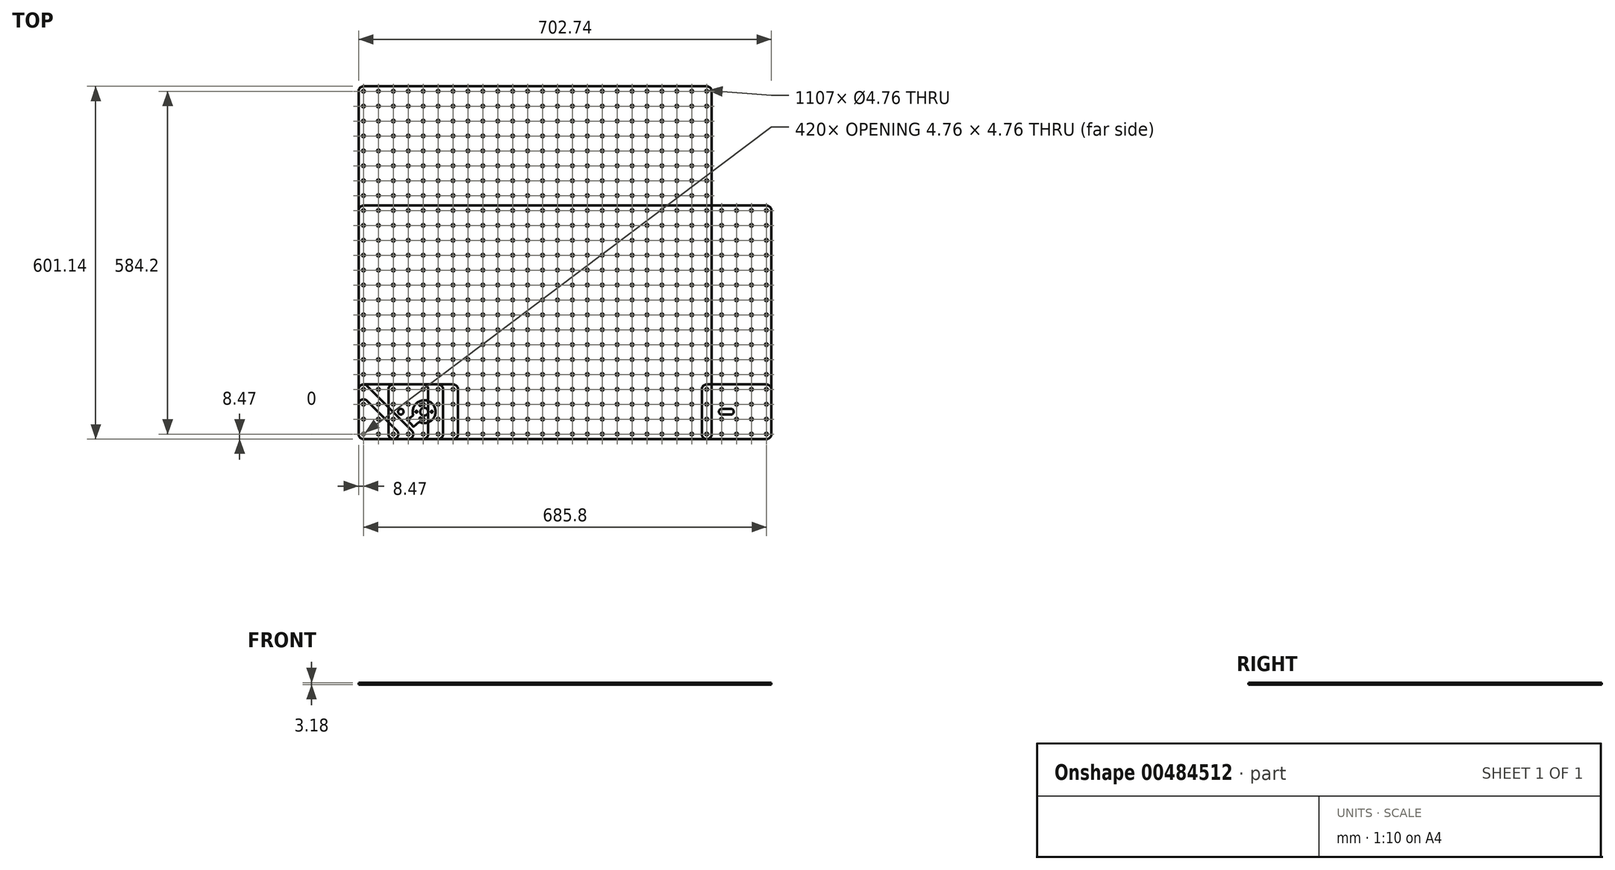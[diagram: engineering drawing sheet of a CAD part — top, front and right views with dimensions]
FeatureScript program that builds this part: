
annotation { "Feature Type Name" : "Feature", "Feature Type Description" : "" }
export const myFeature = defineFeature(function(context is Context, id is Id, definition is map)
    precondition{}
    {
        {
            assignVariable(context, id + "F0", {"name" : "bitDiameter", "anyValue" : 1 / 8});
        }
        {
            var Q0;
            Q0=qCreatedBy(makeId("Top.planeOp"),FACE);
            var sketch = newSketch(context, id + "F1", { "sketchPlane" : qUnion([Q0])});
            skCircle(sketch, "E0", {"center": v(0, 0) * mm, "radius": 2.38 * mm});
            skCircle(sketch, "E1.0.1.0", {"center": v(0, 25.4) * mm, "radius": 2.38 * mm});
            skCircle(sketch, "E1.1.0.0", {"center": v(25.4, 0) * mm, "radius": 2.38 * mm});
            skCircle(sketch, "E1.1.1.0", {"center": v(25.4, 25.4) * mm, "radius": 2.38 * mm});
            skCircle(sketch, "E1.2.0.0", {"center": v(50.8, 0) * mm, "radius": 2.38 * mm});
            skCircle(sketch, "E1.2.1.0", {"center": v(50.8, 25.4) * mm, "radius": 2.38 * mm});
            skLineSegment(sketch, "E1.direction1", {"start": v(0, 0) * mm, "end": v(25.4, 0) * mm, "construction": true});
            skLineSegment(sketch, "E1.direction2", {"start": v(0, 0) * mm, "end": v(0, 25.4) * mm, "construction": true});
            skCircle(sketch, "E2.0.0.2", {"center": v(0, 50.8) * mm, "radius": 2.38 * mm});
            skCircle(sketch, "E2.0.0.3", {"center": v(0, 76.2) * mm, "radius": 2.38 * mm});
            skCircle(sketch, "E2.0.0.4", {"center": v(0, 101.6) * mm, "radius": 2.38 * mm});
            skCircle(sketch, "E2.0.0.5", {"center": v(0, 127) * mm, "radius": 2.38 * mm});
            skCircle(sketch, "E2.0.0.6", {"center": v(0, 152.4) * mm, "radius": 2.38 * mm});
            skCircle(sketch, "E2.0.0.7", {"center": v(0, 177.8) * mm, "radius": 2.38 * mm});
            skCircle(sketch, "E2.0.0.8", {"center": v(0, 203.2) * mm, "radius": 2.38 * mm});
            skCircle(sketch, "E2.0.0.9", {"center": v(0, 228.6) * mm, "radius": 2.38 * mm});
            skCircle(sketch, "E2.0.0.10", {"center": v(0, 254) * mm, "radius": 2.38 * mm});
            skCircle(sketch, "E2.0.0.11", {"center": v(0, 279.4) * mm, "radius": 2.38 * mm});
            skCircle(sketch, "E2.0.0.12", {"center": v(0, 304.8) * mm, "radius": 2.38 * mm});
            skCircle(sketch, "E2.0.0.13", {"center": v(0, 330.2) * mm, "radius": 2.38 * mm});
            skCircle(sketch, "E2.0.0.14", {"center": v(0, 355.6) * mm, "radius": 2.38 * mm});
            skCircle(sketch, "E2.0.0.15", {"center": v(0, 381) * mm, "radius": 2.38 * mm});
            skCircle(sketch, "E2.0.0.16", {"center": v(0, 406.4) * mm, "radius": 2.38 * mm});
            skCircle(sketch, "E2.0.0.17", {"center": v(0, 431.8) * mm, "radius": 2.38 * mm});
            skCircle(sketch, "E2.0.0.18", {"center": v(0, 457.2) * mm, "radius": 2.38 * mm});
            skCircle(sketch, "E2.0.0.19", {"center": v(0, 482.6) * mm, "radius": 2.38 * mm});
            skCircle(sketch, "E2.0.0.20", {"center": v(0, 508) * mm, "radius": 2.38 * mm});
            skCircle(sketch, "E2.0.0.21", {"center": v(0, 533.4) * mm, "radius": 2.38 * mm});
            skCircle(sketch, "E2.0.0.22", {"center": v(0, 558.8) * mm, "radius": 2.38 * mm});
            skCircle(sketch, "E2.0.1.2", {"center": v(25.4, 50.8) * mm, "radius": 2.38 * mm});
            skCircle(sketch, "E2.0.1.3", {"center": v(25.4, 76.2) * mm, "radius": 2.38 * mm});
            skCircle(sketch, "E2.0.1.4", {"center": v(25.4, 101.6) * mm, "radius": 2.38 * mm});
            skCircle(sketch, "E2.0.1.5", {"center": v(25.4, 127) * mm, "radius": 2.38 * mm});
            skCircle(sketch, "E2.0.1.6", {"center": v(25.4, 152.4) * mm, "radius": 2.38 * mm});
            skCircle(sketch, "E2.0.1.7", {"center": v(25.4, 177.8) * mm, "radius": 2.38 * mm});
            skCircle(sketch, "E2.0.1.8", {"center": v(25.4, 203.2) * mm, "radius": 2.38 * mm});
            skCircle(sketch, "E2.0.1.9", {"center": v(25.4, 228.6) * mm, "radius": 2.38 * mm});
            skCircle(sketch, "E2.0.1.10", {"center": v(25.4, 254) * mm, "radius": 2.38 * mm});
            skCircle(sketch, "E2.0.1.11", {"center": v(25.4, 279.4) * mm, "radius": 2.38 * mm});
            skCircle(sketch, "E2.0.1.12", {"center": v(25.4, 304.8) * mm, "radius": 2.38 * mm});
            skCircle(sketch, "E2.0.1.13", {"center": v(25.4, 330.2) * mm, "radius": 2.38 * mm});
            skCircle(sketch, "E2.0.1.14", {"center": v(25.4, 355.6) * mm, "radius": 2.38 * mm});
            skCircle(sketch, "E2.0.1.15", {"center": v(25.4, 381) * mm, "radius": 2.38 * mm});
            skCircle(sketch, "E2.0.1.16", {"center": v(25.4, 406.4) * mm, "radius": 2.38 * mm});
            skCircle(sketch, "E2.0.1.17", {"center": v(25.4, 431.8) * mm, "radius": 2.38 * mm});
            skCircle(sketch, "E2.0.1.18", {"center": v(25.4, 457.2) * mm, "radius": 2.38 * mm});
            skCircle(sketch, "E2.0.1.19", {"center": v(25.4, 482.6) * mm, "radius": 2.38 * mm});
            skCircle(sketch, "E2.0.1.20", {"center": v(25.4, 508) * mm, "radius": 2.38 * mm});
            skCircle(sketch, "E2.0.1.21", {"center": v(25.4, 533.4) * mm, "radius": 2.38 * mm});
            skCircle(sketch, "E2.0.1.22", {"center": v(25.4, 558.8) * mm, "radius": 2.38 * mm});
            skCircle(sketch, "E2.0.2.2", {"center": v(50.8, 50.8) * mm, "radius": 2.38 * mm});
            skCircle(sketch, "E2.0.2.3", {"center": v(50.8, 76.2) * mm, "radius": 2.38 * mm});
            skCircle(sketch, "E2.0.2.4", {"center": v(50.8, 101.6) * mm, "radius": 2.38 * mm});
            skCircle(sketch, "E2.0.2.5", {"center": v(50.8, 127) * mm, "radius": 2.38 * mm});
            skCircle(sketch, "E2.0.2.6", {"center": v(50.8, 152.4) * mm, "radius": 2.38 * mm});
            skCircle(sketch, "E2.0.2.7", {"center": v(50.8, 177.8) * mm, "radius": 2.38 * mm});
            skCircle(sketch, "E2.0.2.8", {"center": v(50.8, 203.2) * mm, "radius": 2.38 * mm});
            skCircle(sketch, "E2.0.2.9", {"center": v(50.8, 228.6) * mm, "radius": 2.38 * mm});
            skCircle(sketch, "E2.0.2.10", {"center": v(50.8, 254) * mm, "radius": 2.38 * mm});
            skCircle(sketch, "E2.0.2.11", {"center": v(50.8, 279.4) * mm, "radius": 2.38 * mm});
            skCircle(sketch, "E2.0.2.12", {"center": v(50.8, 304.8) * mm, "radius": 2.38 * mm});
            skCircle(sketch, "E2.0.2.13", {"center": v(50.8, 330.2) * mm, "radius": 2.38 * mm});
            skCircle(sketch, "E2.0.2.14", {"center": v(50.8, 355.6) * mm, "radius": 2.38 * mm});
            skCircle(sketch, "E2.0.2.15", {"center": v(50.8, 381) * mm, "radius": 2.38 * mm});
            skCircle(sketch, "E2.0.2.16", {"center": v(50.8, 406.4) * mm, "radius": 2.38 * mm});
            skCircle(sketch, "E2.0.2.17", {"center": v(50.8, 431.8) * mm, "radius": 2.38 * mm});
            skCircle(sketch, "E2.0.2.18", {"center": v(50.8, 457.2) * mm, "radius": 2.38 * mm});
            skCircle(sketch, "E2.0.2.19", {"center": v(50.8, 482.6) * mm, "radius": 2.38 * mm});
            skCircle(sketch, "E2.0.2.20", {"center": v(50.8, 508) * mm, "radius": 2.38 * mm});
            skCircle(sketch, "E2.0.2.21", {"center": v(50.8, 533.4) * mm, "radius": 2.38 * mm});
            skCircle(sketch, "E2.0.2.22", {"center": v(50.8, 558.8) * mm, "radius": 2.38 * mm});
            skCircle(sketch, "E3.0.3.0", {"center": v(76.2, 0) * mm, "radius": 2.38 * mm});
            skCircle(sketch, "E3.0.3.1", {"center": v(76.2, 25.4) * mm, "radius": 2.38 * mm});
            skCircle(sketch, "E3.0.3.2", {"center": v(76.2, 50.8) * mm, "radius": 2.38 * mm});
            skCircle(sketch, "E3.0.3.3", {"center": v(76.2, 76.2) * mm, "radius": 2.38 * mm});
            skCircle(sketch, "E3.0.3.4", {"center": v(76.2, 101.6) * mm, "radius": 2.38 * mm});
            skCircle(sketch, "E3.0.3.5", {"center": v(76.2, 127) * mm, "radius": 2.38 * mm});
            skCircle(sketch, "E3.0.3.6", {"center": v(76.2, 152.4) * mm, "radius": 2.38 * mm});
            skCircle(sketch, "E3.0.3.7", {"center": v(76.2, 177.8) * mm, "radius": 2.38 * mm});
            skCircle(sketch, "E3.0.3.8", {"center": v(76.2, 203.2) * mm, "radius": 2.38 * mm});
            skCircle(sketch, "E3.0.3.9", {"center": v(76.2, 228.6) * mm, "radius": 2.38 * mm});
            skCircle(sketch, "E3.0.3.10", {"center": v(76.2, 254) * mm, "radius": 2.38 * mm});
            skCircle(sketch, "E3.0.3.11", {"center": v(76.2, 279.4) * mm, "radius": 2.38 * mm});
            skCircle(sketch, "E3.0.3.12", {"center": v(76.2, 304.8) * mm, "radius": 2.38 * mm});
            skCircle(sketch, "E3.0.3.13", {"center": v(76.2, 330.2) * mm, "radius": 2.38 * mm});
            skCircle(sketch, "E3.0.3.14", {"center": v(76.2, 355.6) * mm, "radius": 2.38 * mm});
            skCircle(sketch, "E3.0.3.15", {"center": v(76.2, 381) * mm, "radius": 2.38 * mm});
            skCircle(sketch, "E3.0.3.16", {"center": v(76.2, 406.4) * mm, "radius": 2.38 * mm});
            skCircle(sketch, "E3.0.3.17", {"center": v(76.2, 431.8) * mm, "radius": 2.38 * mm});
            skCircle(sketch, "E3.0.3.18", {"center": v(76.2, 457.2) * mm, "radius": 2.38 * mm});
            skCircle(sketch, "E3.0.3.19", {"center": v(76.2, 482.6) * mm, "radius": 2.38 * mm});
            skCircle(sketch, "E3.0.3.20", {"center": v(76.2, 508) * mm, "radius": 2.38 * mm});
            skCircle(sketch, "E3.0.3.21", {"center": v(76.2, 533.4) * mm, "radius": 2.38 * mm});
            skCircle(sketch, "E3.0.3.22", {"center": v(76.2, 558.8) * mm, "radius": 2.38 * mm});
            skCircle(sketch, "E3.0.4.0", {"center": v(101.6, 0) * mm, "radius": 2.38 * mm});
            skCircle(sketch, "E3.0.4.1", {"center": v(101.6, 25.4) * mm, "radius": 2.38 * mm});
            skCircle(sketch, "E3.0.4.2", {"center": v(101.6, 50.8) * mm, "radius": 2.38 * mm});
            skCircle(sketch, "E3.0.4.3", {"center": v(101.6, 76.2) * mm, "radius": 2.38 * mm});
            skCircle(sketch, "E3.0.4.4", {"center": v(101.6, 101.6) * mm, "radius": 2.38 * mm});
            skCircle(sketch, "E3.0.4.5", {"center": v(101.6, 127) * mm, "radius": 2.38 * mm});
            skCircle(sketch, "E3.0.4.6", {"center": v(101.6, 152.4) * mm, "radius": 2.38 * mm});
            skCircle(sketch, "E3.0.4.7", {"center": v(101.6, 177.8) * mm, "radius": 2.38 * mm});
            skCircle(sketch, "E3.0.4.8", {"center": v(101.6, 203.2) * mm, "radius": 2.38 * mm});
            skCircle(sketch, "E3.0.4.9", {"center": v(101.6, 228.6) * mm, "radius": 2.38 * mm});
            skCircle(sketch, "E3.0.4.10", {"center": v(101.6, 254) * mm, "radius": 2.38 * mm});
            skCircle(sketch, "E3.0.4.11", {"center": v(101.6, 279.4) * mm, "radius": 2.38 * mm});
            skCircle(sketch, "E3.0.4.12", {"center": v(101.6, 304.8) * mm, "radius": 2.38 * mm});
            skCircle(sketch, "E3.0.4.13", {"center": v(101.6, 330.2) * mm, "radius": 2.38 * mm});
            skCircle(sketch, "E3.0.4.14", {"center": v(101.6, 355.6) * mm, "radius": 2.38 * mm});
            skCircle(sketch, "E3.0.4.15", {"center": v(101.6, 381) * mm, "radius": 2.38 * mm});
            skCircle(sketch, "E3.0.4.16", {"center": v(101.6, 406.4) * mm, "radius": 2.38 * mm});
            skCircle(sketch, "E3.0.4.17", {"center": v(101.6, 431.8) * mm, "radius": 2.38 * mm});
            skCircle(sketch, "E3.0.4.18", {"center": v(101.6, 457.2) * mm, "radius": 2.38 * mm});
            skCircle(sketch, "E3.0.4.19", {"center": v(101.6, 482.6) * mm, "radius": 2.38 * mm});
            skCircle(sketch, "E3.0.4.20", {"center": v(101.6, 508) * mm, "radius": 2.38 * mm});
            skCircle(sketch, "E3.0.4.21", {"center": v(101.6, 533.4) * mm, "radius": 2.38 * mm});
            skCircle(sketch, "E3.0.4.22", {"center": v(101.6, 558.8) * mm, "radius": 2.38 * mm});
            skCircle(sketch, "E3.0.5.0", {"center": v(127, 0) * mm, "radius": 2.38 * mm});
            skCircle(sketch, "E3.0.5.1", {"center": v(127, 25.4) * mm, "radius": 2.38 * mm});
            skCircle(sketch, "E3.0.5.2", {"center": v(127, 50.8) * mm, "radius": 2.38 * mm});
            skCircle(sketch, "E3.0.5.3", {"center": v(127, 76.2) * mm, "radius": 2.38 * mm});
            skCircle(sketch, "E3.0.5.4", {"center": v(127, 101.6) * mm, "radius": 2.38 * mm});
            skCircle(sketch, "E3.0.5.5", {"center": v(127, 127) * mm, "radius": 2.38 * mm});
            skCircle(sketch, "E3.0.5.6", {"center": v(127, 152.4) * mm, "radius": 2.38 * mm});
            skCircle(sketch, "E3.0.5.7", {"center": v(127, 177.8) * mm, "radius": 2.38 * mm});
            skCircle(sketch, "E3.0.5.8", {"center": v(127, 203.2) * mm, "radius": 2.38 * mm});
            skCircle(sketch, "E3.0.5.9", {"center": v(127, 228.6) * mm, "radius": 2.38 * mm});
            skCircle(sketch, "E3.0.5.10", {"center": v(127, 254) * mm, "radius": 2.38 * mm});
            skCircle(sketch, "E3.0.5.11", {"center": v(127, 279.4) * mm, "radius": 2.38 * mm});
            skCircle(sketch, "E3.0.5.12", {"center": v(127, 304.8) * mm, "radius": 2.38 * mm});
            skCircle(sketch, "E3.0.5.13", {"center": v(127, 330.2) * mm, "radius": 2.38 * mm});
            skCircle(sketch, "E3.0.5.14", {"center": v(127, 355.6) * mm, "radius": 2.38 * mm});
            skCircle(sketch, "E3.0.5.15", {"center": v(127, 381) * mm, "radius": 2.38 * mm});
            skCircle(sketch, "E3.0.5.16", {"center": v(127, 406.4) * mm, "radius": 2.38 * mm});
            skCircle(sketch, "E3.0.5.17", {"center": v(127, 431.8) * mm, "radius": 2.38 * mm});
            skCircle(sketch, "E3.0.5.18", {"center": v(127, 457.2) * mm, "radius": 2.38 * mm});
            skCircle(sketch, "E3.0.5.19", {"center": v(127, 482.6) * mm, "radius": 2.38 * mm});
            skCircle(sketch, "E3.0.5.20", {"center": v(127, 508) * mm, "radius": 2.38 * mm});
            skCircle(sketch, "E3.0.5.21", {"center": v(127, 533.4) * mm, "radius": 2.38 * mm});
            skCircle(sketch, "E3.0.5.22", {"center": v(127, 558.8) * mm, "radius": 2.38 * mm});
            skCircle(sketch, "E3.0.6.0", {"center": v(152.4, 0) * mm, "radius": 2.38 * mm});
            skCircle(sketch, "E3.0.6.1", {"center": v(152.4, 25.4) * mm, "radius": 2.38 * mm});
            skCircle(sketch, "E3.0.6.2", {"center": v(152.4, 50.8) * mm, "radius": 2.38 * mm});
            skCircle(sketch, "E3.0.6.3", {"center": v(152.4, 76.2) * mm, "radius": 2.38 * mm});
            skCircle(sketch, "E3.0.6.4", {"center": v(152.4, 101.6) * mm, "radius": 2.38 * mm});
            skCircle(sketch, "E3.0.6.5", {"center": v(152.4, 127) * mm, "radius": 2.38 * mm});
            skCircle(sketch, "E3.0.6.6", {"center": v(152.4, 152.4) * mm, "radius": 2.38 * mm});
            skCircle(sketch, "E3.0.6.7", {"center": v(152.4, 177.8) * mm, "radius": 2.38 * mm});
            skCircle(sketch, "E3.0.6.8", {"center": v(152.4, 203.2) * mm, "radius": 2.38 * mm});
            skCircle(sketch, "E3.0.6.9", {"center": v(152.4, 228.6) * mm, "radius": 2.38 * mm});
            skCircle(sketch, "E3.0.6.10", {"center": v(152.4, 254) * mm, "radius": 2.38 * mm});
            skCircle(sketch, "E3.0.6.11", {"center": v(152.4, 279.4) * mm, "radius": 2.38 * mm});
            skCircle(sketch, "E3.0.6.12", {"center": v(152.4, 304.8) * mm, "radius": 2.38 * mm});
            skCircle(sketch, "E3.0.6.13", {"center": v(152.4, 330.2) * mm, "radius": 2.38 * mm});
            skCircle(sketch, "E3.0.6.14", {"center": v(152.4, 355.6) * mm, "radius": 2.38 * mm});
            skCircle(sketch, "E3.0.6.15", {"center": v(152.4, 381) * mm, "radius": 2.38 * mm});
            skCircle(sketch, "E3.0.6.16", {"center": v(152.4, 406.4) * mm, "radius": 2.38 * mm});
            skCircle(sketch, "E3.0.6.17", {"center": v(152.4, 431.8) * mm, "radius": 2.38 * mm});
            skCircle(sketch, "E3.0.6.18", {"center": v(152.4, 457.2) * mm, "radius": 2.38 * mm});
            skCircle(sketch, "E3.0.6.19", {"center": v(152.4, 482.6) * mm, "radius": 2.38 * mm});
            skCircle(sketch, "E3.0.6.20", {"center": v(152.4, 508) * mm, "radius": 2.38 * mm});
            skCircle(sketch, "E3.0.6.21", {"center": v(152.4, 533.4) * mm, "radius": 2.38 * mm});
            skCircle(sketch, "E3.0.6.22", {"center": v(152.4, 558.8) * mm, "radius": 2.38 * mm});
            skCircle(sketch, "E3.0.7.0", {"center": v(177.8, 0) * mm, "radius": 2.38 * mm});
            skCircle(sketch, "E3.0.7.1", {"center": v(177.8, 25.4) * mm, "radius": 2.38 * mm});
            skCircle(sketch, "E3.0.7.2", {"center": v(177.8, 50.8) * mm, "radius": 2.38 * mm});
            skCircle(sketch, "E3.0.7.3", {"center": v(177.8, 76.2) * mm, "radius": 2.38 * mm});
            skCircle(sketch, "E3.0.7.4", {"center": v(177.8, 101.6) * mm, "radius": 2.38 * mm});
            skCircle(sketch, "E3.0.7.5", {"center": v(177.8, 127) * mm, "radius": 2.38 * mm});
            skCircle(sketch, "E3.0.7.6", {"center": v(177.8, 152.4) * mm, "radius": 2.38 * mm});
            skCircle(sketch, "E3.0.7.7", {"center": v(177.8, 177.8) * mm, "radius": 2.38 * mm});
            skCircle(sketch, "E3.0.7.8", {"center": v(177.8, 203.2) * mm, "radius": 2.38 * mm});
            skCircle(sketch, "E3.0.7.9", {"center": v(177.8, 228.6) * mm, "radius": 2.38 * mm});
            skCircle(sketch, "E3.0.7.10", {"center": v(177.8, 254) * mm, "radius": 2.38 * mm});
            skCircle(sketch, "E3.0.7.11", {"center": v(177.8, 279.4) * mm, "radius": 2.38 * mm});
            skCircle(sketch, "E3.0.7.12", {"center": v(177.8, 304.8) * mm, "radius": 2.38 * mm});
            skCircle(sketch, "E3.0.7.13", {"center": v(177.8, 330.2) * mm, "radius": 2.38 * mm});
            skCircle(sketch, "E3.0.7.14", {"center": v(177.8, 355.6) * mm, "radius": 2.38 * mm});
            skCircle(sketch, "E3.0.7.15", {"center": v(177.8, 381) * mm, "radius": 2.38 * mm});
            skCircle(sketch, "E3.0.7.16", {"center": v(177.8, 406.4) * mm, "radius": 2.38 * mm});
            skCircle(sketch, "E3.0.7.17", {"center": v(177.8, 431.8) * mm, "radius": 2.38 * mm});
            skCircle(sketch, "E3.0.7.18", {"center": v(177.8, 457.2) * mm, "radius": 2.38 * mm});
            skCircle(sketch, "E3.0.7.19", {"center": v(177.8, 482.6) * mm, "radius": 2.38 * mm});
            skCircle(sketch, "E3.0.7.20", {"center": v(177.8, 508) * mm, "radius": 2.38 * mm});
            skCircle(sketch, "E3.0.7.21", {"center": v(177.8, 533.4) * mm, "radius": 2.38 * mm});
            skCircle(sketch, "E3.0.7.22", {"center": v(177.8, 558.8) * mm, "radius": 2.38 * mm});
            skCircle(sketch, "E3.0.8.0", {"center": v(203.2, 0) * mm, "radius": 2.38 * mm});
            skCircle(sketch, "E3.0.8.1", {"center": v(203.2, 25.4) * mm, "radius": 2.38 * mm});
            skCircle(sketch, "E3.0.8.2", {"center": v(203.2, 50.8) * mm, "radius": 2.38 * mm});
            skCircle(sketch, "E3.0.8.3", {"center": v(203.2, 76.2) * mm, "radius": 2.38 * mm});
            skCircle(sketch, "E3.0.8.4", {"center": v(203.2, 101.6) * mm, "radius": 2.38 * mm});
            skCircle(sketch, "E3.0.8.5", {"center": v(203.2, 127) * mm, "radius": 2.38 * mm});
            skCircle(sketch, "E3.0.8.6", {"center": v(203.2, 152.4) * mm, "radius": 2.38 * mm});
            skCircle(sketch, "E3.0.8.7", {"center": v(203.2, 177.8) * mm, "radius": 2.38 * mm});
            skCircle(sketch, "E3.0.8.8", {"center": v(203.2, 203.2) * mm, "radius": 2.38 * mm});
            skCircle(sketch, "E3.0.8.9", {"center": v(203.2, 228.6) * mm, "radius": 2.38 * mm});
            skCircle(sketch, "E3.0.8.10", {"center": v(203.2, 254) * mm, "radius": 2.38 * mm});
            skCircle(sketch, "E3.0.8.11", {"center": v(203.2, 279.4) * mm, "radius": 2.38 * mm});
            skCircle(sketch, "E3.0.8.12", {"center": v(203.2, 304.8) * mm, "radius": 2.38 * mm});
            skCircle(sketch, "E3.0.8.13", {"center": v(203.2, 330.2) * mm, "radius": 2.38 * mm});
            skCircle(sketch, "E3.0.8.14", {"center": v(203.2, 355.6) * mm, "radius": 2.38 * mm});
            skCircle(sketch, "E3.0.8.15", {"center": v(203.2, 381) * mm, "radius": 2.38 * mm});
            skCircle(sketch, "E3.0.8.16", {"center": v(203.2, 406.4) * mm, "radius": 2.38 * mm});
            skCircle(sketch, "E3.0.8.17", {"center": v(203.2, 431.8) * mm, "radius": 2.38 * mm});
            skCircle(sketch, "E3.0.8.18", {"center": v(203.2, 457.2) * mm, "radius": 2.38 * mm});
            skCircle(sketch, "E3.0.8.19", {"center": v(203.2, 482.6) * mm, "radius": 2.38 * mm});
            skCircle(sketch, "E3.0.8.20", {"center": v(203.2, 508) * mm, "radius": 2.38 * mm});
            skCircle(sketch, "E3.0.8.21", {"center": v(203.2, 533.4) * mm, "radius": 2.38 * mm});
            skCircle(sketch, "E3.0.8.22", {"center": v(203.2, 558.8) * mm, "radius": 2.38 * mm});
            skCircle(sketch, "E3.0.9.0", {"center": v(228.6, 0) * mm, "radius": 2.38 * mm});
            skCircle(sketch, "E3.0.9.1", {"center": v(228.6, 25.4) * mm, "radius": 2.38 * mm});
            skCircle(sketch, "E3.0.9.2", {"center": v(228.6, 50.8) * mm, "radius": 2.38 * mm});
            skCircle(sketch, "E3.0.9.3", {"center": v(228.6, 76.2) * mm, "radius": 2.38 * mm});
            skCircle(sketch, "E3.0.9.4", {"center": v(228.6, 101.6) * mm, "radius": 2.38 * mm});
            skCircle(sketch, "E3.0.9.5", {"center": v(228.6, 127) * mm, "radius": 2.38 * mm});
            skCircle(sketch, "E3.0.9.6", {"center": v(228.6, 152.4) * mm, "radius": 2.38 * mm});
            skCircle(sketch, "E3.0.9.7", {"center": v(228.6, 177.8) * mm, "radius": 2.38 * mm});
            skCircle(sketch, "E3.0.9.8", {"center": v(228.6, 203.2) * mm, "radius": 2.38 * mm});
            skCircle(sketch, "E3.0.9.9", {"center": v(228.6, 228.6) * mm, "radius": 2.38 * mm});
            skCircle(sketch, "E3.0.9.10", {"center": v(228.6, 254) * mm, "radius": 2.38 * mm});
            skCircle(sketch, "E3.0.9.11", {"center": v(228.6, 279.4) * mm, "radius": 2.38 * mm});
            skCircle(sketch, "E3.0.9.12", {"center": v(228.6, 304.8) * mm, "radius": 2.38 * mm});
            skCircle(sketch, "E3.0.9.13", {"center": v(228.6, 330.2) * mm, "radius": 2.38 * mm});
            skCircle(sketch, "E3.0.9.14", {"center": v(228.6, 355.6) * mm, "radius": 2.38 * mm});
            skCircle(sketch, "E3.0.9.15", {"center": v(228.6, 381) * mm, "radius": 2.38 * mm});
            skCircle(sketch, "E3.0.9.16", {"center": v(228.6, 406.4) * mm, "radius": 2.38 * mm});
            skCircle(sketch, "E3.0.9.17", {"center": v(228.6, 431.8) * mm, "radius": 2.38 * mm});
            skCircle(sketch, "E3.0.9.18", {"center": v(228.6, 457.2) * mm, "radius": 2.38 * mm});
            skCircle(sketch, "E3.0.9.19", {"center": v(228.6, 482.6) * mm, "radius": 2.38 * mm});
            skCircle(sketch, "E3.0.9.20", {"center": v(228.6, 508) * mm, "radius": 2.38 * mm});
            skCircle(sketch, "E3.0.9.21", {"center": v(228.6, 533.4) * mm, "radius": 2.38 * mm});
            skCircle(sketch, "E3.0.9.22", {"center": v(228.6, 558.8) * mm, "radius": 2.38 * mm});
            skCircle(sketch, "E3.0.10.0", {"center": v(254, 0) * mm, "radius": 2.38 * mm});
            skCircle(sketch, "E3.0.10.1", {"center": v(254, 25.4) * mm, "radius": 2.38 * mm});
            skCircle(sketch, "E3.0.10.2", {"center": v(254, 50.8) * mm, "radius": 2.38 * mm});
            skCircle(sketch, "E3.0.10.3", {"center": v(254, 76.2) * mm, "radius": 2.38 * mm});
            skCircle(sketch, "E3.0.10.4", {"center": v(254, 101.6) * mm, "radius": 2.38 * mm});
            skCircle(sketch, "E3.0.10.5", {"center": v(254, 127) * mm, "radius": 2.38 * mm});
            skCircle(sketch, "E3.0.10.6", {"center": v(254, 152.4) * mm, "radius": 2.38 * mm});
            skCircle(sketch, "E3.0.10.7", {"center": v(254, 177.8) * mm, "radius": 2.38 * mm});
            skCircle(sketch, "E3.0.10.8", {"center": v(254, 203.2) * mm, "radius": 2.38 * mm});
            skCircle(sketch, "E3.0.10.9", {"center": v(254, 228.6) * mm, "radius": 2.38 * mm});
            skCircle(sketch, "E3.0.10.10", {"center": v(254, 254) * mm, "radius": 2.38 * mm});
            skCircle(sketch, "E3.0.10.11", {"center": v(254, 279.4) * mm, "radius": 2.38 * mm});
            skCircle(sketch, "E3.0.10.12", {"center": v(254, 304.8) * mm, "radius": 2.38 * mm});
            skCircle(sketch, "E3.0.10.13", {"center": v(254, 330.2) * mm, "radius": 2.38 * mm});
            skCircle(sketch, "E3.0.10.14", {"center": v(254, 355.6) * mm, "radius": 2.38 * mm});
            skCircle(sketch, "E3.0.10.15", {"center": v(254, 381) * mm, "radius": 2.38 * mm});
            skCircle(sketch, "E3.0.10.16", {"center": v(254, 406.4) * mm, "radius": 2.38 * mm});
            skCircle(sketch, "E3.0.10.17", {"center": v(254, 431.8) * mm, "radius": 2.38 * mm});
            skCircle(sketch, "E3.0.10.18", {"center": v(254, 457.2) * mm, "radius": 2.38 * mm});
            skCircle(sketch, "E3.0.10.19", {"center": v(254, 482.6) * mm, "radius": 2.38 * mm});
            skCircle(sketch, "E3.0.10.20", {"center": v(254, 508) * mm, "radius": 2.38 * mm});
            skCircle(sketch, "E3.0.10.21", {"center": v(254, 533.4) * mm, "radius": 2.38 * mm});
            skCircle(sketch, "E3.0.10.22", {"center": v(254, 558.8) * mm, "radius": 2.38 * mm});
            skCircle(sketch, "E3.0.11.0", {"center": v(279.4, 0) * mm, "radius": 2.38 * mm});
            skCircle(sketch, "E3.0.11.1", {"center": v(279.4, 25.4) * mm, "radius": 2.38 * mm});
            skCircle(sketch, "E3.0.11.2", {"center": v(279.4, 50.8) * mm, "radius": 2.38 * mm});
            skCircle(sketch, "E3.0.11.3", {"center": v(279.4, 76.2) * mm, "radius": 2.38 * mm});
            skCircle(sketch, "E3.0.11.4", {"center": v(279.4, 101.6) * mm, "radius": 2.38 * mm});
            skCircle(sketch, "E3.0.11.5", {"center": v(279.4, 127) * mm, "radius": 2.38 * mm});
            skCircle(sketch, "E3.0.11.6", {"center": v(279.4, 152.4) * mm, "radius": 2.38 * mm});
            skCircle(sketch, "E3.0.11.7", {"center": v(279.4, 177.8) * mm, "radius": 2.38 * mm});
            skCircle(sketch, "E3.0.11.8", {"center": v(279.4, 203.2) * mm, "radius": 2.38 * mm});
            skCircle(sketch, "E3.0.11.9", {"center": v(279.4, 228.6) * mm, "radius": 2.38 * mm});
            skCircle(sketch, "E3.0.11.10", {"center": v(279.4, 254) * mm, "radius": 2.38 * mm});
            skCircle(sketch, "E3.0.11.11", {"center": v(279.4, 279.4) * mm, "radius": 2.38 * mm});
            skCircle(sketch, "E3.0.11.12", {"center": v(279.4, 304.8) * mm, "radius": 2.38 * mm});
            skCircle(sketch, "E3.0.11.13", {"center": v(279.4, 330.2) * mm, "radius": 2.38 * mm});
            skCircle(sketch, "E3.0.11.14", {"center": v(279.4, 355.6) * mm, "radius": 2.38 * mm});
            skCircle(sketch, "E3.0.11.15", {"center": v(279.4, 381) * mm, "radius": 2.38 * mm});
            skCircle(sketch, "E3.0.11.16", {"center": v(279.4, 406.4) * mm, "radius": 2.38 * mm});
            skCircle(sketch, "E3.0.11.17", {"center": v(279.4, 431.8) * mm, "radius": 2.38 * mm});
            skCircle(sketch, "E3.0.11.18", {"center": v(279.4, 457.2) * mm, "radius": 2.38 * mm});
            skCircle(sketch, "E3.0.11.19", {"center": v(279.4, 482.6) * mm, "radius": 2.38 * mm});
            skCircle(sketch, "E3.0.11.20", {"center": v(279.4, 508) * mm, "radius": 2.38 * mm});
            skCircle(sketch, "E3.0.11.21", {"center": v(279.4, 533.4) * mm, "radius": 2.38 * mm});
            skCircle(sketch, "E3.0.11.22", {"center": v(279.4, 558.8) * mm, "radius": 2.38 * mm});
            skCircle(sketch, "E3.0.12.0", {"center": v(304.8, 0) * mm, "radius": 2.38 * mm});
            skCircle(sketch, "E3.0.12.1", {"center": v(304.8, 25.4) * mm, "radius": 2.38 * mm});
            skCircle(sketch, "E3.0.12.2", {"center": v(304.8, 50.8) * mm, "radius": 2.38 * mm});
            skCircle(sketch, "E3.0.12.3", {"center": v(304.8, 76.2) * mm, "radius": 2.38 * mm});
            skCircle(sketch, "E3.0.12.4", {"center": v(304.8, 101.6) * mm, "radius": 2.38 * mm});
            skCircle(sketch, "E3.0.12.5", {"center": v(304.8, 127) * mm, "radius": 2.38 * mm});
            skCircle(sketch, "E3.0.12.6", {"center": v(304.8, 152.4) * mm, "radius": 2.38 * mm});
            skCircle(sketch, "E3.0.12.7", {"center": v(304.8, 177.8) * mm, "radius": 2.38 * mm});
            skCircle(sketch, "E3.0.12.8", {"center": v(304.8, 203.2) * mm, "radius": 2.38 * mm});
            skCircle(sketch, "E3.0.12.9", {"center": v(304.8, 228.6) * mm, "radius": 2.38 * mm});
            skCircle(sketch, "E3.0.12.10", {"center": v(304.8, 254) * mm, "radius": 2.38 * mm});
            skCircle(sketch, "E3.0.12.11", {"center": v(304.8, 279.4) * mm, "radius": 2.38 * mm});
            skCircle(sketch, "E3.0.12.12", {"center": v(304.8, 304.8) * mm, "radius": 2.38 * mm});
            skCircle(sketch, "E3.0.12.13", {"center": v(304.8, 330.2) * mm, "radius": 2.38 * mm});
            skCircle(sketch, "E3.0.12.14", {"center": v(304.8, 355.6) * mm, "radius": 2.38 * mm});
            skCircle(sketch, "E3.0.12.15", {"center": v(304.8, 381) * mm, "radius": 2.38 * mm});
            skCircle(sketch, "E3.0.12.16", {"center": v(304.8, 406.4) * mm, "radius": 2.38 * mm});
            skCircle(sketch, "E3.0.12.17", {"center": v(304.8, 431.8) * mm, "radius": 2.38 * mm});
            skCircle(sketch, "E3.0.12.18", {"center": v(304.8, 457.2) * mm, "radius": 2.38 * mm});
            skCircle(sketch, "E3.0.12.19", {"center": v(304.8, 482.6) * mm, "radius": 2.38 * mm});
            skCircle(sketch, "E3.0.12.20", {"center": v(304.8, 508) * mm, "radius": 2.38 * mm});
            skCircle(sketch, "E3.0.12.21", {"center": v(304.8, 533.4) * mm, "radius": 2.38 * mm});
            skCircle(sketch, "E3.0.12.22", {"center": v(304.8, 558.8) * mm, "radius": 2.38 * mm});
            skCircle(sketch, "E3.0.13.0", {"center": v(330.2, 0) * mm, "radius": 2.38 * mm});
            skCircle(sketch, "E3.0.13.1", {"center": v(330.2, 25.4) * mm, "radius": 2.38 * mm});
            skCircle(sketch, "E3.0.13.2", {"center": v(330.2, 50.8) * mm, "radius": 2.38 * mm});
            skCircle(sketch, "E3.0.13.3", {"center": v(330.2, 76.2) * mm, "radius": 2.38 * mm});
            skCircle(sketch, "E3.0.13.4", {"center": v(330.2, 101.6) * mm, "radius": 2.38 * mm});
            skCircle(sketch, "E3.0.13.5", {"center": v(330.2, 127) * mm, "radius": 2.38 * mm});
            skCircle(sketch, "E3.0.13.6", {"center": v(330.2, 152.4) * mm, "radius": 2.38 * mm});
            skCircle(sketch, "E3.0.13.7", {"center": v(330.2, 177.8) * mm, "radius": 2.38 * mm});
            skCircle(sketch, "E3.0.13.8", {"center": v(330.2, 203.2) * mm, "radius": 2.38 * mm});
            skCircle(sketch, "E3.0.13.9", {"center": v(330.2, 228.6) * mm, "radius": 2.38 * mm});
            skCircle(sketch, "E3.0.13.10", {"center": v(330.2, 254) * mm, "radius": 2.38 * mm});
            skCircle(sketch, "E3.0.13.11", {"center": v(330.2, 279.4) * mm, "radius": 2.38 * mm});
            skCircle(sketch, "E3.0.13.12", {"center": v(330.2, 304.8) * mm, "radius": 2.38 * mm});
            skCircle(sketch, "E3.0.13.13", {"center": v(330.2, 330.2) * mm, "radius": 2.38 * mm});
            skCircle(sketch, "E3.0.13.14", {"center": v(330.2, 355.6) * mm, "radius": 2.38 * mm});
            skCircle(sketch, "E3.0.13.15", {"center": v(330.2, 381) * mm, "radius": 2.38 * mm});
            skCircle(sketch, "E3.0.13.16", {"center": v(330.2, 406.4) * mm, "radius": 2.38 * mm});
            skCircle(sketch, "E3.0.13.17", {"center": v(330.2, 431.8) * mm, "radius": 2.38 * mm});
            skCircle(sketch, "E3.0.13.18", {"center": v(330.2, 457.2) * mm, "radius": 2.38 * mm});
            skCircle(sketch, "E3.0.13.19", {"center": v(330.2, 482.6) * mm, "radius": 2.38 * mm});
            skCircle(sketch, "E3.0.13.20", {"center": v(330.2, 508) * mm, "radius": 2.38 * mm});
            skCircle(sketch, "E3.0.13.21", {"center": v(330.2, 533.4) * mm, "radius": 2.38 * mm});
            skCircle(sketch, "E3.0.13.22", {"center": v(330.2, 558.8) * mm, "radius": 2.38 * mm});
            skCircle(sketch, "E3.0.14.0", {"center": v(355.6, 0) * mm, "radius": 2.38 * mm});
            skCircle(sketch, "E3.0.14.1", {"center": v(355.6, 25.4) * mm, "radius": 2.38 * mm});
            skCircle(sketch, "E3.0.14.2", {"center": v(355.6, 50.8) * mm, "radius": 2.38 * mm});
            skCircle(sketch, "E3.0.14.3", {"center": v(355.6, 76.2) * mm, "radius": 2.38 * mm});
            skCircle(sketch, "E3.0.14.4", {"center": v(355.6, 101.6) * mm, "radius": 2.38 * mm});
            skCircle(sketch, "E3.0.14.5", {"center": v(355.6, 127) * mm, "radius": 2.38 * mm});
            skCircle(sketch, "E3.0.14.6", {"center": v(355.6, 152.4) * mm, "radius": 2.38 * mm});
            skCircle(sketch, "E3.0.14.7", {"center": v(355.6, 177.8) * mm, "radius": 2.38 * mm});
            skCircle(sketch, "E3.0.14.8", {"center": v(355.6, 203.2) * mm, "radius": 2.38 * mm});
            skCircle(sketch, "E3.0.14.9", {"center": v(355.6, 228.6) * mm, "radius": 2.38 * mm});
            skCircle(sketch, "E3.0.14.10", {"center": v(355.6, 254) * mm, "radius": 2.38 * mm});
            skCircle(sketch, "E3.0.14.11", {"center": v(355.6, 279.4) * mm, "radius": 2.38 * mm});
            skCircle(sketch, "E3.0.14.12", {"center": v(355.6, 304.8) * mm, "radius": 2.38 * mm});
            skCircle(sketch, "E3.0.14.13", {"center": v(355.6, 330.2) * mm, "radius": 2.38 * mm});
            skCircle(sketch, "E3.0.14.14", {"center": v(355.6, 355.6) * mm, "radius": 2.38 * mm});
            skCircle(sketch, "E3.0.14.15", {"center": v(355.6, 381) * mm, "radius": 2.38 * mm});
            skCircle(sketch, "E3.0.14.16", {"center": v(355.6, 406.4) * mm, "radius": 2.38 * mm});
            skCircle(sketch, "E3.0.14.17", {"center": v(355.6, 431.8) * mm, "radius": 2.38 * mm});
            skCircle(sketch, "E3.0.14.18", {"center": v(355.6, 457.2) * mm, "radius": 2.38 * mm});
            skCircle(sketch, "E3.0.14.19", {"center": v(355.6, 482.6) * mm, "radius": 2.38 * mm});
            skCircle(sketch, "E3.0.14.20", {"center": v(355.6, 508) * mm, "radius": 2.38 * mm});
            skCircle(sketch, "E3.0.14.21", {"center": v(355.6, 533.4) * mm, "radius": 2.38 * mm});
            skCircle(sketch, "E3.0.14.22", {"center": v(355.6, 558.8) * mm, "radius": 2.38 * mm});
            skCircle(sketch, "E3.0.15.0", {"center": v(381, 0) * mm, "radius": 2.38 * mm});
            skCircle(sketch, "E3.0.15.1", {"center": v(381, 25.4) * mm, "radius": 2.38 * mm});
            skCircle(sketch, "E3.0.15.2", {"center": v(381, 50.8) * mm, "radius": 2.38 * mm});
            skCircle(sketch, "E3.0.15.3", {"center": v(381, 76.2) * mm, "radius": 2.38 * mm});
            skCircle(sketch, "E3.0.15.4", {"center": v(381, 101.6) * mm, "radius": 2.38 * mm});
            skCircle(sketch, "E3.0.15.5", {"center": v(381, 127) * mm, "radius": 2.38 * mm});
            skCircle(sketch, "E3.0.15.6", {"center": v(381, 152.4) * mm, "radius": 2.38 * mm});
            skCircle(sketch, "E3.0.15.7", {"center": v(381, 177.8) * mm, "radius": 2.38 * mm});
            skCircle(sketch, "E3.0.15.8", {"center": v(381, 203.2) * mm, "radius": 2.38 * mm});
            skCircle(sketch, "E3.0.15.9", {"center": v(381, 228.6) * mm, "radius": 2.38 * mm});
            skCircle(sketch, "E3.0.15.10", {"center": v(381, 254) * mm, "radius": 2.38 * mm});
            skCircle(sketch, "E3.0.15.11", {"center": v(381, 279.4) * mm, "radius": 2.38 * mm});
            skCircle(sketch, "E3.0.15.12", {"center": v(381, 304.8) * mm, "radius": 2.38 * mm});
            skCircle(sketch, "E3.0.15.13", {"center": v(381, 330.2) * mm, "radius": 2.38 * mm});
            skCircle(sketch, "E3.0.15.14", {"center": v(381, 355.6) * mm, "radius": 2.38 * mm});
            skCircle(sketch, "E3.0.15.15", {"center": v(381, 381) * mm, "radius": 2.38 * mm});
            skCircle(sketch, "E3.0.15.16", {"center": v(381, 406.4) * mm, "radius": 2.38 * mm});
            skCircle(sketch, "E3.0.15.17", {"center": v(381, 431.8) * mm, "radius": 2.38 * mm});
            skCircle(sketch, "E3.0.15.18", {"center": v(381, 457.2) * mm, "radius": 2.38 * mm});
            skCircle(sketch, "E3.0.15.19", {"center": v(381, 482.6) * mm, "radius": 2.38 * mm});
            skCircle(sketch, "E3.0.15.20", {"center": v(381, 508) * mm, "radius": 2.38 * mm});
            skCircle(sketch, "E3.0.15.21", {"center": v(381, 533.4) * mm, "radius": 2.38 * mm});
            skCircle(sketch, "E3.0.15.22", {"center": v(381, 558.8) * mm, "radius": 2.38 * mm});
            skCircle(sketch, "E3.0.16.0", {"center": v(406.4, 0) * mm, "radius": 2.38 * mm});
            skCircle(sketch, "E3.0.16.1", {"center": v(406.4, 25.4) * mm, "radius": 2.38 * mm});
            skCircle(sketch, "E3.0.16.2", {"center": v(406.4, 50.8) * mm, "radius": 2.38 * mm});
            skCircle(sketch, "E3.0.16.3", {"center": v(406.4, 76.2) * mm, "radius": 2.38 * mm});
            skCircle(sketch, "E3.0.16.4", {"center": v(406.4, 101.6) * mm, "radius": 2.38 * mm});
            skCircle(sketch, "E3.0.16.5", {"center": v(406.4, 127) * mm, "radius": 2.38 * mm});
            skCircle(sketch, "E3.0.16.6", {"center": v(406.4, 152.4) * mm, "radius": 2.38 * mm});
            skCircle(sketch, "E3.0.16.7", {"center": v(406.4, 177.8) * mm, "radius": 2.38 * mm});
            skCircle(sketch, "E3.0.16.8", {"center": v(406.4, 203.2) * mm, "radius": 2.38 * mm});
            skCircle(sketch, "E3.0.16.9", {"center": v(406.4, 228.6) * mm, "radius": 2.38 * mm});
            skCircle(sketch, "E3.0.16.10", {"center": v(406.4, 254) * mm, "radius": 2.38 * mm});
            skCircle(sketch, "E3.0.16.11", {"center": v(406.4, 279.4) * mm, "radius": 2.38 * mm});
            skCircle(sketch, "E3.0.16.12", {"center": v(406.4, 304.8) * mm, "radius": 2.38 * mm});
            skCircle(sketch, "E3.0.16.13", {"center": v(406.4, 330.2) * mm, "radius": 2.38 * mm});
            skCircle(sketch, "E3.0.16.14", {"center": v(406.4, 355.6) * mm, "radius": 2.38 * mm});
            skCircle(sketch, "E3.0.16.15", {"center": v(406.4, 381) * mm, "radius": 2.38 * mm});
            skCircle(sketch, "E3.0.16.16", {"center": v(406.4, 406.4) * mm, "radius": 2.38 * mm});
            skCircle(sketch, "E3.0.16.17", {"center": v(406.4, 431.8) * mm, "radius": 2.38 * mm});
            skCircle(sketch, "E3.0.16.18", {"center": v(406.4, 457.2) * mm, "radius": 2.38 * mm});
            skCircle(sketch, "E3.0.16.19", {"center": v(406.4, 482.6) * mm, "radius": 2.38 * mm});
            skCircle(sketch, "E3.0.16.20", {"center": v(406.4, 508) * mm, "radius": 2.38 * mm});
            skCircle(sketch, "E3.0.16.21", {"center": v(406.4, 533.4) * mm, "radius": 2.38 * mm});
            skCircle(sketch, "E3.0.16.22", {"center": v(406.4, 558.8) * mm, "radius": 2.38 * mm});
            skCircle(sketch, "E3.0.17.0", {"center": v(431.8, 0) * mm, "radius": 2.38 * mm});
            skCircle(sketch, "E3.0.17.1", {"center": v(431.8, 25.4) * mm, "radius": 2.38 * mm});
            skCircle(sketch, "E3.0.17.2", {"center": v(431.8, 50.8) * mm, "radius": 2.38 * mm});
            skCircle(sketch, "E3.0.17.3", {"center": v(431.8, 76.2) * mm, "radius": 2.38 * mm});
            skCircle(sketch, "E3.0.17.4", {"center": v(431.8, 101.6) * mm, "radius": 2.38 * mm});
            skCircle(sketch, "E3.0.17.5", {"center": v(431.8, 127) * mm, "radius": 2.38 * mm});
            skCircle(sketch, "E3.0.17.6", {"center": v(431.8, 152.4) * mm, "radius": 2.38 * mm});
            skCircle(sketch, "E3.0.17.7", {"center": v(431.8, 177.8) * mm, "radius": 2.38 * mm});
            skCircle(sketch, "E3.0.17.8", {"center": v(431.8, 203.2) * mm, "radius": 2.38 * mm});
            skCircle(sketch, "E3.0.17.9", {"center": v(431.8, 228.6) * mm, "radius": 2.38 * mm});
            skCircle(sketch, "E3.0.17.10", {"center": v(431.8, 254) * mm, "radius": 2.38 * mm});
            skCircle(sketch, "E3.0.17.11", {"center": v(431.8, 279.4) * mm, "radius": 2.38 * mm});
            skCircle(sketch, "E3.0.17.12", {"center": v(431.8, 304.8) * mm, "radius": 2.38 * mm});
            skCircle(sketch, "E3.0.17.13", {"center": v(431.8, 330.2) * mm, "radius": 2.38 * mm});
            skCircle(sketch, "E3.0.17.14", {"center": v(431.8, 355.6) * mm, "radius": 2.38 * mm});
            skCircle(sketch, "E3.0.17.15", {"center": v(431.8, 381) * mm, "radius": 2.38 * mm});
            skCircle(sketch, "E3.0.17.16", {"center": v(431.8, 406.4) * mm, "radius": 2.38 * mm});
            skCircle(sketch, "E3.0.17.17", {"center": v(431.8, 431.8) * mm, "radius": 2.38 * mm});
            skCircle(sketch, "E3.0.17.18", {"center": v(431.8, 457.2) * mm, "radius": 2.38 * mm});
            skCircle(sketch, "E3.0.17.19", {"center": v(431.8, 482.6) * mm, "radius": 2.38 * mm});
            skCircle(sketch, "E3.0.17.20", {"center": v(431.8, 508) * mm, "radius": 2.38 * mm});
            skCircle(sketch, "E3.0.17.21", {"center": v(431.8, 533.4) * mm, "radius": 2.38 * mm});
            skCircle(sketch, "E3.0.17.22", {"center": v(431.8, 558.8) * mm, "radius": 2.38 * mm});
            skCircle(sketch, "E3.0.18.0", {"center": v(457.2, 0) * mm, "radius": 2.38 * mm});
            skCircle(sketch, "E3.0.18.1", {"center": v(457.2, 25.4) * mm, "radius": 2.38 * mm});
            skCircle(sketch, "E3.0.18.2", {"center": v(457.2, 50.8) * mm, "radius": 2.38 * mm});
            skCircle(sketch, "E3.0.18.3", {"center": v(457.2, 76.2) * mm, "radius": 2.38 * mm});
            skCircle(sketch, "E3.0.18.4", {"center": v(457.2, 101.6) * mm, "radius": 2.38 * mm});
            skCircle(sketch, "E3.0.18.5", {"center": v(457.2, 127) * mm, "radius": 2.38 * mm});
            skCircle(sketch, "E3.0.18.6", {"center": v(457.2, 152.4) * mm, "radius": 2.38 * mm});
            skCircle(sketch, "E3.0.18.7", {"center": v(457.2, 177.8) * mm, "radius": 2.38 * mm});
            skCircle(sketch, "E3.0.18.8", {"center": v(457.2, 203.2) * mm, "radius": 2.38 * mm});
            skCircle(sketch, "E3.0.18.9", {"center": v(457.2, 228.6) * mm, "radius": 2.38 * mm});
            skCircle(sketch, "E3.0.18.10", {"center": v(457.2, 254) * mm, "radius": 2.38 * mm});
            skCircle(sketch, "E3.0.18.11", {"center": v(457.2, 279.4) * mm, "radius": 2.38 * mm});
            skCircle(sketch, "E3.0.18.12", {"center": v(457.2, 304.8) * mm, "radius": 2.38 * mm});
            skCircle(sketch, "E3.0.18.13", {"center": v(457.2, 330.2) * mm, "radius": 2.38 * mm});
            skCircle(sketch, "E3.0.18.14", {"center": v(457.2, 355.6) * mm, "radius": 2.38 * mm});
            skCircle(sketch, "E3.0.18.15", {"center": v(457.2, 381) * mm, "radius": 2.38 * mm});
            skCircle(sketch, "E3.0.18.16", {"center": v(457.2, 406.4) * mm, "radius": 2.38 * mm});
            skCircle(sketch, "E3.0.18.17", {"center": v(457.2, 431.8) * mm, "radius": 2.38 * mm});
            skCircle(sketch, "E3.0.18.18", {"center": v(457.2, 457.2) * mm, "radius": 2.38 * mm});
            skCircle(sketch, "E3.0.18.19", {"center": v(457.2, 482.6) * mm, "radius": 2.38 * mm});
            skCircle(sketch, "E3.0.18.20", {"center": v(457.2, 508) * mm, "radius": 2.38 * mm});
            skCircle(sketch, "E3.0.18.21", {"center": v(457.2, 533.4) * mm, "radius": 2.38 * mm});
            skCircle(sketch, "E3.0.18.22", {"center": v(457.2, 558.8) * mm, "radius": 2.38 * mm});
            skCircle(sketch, "E3.0.19.0", {"center": v(482.6, 0) * mm, "radius": 2.38 * mm});
            skCircle(sketch, "E3.0.19.1", {"center": v(482.6, 25.4) * mm, "radius": 2.38 * mm});
            skCircle(sketch, "E3.0.19.2", {"center": v(482.6, 50.8) * mm, "radius": 2.38 * mm});
            skCircle(sketch, "E3.0.19.3", {"center": v(482.6, 76.2) * mm, "radius": 2.38 * mm});
            skCircle(sketch, "E3.0.19.4", {"center": v(482.6, 101.6) * mm, "radius": 2.38 * mm});
            skCircle(sketch, "E3.0.19.5", {"center": v(482.6, 127) * mm, "radius": 2.38 * mm});
            skCircle(sketch, "E3.0.19.6", {"center": v(482.6, 152.4) * mm, "radius": 2.38 * mm});
            skCircle(sketch, "E3.0.19.7", {"center": v(482.6, 177.8) * mm, "radius": 2.38 * mm});
            skCircle(sketch, "E3.0.19.8", {"center": v(482.6, 203.2) * mm, "radius": 2.38 * mm});
            skCircle(sketch, "E3.0.19.9", {"center": v(482.6, 228.6) * mm, "radius": 2.38 * mm});
            skCircle(sketch, "E3.0.19.10", {"center": v(482.6, 254) * mm, "radius": 2.38 * mm});
            skCircle(sketch, "E3.0.19.11", {"center": v(482.6, 279.4) * mm, "radius": 2.38 * mm});
            skCircle(sketch, "E3.0.19.12", {"center": v(482.6, 304.8) * mm, "radius": 2.38 * mm});
            skCircle(sketch, "E3.0.19.13", {"center": v(482.6, 330.2) * mm, "radius": 2.38 * mm});
            skCircle(sketch, "E3.0.19.14", {"center": v(482.6, 355.6) * mm, "radius": 2.38 * mm});
            skCircle(sketch, "E3.0.19.15", {"center": v(482.6, 381) * mm, "radius": 2.38 * mm});
            skCircle(sketch, "E3.0.19.16", {"center": v(482.6, 406.4) * mm, "radius": 2.38 * mm});
            skCircle(sketch, "E3.0.19.17", {"center": v(482.6, 431.8) * mm, "radius": 2.38 * mm});
            skCircle(sketch, "E3.0.19.18", {"center": v(482.6, 457.2) * mm, "radius": 2.38 * mm});
            skCircle(sketch, "E3.0.19.19", {"center": v(482.6, 482.6) * mm, "radius": 2.38 * mm});
            skCircle(sketch, "E3.0.19.20", {"center": v(482.6, 508) * mm, "radius": 2.38 * mm});
            skCircle(sketch, "E3.0.19.21", {"center": v(482.6, 533.4) * mm, "radius": 2.38 * mm});
            skCircle(sketch, "E3.0.19.22", {"center": v(482.6, 558.8) * mm, "radius": 2.38 * mm});
            skCircle(sketch, "E3.0.20.0", {"center": v(508, 0) * mm, "radius": 2.38 * mm});
            skCircle(sketch, "E3.0.20.1", {"center": v(508, 25.4) * mm, "radius": 2.38 * mm});
            skCircle(sketch, "E3.0.20.2", {"center": v(508, 50.8) * mm, "radius": 2.38 * mm});
            skCircle(sketch, "E3.0.20.3", {"center": v(508, 76.2) * mm, "radius": 2.38 * mm});
            skCircle(sketch, "E3.0.20.4", {"center": v(508, 101.6) * mm, "radius": 2.38 * mm});
            skCircle(sketch, "E3.0.20.5", {"center": v(508, 127) * mm, "radius": 2.38 * mm});
            skCircle(sketch, "E3.0.20.6", {"center": v(508, 152.4) * mm, "radius": 2.38 * mm});
            skCircle(sketch, "E3.0.20.7", {"center": v(508, 177.8) * mm, "radius": 2.38 * mm});
            skCircle(sketch, "E3.0.20.8", {"center": v(508, 203.2) * mm, "radius": 2.38 * mm});
            skCircle(sketch, "E3.0.20.9", {"center": v(508, 228.6) * mm, "radius": 2.38 * mm});
            skCircle(sketch, "E3.0.20.10", {"center": v(508, 254) * mm, "radius": 2.38 * mm});
            skCircle(sketch, "E3.0.20.11", {"center": v(508, 279.4) * mm, "radius": 2.38 * mm});
            skCircle(sketch, "E3.0.20.12", {"center": v(508, 304.8) * mm, "radius": 2.38 * mm});
            skCircle(sketch, "E3.0.20.13", {"center": v(508, 330.2) * mm, "radius": 2.38 * mm});
            skCircle(sketch, "E3.0.20.14", {"center": v(508, 355.6) * mm, "radius": 2.38 * mm});
            skCircle(sketch, "E3.0.20.15", {"center": v(508, 381) * mm, "radius": 2.38 * mm});
            skCircle(sketch, "E3.0.20.16", {"center": v(508, 406.4) * mm, "radius": 2.38 * mm});
            skCircle(sketch, "E3.0.20.17", {"center": v(508, 431.8) * mm, "radius": 2.38 * mm});
            skCircle(sketch, "E3.0.20.18", {"center": v(508, 457.2) * mm, "radius": 2.38 * mm});
            skCircle(sketch, "E3.0.20.19", {"center": v(508, 482.6) * mm, "radius": 2.38 * mm});
            skCircle(sketch, "E3.0.20.20", {"center": v(508, 508) * mm, "radius": 2.38 * mm});
            skCircle(sketch, "E3.0.20.21", {"center": v(508, 533.4) * mm, "radius": 2.38 * mm});
            skCircle(sketch, "E3.0.20.22", {"center": v(508, 558.8) * mm, "radius": 2.38 * mm});
            skCircle(sketch, "E3.0.21.0", {"center": v(533.4, 0) * mm, "radius": 2.38 * mm});
            skCircle(sketch, "E3.0.21.1", {"center": v(533.4, 25.4) * mm, "radius": 2.38 * mm});
            skCircle(sketch, "E3.0.21.2", {"center": v(533.4, 50.8) * mm, "radius": 2.38 * mm});
            skCircle(sketch, "E3.0.21.3", {"center": v(533.4, 76.2) * mm, "radius": 2.38 * mm});
            skCircle(sketch, "E3.0.21.4", {"center": v(533.4, 101.6) * mm, "radius": 2.38 * mm});
            skCircle(sketch, "E3.0.21.5", {"center": v(533.4, 127) * mm, "radius": 2.38 * mm});
            skCircle(sketch, "E3.0.21.6", {"center": v(533.4, 152.4) * mm, "radius": 2.38 * mm});
            skCircle(sketch, "E3.0.21.7", {"center": v(533.4, 177.8) * mm, "radius": 2.38 * mm});
            skCircle(sketch, "E3.0.21.8", {"center": v(533.4, 203.2) * mm, "radius": 2.38 * mm});
            skCircle(sketch, "E3.0.21.9", {"center": v(533.4, 228.6) * mm, "radius": 2.38 * mm});
            skCircle(sketch, "E3.0.21.10", {"center": v(533.4, 254) * mm, "radius": 2.38 * mm});
            skCircle(sketch, "E3.0.21.11", {"center": v(533.4, 279.4) * mm, "radius": 2.38 * mm});
            skCircle(sketch, "E3.0.21.12", {"center": v(533.4, 304.8) * mm, "radius": 2.38 * mm});
            skCircle(sketch, "E3.0.21.13", {"center": v(533.4, 330.2) * mm, "radius": 2.38 * mm});
            skCircle(sketch, "E3.0.21.14", {"center": v(533.4, 355.6) * mm, "radius": 2.38 * mm});
            skCircle(sketch, "E3.0.21.15", {"center": v(533.4, 381) * mm, "radius": 2.38 * mm});
            skCircle(sketch, "E3.0.21.16", {"center": v(533.4, 406.4) * mm, "radius": 2.38 * mm});
            skCircle(sketch, "E3.0.21.17", {"center": v(533.4, 431.8) * mm, "radius": 2.38 * mm});
            skCircle(sketch, "E3.0.21.18", {"center": v(533.4, 457.2) * mm, "radius": 2.38 * mm});
            skCircle(sketch, "E3.0.21.19", {"center": v(533.4, 482.6) * mm, "radius": 2.38 * mm});
            skCircle(sketch, "E3.0.21.20", {"center": v(533.4, 508) * mm, "radius": 2.38 * mm});
            skCircle(sketch, "E3.0.21.21", {"center": v(533.4, 533.4) * mm, "radius": 2.38 * mm});
            skCircle(sketch, "E3.0.21.22", {"center": v(533.4, 558.8) * mm, "radius": 2.38 * mm});
            skCircle(sketch, "E3.0.22.0", {"center": v(558.8, 0) * mm, "radius": 2.38 * mm});
            skCircle(sketch, "E3.0.22.1", {"center": v(558.8, 25.4) * mm, "radius": 2.38 * mm});
            skCircle(sketch, "E3.0.22.2", {"center": v(558.8, 50.8) * mm, "radius": 2.38 * mm});
            skCircle(sketch, "E3.0.22.3", {"center": v(558.8, 76.2) * mm, "radius": 2.38 * mm});
            skCircle(sketch, "E3.0.22.4", {"center": v(558.8, 101.6) * mm, "radius": 2.38 * mm});
            skCircle(sketch, "E3.0.22.5", {"center": v(558.8, 127) * mm, "radius": 2.38 * mm});
            skCircle(sketch, "E3.0.22.6", {"center": v(558.8, 152.4) * mm, "radius": 2.38 * mm});
            skCircle(sketch, "E3.0.22.7", {"center": v(558.8, 177.8) * mm, "radius": 2.38 * mm});
            skCircle(sketch, "E3.0.22.8", {"center": v(558.8, 203.2) * mm, "radius": 2.38 * mm});
            skCircle(sketch, "E3.0.22.9", {"center": v(558.8, 228.6) * mm, "radius": 2.38 * mm});
            skCircle(sketch, "E3.0.22.10", {"center": v(558.8, 254) * mm, "radius": 2.38 * mm});
            skCircle(sketch, "E3.0.22.11", {"center": v(558.8, 279.4) * mm, "radius": 2.38 * mm});
            skCircle(sketch, "E3.0.22.12", {"center": v(558.8, 304.8) * mm, "radius": 2.38 * mm});
            skCircle(sketch, "E3.0.22.13", {"center": v(558.8, 330.2) * mm, "radius": 2.38 * mm});
            skCircle(sketch, "E3.0.22.14", {"center": v(558.8, 355.6) * mm, "radius": 2.38 * mm});
            skCircle(sketch, "E3.0.22.15", {"center": v(558.8, 381) * mm, "radius": 2.38 * mm});
            skCircle(sketch, "E3.0.22.16", {"center": v(558.8, 406.4) * mm, "radius": 2.38 * mm});
            skCircle(sketch, "E3.0.22.17", {"center": v(558.8, 431.8) * mm, "radius": 2.38 * mm});
            skCircle(sketch, "E3.0.22.18", {"center": v(558.8, 457.2) * mm, "radius": 2.38 * mm});
            skCircle(sketch, "E3.0.22.19", {"center": v(558.8, 482.6) * mm, "radius": 2.38 * mm});
            skCircle(sketch, "E3.0.22.20", {"center": v(558.8, 508) * mm, "radius": 2.38 * mm});
            skCircle(sketch, "E3.0.22.21", {"center": v(558.8, 533.4) * mm, "radius": 2.38 * mm});
            skCircle(sketch, "E3.0.22.22", {"center": v(558.8, 558.8) * mm, "radius": 2.38 * mm});
            skLineSegment(sketch, "E4.bottom", {"start": v(0, 592.67) * mm, "end": v(584.2, 592.67) * mm});
            skLineSegment(sketch, "E4.top", {"start": v(0, -8.47) * mm, "end": v(584.2, -8.47) * mm});
            skLineSegment(sketch, "E4.left", {"start": v(-8.47, 584.2) * mm, "end": v(-8.47, 0) * mm});
            skLineSegment(sketch, "E4.right", {"start": v(592.67, 584.2) * mm, "end": v(592.67, 0) * mm});
            skPoint(sketch, "E5.visualSharp", {"position": v(-8.47, -8.47) * mm});
            skArc(sketch, "E5.filletArc", {"start": v(-8.47, 0) * mm, "mid": v(-5.99, -5.99) * mm, "end": v(0, -8.47) * mm});
            skArc(sketch, "E6.filletArc", {"start": v(0, 592.67) * mm, "mid": v(-5.99, 590.19) * mm, "end": v(-8.47, 584.2) * mm});
            skArc(sketch, "E7.filletArc", {"start": v(592.67, 584.2) * mm, "mid": v(590.19, 590.19) * mm, "end": v(584.2, 592.67) * mm});
            skArc(sketch, "E8.filletArc", {"start": v(584.2, -8.47) * mm, "mid": v(590.19, -5.99) * mm, "end": v(592.67, 0) * mm});
            skCircle(sketch, "E9.0.23.0", {"center": v(584.2, 0) * mm, "radius": 2.38 * mm});
            skCircle(sketch, "E9.0.23.1", {"center": v(584.2, 25.4) * mm, "radius": 2.38 * mm});
            skCircle(sketch, "E9.0.23.2", {"center": v(584.2, 50.8) * mm, "radius": 2.38 * mm});
            skCircle(sketch, "E9.0.23.3", {"center": v(584.2, 76.2) * mm, "radius": 2.38 * mm});
            skCircle(sketch, "E9.0.23.4", {"center": v(584.2, 101.6) * mm, "radius": 2.38 * mm});
            skCircle(sketch, "E9.0.23.5", {"center": v(584.2, 127) * mm, "radius": 2.38 * mm});
            skCircle(sketch, "E9.0.23.6", {"center": v(584.2, 152.4) * mm, "radius": 2.38 * mm});
            skCircle(sketch, "E9.0.23.7", {"center": v(584.2, 177.8) * mm, "radius": 2.38 * mm});
            skCircle(sketch, "E9.0.23.8", {"center": v(584.2, 203.2) * mm, "radius": 2.38 * mm});
            skCircle(sketch, "E9.0.23.9", {"center": v(584.2, 228.6) * mm, "radius": 2.38 * mm});
            skCircle(sketch, "E9.0.23.10", {"center": v(584.2, 254) * mm, "radius": 2.38 * mm});
            skCircle(sketch, "E9.0.23.11", {"center": v(584.2, 279.4) * mm, "radius": 2.38 * mm});
            skCircle(sketch, "E9.0.23.12", {"center": v(584.2, 304.8) * mm, "radius": 2.38 * mm});
            skCircle(sketch, "E9.0.23.13", {"center": v(584.2, 330.2) * mm, "radius": 2.38 * mm});
            skCircle(sketch, "E9.0.23.14", {"center": v(584.2, 355.6) * mm, "radius": 2.38 * mm});
            skCircle(sketch, "E9.0.23.15", {"center": v(584.2, 381) * mm, "radius": 2.38 * mm});
            skCircle(sketch, "E9.0.23.16", {"center": v(584.2, 406.4) * mm, "radius": 2.38 * mm});
            skCircle(sketch, "E9.0.23.17", {"center": v(584.2, 431.8) * mm, "radius": 2.38 * mm});
            skCircle(sketch, "E9.0.23.18", {"center": v(584.2, 457.2) * mm, "radius": 2.38 * mm});
            skCircle(sketch, "E9.0.23.19", {"center": v(584.2, 482.6) * mm, "radius": 2.38 * mm});
            skCircle(sketch, "E9.0.23.20", {"center": v(584.2, 508) * mm, "radius": 2.38 * mm});
            skCircle(sketch, "E9.0.23.21", {"center": v(584.2, 533.4) * mm, "radius": 2.38 * mm});
            skCircle(sketch, "E9.0.23.22", {"center": v(584.2, 558.8) * mm, "radius": 2.38 * mm});
            skCircle(sketch, "E10.0.0.23", {"center": v(0, 584.2) * mm, "radius": 2.38 * mm});
            skCircle(sketch, "E10.0.1.23", {"center": v(25.4, 584.2) * mm, "radius": 2.38 * mm});
            skCircle(sketch, "E10.0.2.23", {"center": v(50.8, 584.2) * mm, "radius": 2.38 * mm});
            skCircle(sketch, "E10.0.3.23", {"center": v(76.2, 584.2) * mm, "radius": 2.38 * mm});
            skCircle(sketch, "E10.0.4.23", {"center": v(101.6, 584.2) * mm, "radius": 2.38 * mm});
            skCircle(sketch, "E10.0.5.23", {"center": v(127, 584.2) * mm, "radius": 2.38 * mm});
            skCircle(sketch, "E10.0.6.23", {"center": v(152.4, 584.2) * mm, "radius": 2.38 * mm});
            skCircle(sketch, "E10.0.7.23", {"center": v(177.8, 584.2) * mm, "radius": 2.38 * mm});
            skCircle(sketch, "E10.0.8.23", {"center": v(203.2, 584.2) * mm, "radius": 2.38 * mm});
            skCircle(sketch, "E10.0.9.23", {"center": v(228.6, 584.2) * mm, "radius": 2.38 * mm});
            skCircle(sketch, "E10.0.10.23", {"center": v(254, 584.2) * mm, "radius": 2.38 * mm});
            skCircle(sketch, "E10.0.11.23", {"center": v(279.4, 584.2) * mm, "radius": 2.38 * mm});
            skCircle(sketch, "E10.0.12.23", {"center": v(304.8, 584.2) * mm, "radius": 2.38 * mm});
            skCircle(sketch, "E10.0.13.23", {"center": v(330.2, 584.2) * mm, "radius": 2.38 * mm});
            skCircle(sketch, "E10.0.14.23", {"center": v(355.6, 584.2) * mm, "radius": 2.38 * mm});
            skCircle(sketch, "E10.0.15.23", {"center": v(381, 584.2) * mm, "radius": 2.38 * mm});
            skCircle(sketch, "E10.0.16.23", {"center": v(406.4, 584.2) * mm, "radius": 2.38 * mm});
            skCircle(sketch, "E10.0.17.23", {"center": v(431.8, 584.2) * mm, "radius": 2.38 * mm});
            skCircle(sketch, "E10.0.18.23", {"center": v(457.2, 584.2) * mm, "radius": 2.38 * mm});
            skCircle(sketch, "E10.0.19.23", {"center": v(482.6, 584.2) * mm, "radius": 2.38 * mm});
            skCircle(sketch, "E10.0.20.23", {"center": v(508, 584.2) * mm, "radius": 2.38 * mm});
            skCircle(sketch, "E10.0.21.23", {"center": v(533.4, 584.2) * mm, "radius": 2.38 * mm});
            skCircle(sketch, "E10.0.22.23", {"center": v(558.8, 584.2) * mm, "radius": 2.38 * mm});
            skCircle(sketch, "E10.0.23.23", {"center": v(584.2, 584.2) * mm, "radius": 2.38 * mm});
            skSolve(sketch);
        }
        {
            var Q0;
            Q0=qCreatedBy(makeId("Right.planeOp"),FACE);
            var sketch = newSketch(context, id + "F2", { "sketchPlane" : qUnion([Q0])});
            skLineSegment(sketch, "E11.bottom", {"start": v(-12.7, 0) * mm, "end": v(12.7, 0) * mm});
            skLineSegment(sketch, "E11.top", {"start": v(-12.7, -3.17) * mm, "end": v(12.7, -3.17) * mm});
            skLineSegment(sketch, "E11.left", {"start": v(-12.7, 0) * mm, "end": v(-12.7, -3.17) * mm});
            skLineSegment(sketch, "E11.right", {"start": v(12.7, 0) * mm, "end": v(12.7, -3.17) * mm});
            skSolve(sketch);
        }
        {
            var Q0;
            Q0=qCreatedBy(makeId("Top.planeOp"),FACE);
            var sketch = newSketch(context, id + "F3", { "sketchPlane" : qUnion([Q0])});
            skCircle(sketch, "E12.0", {"center": v(0, 0) * mm, "radius": 2.38 * mm});
            skArc(sketch, "E12.1", {"start": v(-8.47, 0) * mm, "mid": v(-5.99, -5.99) * mm, "end": v(0, -8.47) * mm});
            skCircle(sketch, "E13", {"center": v(0, 0) * mm, "radius": 8.47 * mm, "construction": true});
            skCircle(sketch, "E14.0.1.0", {"center": v(0, 25.4) * mm, "radius": 8.47 * mm, "construction": true});
            skCircle(sketch, "E14.0.1.1", {"center": v(0, 25.4) * mm, "radius": 2.38 * mm});
            skCircle(sketch, "E14.0.2.0", {"center": v(0, 50.8) * mm, "radius": 8.47 * mm, "construction": true});
            skCircle(sketch, "E14.0.2.1", {"center": v(0, 50.8) * mm, "radius": 2.38 * mm});
            skCircle(sketch, "E14.0.3.0", {"center": v(0, 76.2) * mm, "radius": 8.47 * mm, "construction": true});
            skCircle(sketch, "E14.0.3.1", {"center": v(0, 76.2) * mm, "radius": 2.38 * mm});
            skCircle(sketch, "E14.0.4.0", {"center": v(0, 101.6) * mm, "radius": 8.47 * mm, "construction": true});
            skCircle(sketch, "E14.0.4.1", {"center": v(0, 101.6) * mm, "radius": 2.38 * mm});
            skCircle(sketch, "E14.0.5.0", {"center": v(0, 127) * mm, "radius": 8.47 * mm, "construction": true});
            skCircle(sketch, "E14.0.5.1", {"center": v(0, 127) * mm, "radius": 2.38 * mm});
            skCircle(sketch, "E14.0.6.0", {"center": v(0, 152.4) * mm, "radius": 8.47 * mm, "construction": true});
            skCircle(sketch, "E14.0.6.1", {"center": v(0, 152.4) * mm, "radius": 2.38 * mm});
            skCircle(sketch, "E14.0.7.0", {"center": v(0, 177.8) * mm, "radius": 8.47 * mm, "construction": true});
            skCircle(sketch, "E14.0.7.1", {"center": v(0, 177.8) * mm, "radius": 2.38 * mm});
            skCircle(sketch, "E14.0.8.0", {"center": v(0, 203.2) * mm, "radius": 8.47 * mm, "construction": true});
            skCircle(sketch, "E14.0.8.1", {"center": v(0, 203.2) * mm, "radius": 2.38 * mm});
            skCircle(sketch, "E14.0.9.0", {"center": v(0, 228.6) * mm, "radius": 8.47 * mm, "construction": true});
            skCircle(sketch, "E14.0.9.1", {"center": v(0, 228.6) * mm, "radius": 2.38 * mm});
            skCircle(sketch, "E14.0.10.0", {"center": v(0, 254) * mm, "radius": 8.47 * mm, "construction": true});
            skCircle(sketch, "E14.0.10.1", {"center": v(0, 254) * mm, "radius": 2.38 * mm});
            skCircle(sketch, "E14.0.11.0", {"center": v(0, 279.4) * mm, "radius": 8.47 * mm, "construction": true});
            skCircle(sketch, "E14.0.11.1", {"center": v(0, 279.4) * mm, "radius": 2.38 * mm});
            skCircle(sketch, "E14.0.12.0", {"center": v(0, 304.8) * mm, "radius": 8.47 * mm, "construction": true});
            skCircle(sketch, "E14.0.12.1", {"center": v(0, 304.8) * mm, "radius": 2.38 * mm});
            skCircle(sketch, "E14.0.13.0", {"center": v(0, 330.2) * mm, "radius": 8.47 * mm, "construction": true});
            skCircle(sketch, "E14.0.13.1", {"center": v(0, 330.2) * mm, "radius": 2.38 * mm});
            skCircle(sketch, "E14.0.14.0", {"center": v(0, 355.6) * mm, "radius": 8.47 * mm, "construction": true});
            skCircle(sketch, "E14.0.14.1", {"center": v(0, 355.6) * mm, "radius": 2.38 * mm});
            skCircle(sketch, "E14.0.15.0", {"center": v(0, 381) * mm, "radius": 8.47 * mm, "construction": true});
            skCircle(sketch, "E14.0.15.1", {"center": v(0, 381) * mm, "radius": 2.38 * mm});
            skCircle(sketch, "E14.1.0.0", {"center": v(25.4, 0) * mm, "radius": 8.47 * mm, "construction": true});
            skCircle(sketch, "E14.1.0.1", {"center": v(25.4, 0) * mm, "radius": 2.38 * mm});
            skCircle(sketch, "E14.1.1.0", {"center": v(25.4, 25.4) * mm, "radius": 8.47 * mm, "construction": true});
            skCircle(sketch, "E14.1.1.1", {"center": v(25.4, 25.4) * mm, "radius": 2.38 * mm});
            skCircle(sketch, "E14.1.2.0", {"center": v(25.4, 50.8) * mm, "radius": 8.47 * mm, "construction": true});
            skCircle(sketch, "E14.1.2.1", {"center": v(25.4, 50.8) * mm, "radius": 2.38 * mm});
            skCircle(sketch, "E14.1.3.0", {"center": v(25.4, 76.2) * mm, "radius": 8.47 * mm, "construction": true});
            skCircle(sketch, "E14.1.3.1", {"center": v(25.4, 76.2) * mm, "radius": 2.38 * mm});
            skCircle(sketch, "E14.1.4.0", {"center": v(25.4, 101.6) * mm, "radius": 8.47 * mm, "construction": true});
            skCircle(sketch, "E14.1.4.1", {"center": v(25.4, 101.6) * mm, "radius": 2.38 * mm});
            skCircle(sketch, "E14.1.5.0", {"center": v(25.4, 127) * mm, "radius": 8.47 * mm, "construction": true});
            skCircle(sketch, "E14.1.5.1", {"center": v(25.4, 127) * mm, "radius": 2.38 * mm});
            skCircle(sketch, "E14.1.6.0", {"center": v(25.4, 152.4) * mm, "radius": 8.47 * mm, "construction": true});
            skCircle(sketch, "E14.1.6.1", {"center": v(25.4, 152.4) * mm, "radius": 2.38 * mm});
            skCircle(sketch, "E14.1.7.0", {"center": v(25.4, 177.8) * mm, "radius": 8.47 * mm, "construction": true});
            skCircle(sketch, "E14.1.7.1", {"center": v(25.4, 177.8) * mm, "radius": 2.38 * mm});
            skCircle(sketch, "E14.1.8.0", {"center": v(25.4, 203.2) * mm, "radius": 8.47 * mm, "construction": true});
            skCircle(sketch, "E14.1.8.1", {"center": v(25.4, 203.2) * mm, "radius": 2.38 * mm});
            skCircle(sketch, "E14.1.9.0", {"center": v(25.4, 228.6) * mm, "radius": 8.47 * mm, "construction": true});
            skCircle(sketch, "E14.1.9.1", {"center": v(25.4, 228.6) * mm, "radius": 2.38 * mm});
            skCircle(sketch, "E14.1.10.0", {"center": v(25.4, 254) * mm, "radius": 8.47 * mm, "construction": true});
            skCircle(sketch, "E14.1.10.1", {"center": v(25.4, 254) * mm, "radius": 2.38 * mm});
            skCircle(sketch, "E14.1.11.0", {"center": v(25.4, 279.4) * mm, "radius": 8.47 * mm, "construction": true});
            skCircle(sketch, "E14.1.11.1", {"center": v(25.4, 279.4) * mm, "radius": 2.38 * mm});
            skCircle(sketch, "E14.1.12.0", {"center": v(25.4, 304.8) * mm, "radius": 8.47 * mm, "construction": true});
            skCircle(sketch, "E14.1.12.1", {"center": v(25.4, 304.8) * mm, "radius": 2.38 * mm});
            skCircle(sketch, "E14.1.13.0", {"center": v(25.4, 330.2) * mm, "radius": 8.47 * mm, "construction": true});
            skCircle(sketch, "E14.1.13.1", {"center": v(25.4, 330.2) * mm, "radius": 2.38 * mm});
            skCircle(sketch, "E14.1.14.0", {"center": v(25.4, 355.6) * mm, "radius": 8.47 * mm, "construction": true});
            skCircle(sketch, "E14.1.14.1", {"center": v(25.4, 355.6) * mm, "radius": 2.38 * mm});
            skCircle(sketch, "E14.1.15.0", {"center": v(25.4, 381) * mm, "radius": 8.47 * mm, "construction": true});
            skCircle(sketch, "E14.1.15.1", {"center": v(25.4, 381) * mm, "radius": 2.38 * mm});
            skCircle(sketch, "E14.2.0.0", {"center": v(50.8, 0) * mm, "radius": 8.47 * mm, "construction": true});
            skCircle(sketch, "E14.2.0.1", {"center": v(50.8, 0) * mm, "radius": 2.38 * mm});
            skCircle(sketch, "E14.2.1.0", {"center": v(50.8, 25.4) * mm, "radius": 8.47 * mm, "construction": true});
            skCircle(sketch, "E14.2.1.1", {"center": v(50.8, 25.4) * mm, "radius": 2.38 * mm});
            skCircle(sketch, "E14.2.2.0", {"center": v(50.8, 50.8) * mm, "radius": 8.47 * mm, "construction": true});
            skCircle(sketch, "E14.2.2.1", {"center": v(50.8, 50.8) * mm, "radius": 2.38 * mm});
            skCircle(sketch, "E14.2.3.0", {"center": v(50.8, 76.2) * mm, "radius": 8.47 * mm, "construction": true});
            skCircle(sketch, "E14.2.3.1", {"center": v(50.8, 76.2) * mm, "radius": 2.38 * mm});
            skCircle(sketch, "E14.2.4.0", {"center": v(50.8, 101.6) * mm, "radius": 8.47 * mm, "construction": true});
            skCircle(sketch, "E14.2.4.1", {"center": v(50.8, 101.6) * mm, "radius": 2.38 * mm});
            skCircle(sketch, "E14.2.5.0", {"center": v(50.8, 127) * mm, "radius": 8.47 * mm, "construction": true});
            skCircle(sketch, "E14.2.5.1", {"center": v(50.8, 127) * mm, "radius": 2.38 * mm});
            skCircle(sketch, "E14.2.6.0", {"center": v(50.8, 152.4) * mm, "radius": 8.47 * mm, "construction": true});
            skCircle(sketch, "E14.2.6.1", {"center": v(50.8, 152.4) * mm, "radius": 2.38 * mm});
            skCircle(sketch, "E14.2.7.0", {"center": v(50.8, 177.8) * mm, "radius": 8.47 * mm, "construction": true});
            skCircle(sketch, "E14.2.7.1", {"center": v(50.8, 177.8) * mm, "radius": 2.38 * mm});
            skCircle(sketch, "E14.2.8.0", {"center": v(50.8, 203.2) * mm, "radius": 8.47 * mm, "construction": true});
            skCircle(sketch, "E14.2.8.1", {"center": v(50.8, 203.2) * mm, "radius": 2.38 * mm});
            skCircle(sketch, "E14.2.9.0", {"center": v(50.8, 228.6) * mm, "radius": 8.47 * mm, "construction": true});
            skCircle(sketch, "E14.2.9.1", {"center": v(50.8, 228.6) * mm, "radius": 2.38 * mm});
            skCircle(sketch, "E14.2.10.0", {"center": v(50.8, 254) * mm, "radius": 8.47 * mm, "construction": true});
            skCircle(sketch, "E14.2.10.1", {"center": v(50.8, 254) * mm, "radius": 2.38 * mm});
            skCircle(sketch, "E14.2.11.0", {"center": v(50.8, 279.4) * mm, "radius": 8.47 * mm, "construction": true});
            skCircle(sketch, "E14.2.11.1", {"center": v(50.8, 279.4) * mm, "radius": 2.38 * mm});
            skCircle(sketch, "E14.2.12.0", {"center": v(50.8, 304.8) * mm, "radius": 8.47 * mm, "construction": true});
            skCircle(sketch, "E14.2.12.1", {"center": v(50.8, 304.8) * mm, "radius": 2.38 * mm});
            skCircle(sketch, "E14.2.13.0", {"center": v(50.8, 330.2) * mm, "radius": 8.47 * mm, "construction": true});
            skCircle(sketch, "E14.2.13.1", {"center": v(50.8, 330.2) * mm, "radius": 2.38 * mm});
            skCircle(sketch, "E14.2.14.0", {"center": v(50.8, 355.6) * mm, "radius": 8.47 * mm, "construction": true});
            skCircle(sketch, "E14.2.14.1", {"center": v(50.8, 355.6) * mm, "radius": 2.38 * mm});
            skCircle(sketch, "E14.2.15.0", {"center": v(50.8, 381) * mm, "radius": 8.47 * mm, "construction": true});
            skCircle(sketch, "E14.2.15.1", {"center": v(50.8, 381) * mm, "radius": 2.38 * mm});
            skCircle(sketch, "E14.3.0.0", {"center": v(76.2, 0) * mm, "radius": 8.47 * mm, "construction": true});
            skCircle(sketch, "E14.3.0.1", {"center": v(76.2, 0) * mm, "radius": 2.38 * mm});
            skCircle(sketch, "E14.3.1.0", {"center": v(76.2, 25.4) * mm, "radius": 8.47 * mm, "construction": true});
            skCircle(sketch, "E14.3.1.1", {"center": v(76.2, 25.4) * mm, "radius": 2.38 * mm});
            skCircle(sketch, "E14.3.2.0", {"center": v(76.2, 50.8) * mm, "radius": 8.47 * mm, "construction": true});
            skCircle(sketch, "E14.3.2.1", {"center": v(76.2, 50.8) * mm, "radius": 2.38 * mm});
            skCircle(sketch, "E14.3.3.0", {"center": v(76.2, 76.2) * mm, "radius": 8.47 * mm, "construction": true});
            skCircle(sketch, "E14.3.3.1", {"center": v(76.2, 76.2) * mm, "radius": 2.38 * mm});
            skCircle(sketch, "E14.3.4.0", {"center": v(76.2, 101.6) * mm, "radius": 8.47 * mm, "construction": true});
            skCircle(sketch, "E14.3.4.1", {"center": v(76.2, 101.6) * mm, "radius": 2.38 * mm});
            skCircle(sketch, "E14.3.5.0", {"center": v(76.2, 127) * mm, "radius": 8.47 * mm, "construction": true});
            skCircle(sketch, "E14.3.5.1", {"center": v(76.2, 127) * mm, "radius": 2.38 * mm});
            skCircle(sketch, "E14.3.6.0", {"center": v(76.2, 152.4) * mm, "radius": 8.47 * mm, "construction": true});
            skCircle(sketch, "E14.3.6.1", {"center": v(76.2, 152.4) * mm, "radius": 2.38 * mm});
            skCircle(sketch, "E14.3.7.0", {"center": v(76.2, 177.8) * mm, "radius": 8.47 * mm, "construction": true});
            skCircle(sketch, "E14.3.7.1", {"center": v(76.2, 177.8) * mm, "radius": 2.38 * mm});
            skCircle(sketch, "E14.3.8.0", {"center": v(76.2, 203.2) * mm, "radius": 8.47 * mm, "construction": true});
            skCircle(sketch, "E14.3.8.1", {"center": v(76.2, 203.2) * mm, "radius": 2.38 * mm});
            skCircle(sketch, "E14.3.9.0", {"center": v(76.2, 228.6) * mm, "radius": 8.47 * mm, "construction": true});
            skCircle(sketch, "E14.3.9.1", {"center": v(76.2, 228.6) * mm, "radius": 2.38 * mm});
            skCircle(sketch, "E14.3.10.0", {"center": v(76.2, 254) * mm, "radius": 8.47 * mm, "construction": true});
            skCircle(sketch, "E14.3.10.1", {"center": v(76.2, 254) * mm, "radius": 2.38 * mm});
            skCircle(sketch, "E14.3.11.0", {"center": v(76.2, 279.4) * mm, "radius": 8.47 * mm, "construction": true});
            skCircle(sketch, "E14.3.11.1", {"center": v(76.2, 279.4) * mm, "radius": 2.38 * mm});
            skCircle(sketch, "E14.3.12.0", {"center": v(76.2, 304.8) * mm, "radius": 8.47 * mm, "construction": true});
            skCircle(sketch, "E14.3.12.1", {"center": v(76.2, 304.8) * mm, "radius": 2.38 * mm});
            skCircle(sketch, "E14.3.13.0", {"center": v(76.2, 330.2) * mm, "radius": 8.47 * mm, "construction": true});
            skCircle(sketch, "E14.3.13.1", {"center": v(76.2, 330.2) * mm, "radius": 2.38 * mm});
            skCircle(sketch, "E14.3.14.0", {"center": v(76.2, 355.6) * mm, "radius": 8.47 * mm, "construction": true});
            skCircle(sketch, "E14.3.14.1", {"center": v(76.2, 355.6) * mm, "radius": 2.38 * mm});
            skCircle(sketch, "E14.3.15.0", {"center": v(76.2, 381) * mm, "radius": 8.47 * mm, "construction": true});
            skCircle(sketch, "E14.3.15.1", {"center": v(76.2, 381) * mm, "radius": 2.38 * mm});
            skCircle(sketch, "E14.4.0.0", {"center": v(101.6, 0) * mm, "radius": 8.47 * mm, "construction": true});
            skCircle(sketch, "E14.4.0.1", {"center": v(101.6, 0) * mm, "radius": 2.38 * mm});
            skCircle(sketch, "E14.4.1.0", {"center": v(101.6, 25.4) * mm, "radius": 8.47 * mm, "construction": true});
            skCircle(sketch, "E14.4.1.1", {"center": v(101.6, 25.4) * mm, "radius": 2.38 * mm});
            skCircle(sketch, "E14.4.2.0", {"center": v(101.6, 50.8) * mm, "radius": 8.47 * mm, "construction": true});
            skCircle(sketch, "E14.4.2.1", {"center": v(101.6, 50.8) * mm, "radius": 2.38 * mm});
            skCircle(sketch, "E14.4.3.0", {"center": v(101.6, 76.2) * mm, "radius": 8.47 * mm, "construction": true});
            skCircle(sketch, "E14.4.3.1", {"center": v(101.6, 76.2) * mm, "radius": 2.38 * mm});
            skCircle(sketch, "E14.4.4.0", {"center": v(101.6, 101.6) * mm, "radius": 8.47 * mm, "construction": true});
            skCircle(sketch, "E14.4.4.1", {"center": v(101.6, 101.6) * mm, "radius": 2.38 * mm});
            skCircle(sketch, "E14.4.5.0", {"center": v(101.6, 127) * mm, "radius": 8.47 * mm, "construction": true});
            skCircle(sketch, "E14.4.5.1", {"center": v(101.6, 127) * mm, "radius": 2.38 * mm});
            skCircle(sketch, "E14.4.6.0", {"center": v(101.6, 152.4) * mm, "radius": 8.47 * mm, "construction": true});
            skCircle(sketch, "E14.4.6.1", {"center": v(101.6, 152.4) * mm, "radius": 2.38 * mm});
            skCircle(sketch, "E14.4.7.0", {"center": v(101.6, 177.8) * mm, "radius": 8.47 * mm, "construction": true});
            skCircle(sketch, "E14.4.7.1", {"center": v(101.6, 177.8) * mm, "radius": 2.38 * mm});
            skCircle(sketch, "E14.4.8.0", {"center": v(101.6, 203.2) * mm, "radius": 8.47 * mm, "construction": true});
            skCircle(sketch, "E14.4.8.1", {"center": v(101.6, 203.2) * mm, "radius": 2.38 * mm});
            skCircle(sketch, "E14.4.9.0", {"center": v(101.6, 228.6) * mm, "radius": 8.47 * mm, "construction": true});
            skCircle(sketch, "E14.4.9.1", {"center": v(101.6, 228.6) * mm, "radius": 2.38 * mm});
            skCircle(sketch, "E14.4.10.0", {"center": v(101.6, 254) * mm, "radius": 8.47 * mm, "construction": true});
            skCircle(sketch, "E14.4.10.1", {"center": v(101.6, 254) * mm, "radius": 2.38 * mm});
            skCircle(sketch, "E14.4.11.0", {"center": v(101.6, 279.4) * mm, "radius": 8.47 * mm, "construction": true});
            skCircle(sketch, "E14.4.11.1", {"center": v(101.6, 279.4) * mm, "radius": 2.38 * mm});
            skCircle(sketch, "E14.4.12.0", {"center": v(101.6, 304.8) * mm, "radius": 8.47 * mm, "construction": true});
            skCircle(sketch, "E14.4.12.1", {"center": v(101.6, 304.8) * mm, "radius": 2.38 * mm});
            skCircle(sketch, "E14.4.13.0", {"center": v(101.6, 330.2) * mm, "radius": 8.47 * mm, "construction": true});
            skCircle(sketch, "E14.4.13.1", {"center": v(101.6, 330.2) * mm, "radius": 2.38 * mm});
            skCircle(sketch, "E14.4.14.0", {"center": v(101.6, 355.6) * mm, "radius": 8.47 * mm, "construction": true});
            skCircle(sketch, "E14.4.14.1", {"center": v(101.6, 355.6) * mm, "radius": 2.38 * mm});
            skCircle(sketch, "E14.4.15.0", {"center": v(101.6, 381) * mm, "radius": 8.47 * mm, "construction": true});
            skCircle(sketch, "E14.4.15.1", {"center": v(101.6, 381) * mm, "radius": 2.38 * mm});
            skCircle(sketch, "E14.5.0.0", {"center": v(127, 0) * mm, "radius": 8.47 * mm, "construction": true});
            skCircle(sketch, "E14.5.0.1", {"center": v(127, 0) * mm, "radius": 2.38 * mm});
            skCircle(sketch, "E14.5.1.0", {"center": v(127, 25.4) * mm, "radius": 8.47 * mm, "construction": true});
            skCircle(sketch, "E14.5.1.1", {"center": v(127, 25.4) * mm, "radius": 2.38 * mm});
            skCircle(sketch, "E14.5.2.0", {"center": v(127, 50.8) * mm, "radius": 8.47 * mm, "construction": true});
            skCircle(sketch, "E14.5.2.1", {"center": v(127, 50.8) * mm, "radius": 2.38 * mm});
            skCircle(sketch, "E14.5.3.0", {"center": v(127, 76.2) * mm, "radius": 8.47 * mm, "construction": true});
            skCircle(sketch, "E14.5.3.1", {"center": v(127, 76.2) * mm, "radius": 2.38 * mm});
            skCircle(sketch, "E14.5.4.0", {"center": v(127, 101.6) * mm, "radius": 8.47 * mm, "construction": true});
            skCircle(sketch, "E14.5.4.1", {"center": v(127, 101.6) * mm, "radius": 2.38 * mm});
            skCircle(sketch, "E14.5.5.0", {"center": v(127, 127) * mm, "radius": 8.47 * mm, "construction": true});
            skCircle(sketch, "E14.5.5.1", {"center": v(127, 127) * mm, "radius": 2.38 * mm});
            skCircle(sketch, "E14.5.6.0", {"center": v(127, 152.4) * mm, "radius": 8.47 * mm, "construction": true});
            skCircle(sketch, "E14.5.6.1", {"center": v(127, 152.4) * mm, "radius": 2.38 * mm});
            skCircle(sketch, "E14.5.7.0", {"center": v(127, 177.8) * mm, "radius": 8.47 * mm, "construction": true});
            skCircle(sketch, "E14.5.7.1", {"center": v(127, 177.8) * mm, "radius": 2.38 * mm});
            skCircle(sketch, "E14.5.8.0", {"center": v(127, 203.2) * mm, "radius": 8.47 * mm, "construction": true});
            skCircle(sketch, "E14.5.8.1", {"center": v(127, 203.2) * mm, "radius": 2.38 * mm});
            skCircle(sketch, "E14.5.9.0", {"center": v(127, 228.6) * mm, "radius": 8.47 * mm, "construction": true});
            skCircle(sketch, "E14.5.9.1", {"center": v(127, 228.6) * mm, "radius": 2.38 * mm});
            skCircle(sketch, "E14.5.10.0", {"center": v(127, 254) * mm, "radius": 8.47 * mm, "construction": true});
            skCircle(sketch, "E14.5.10.1", {"center": v(127, 254) * mm, "radius": 2.38 * mm});
            skCircle(sketch, "E14.5.11.0", {"center": v(127, 279.4) * mm, "radius": 8.47 * mm, "construction": true});
            skCircle(sketch, "E14.5.11.1", {"center": v(127, 279.4) * mm, "radius": 2.38 * mm});
            skCircle(sketch, "E14.5.12.0", {"center": v(127, 304.8) * mm, "radius": 8.47 * mm, "construction": true});
            skCircle(sketch, "E14.5.12.1", {"center": v(127, 304.8) * mm, "radius": 2.38 * mm});
            skCircle(sketch, "E14.5.13.0", {"center": v(127, 330.2) * mm, "radius": 8.47 * mm, "construction": true});
            skCircle(sketch, "E14.5.13.1", {"center": v(127, 330.2) * mm, "radius": 2.38 * mm});
            skCircle(sketch, "E14.5.14.0", {"center": v(127, 355.6) * mm, "radius": 8.47 * mm, "construction": true});
            skCircle(sketch, "E14.5.14.1", {"center": v(127, 355.6) * mm, "radius": 2.38 * mm});
            skCircle(sketch, "E14.5.15.0", {"center": v(127, 381) * mm, "radius": 8.47 * mm, "construction": true});
            skCircle(sketch, "E14.5.15.1", {"center": v(127, 381) * mm, "radius": 2.38 * mm});
            skCircle(sketch, "E14.6.0.0", {"center": v(152.4, 0) * mm, "radius": 8.47 * mm, "construction": true});
            skCircle(sketch, "E14.6.0.1", {"center": v(152.4, 0) * mm, "radius": 2.38 * mm});
            skCircle(sketch, "E14.6.1.0", {"center": v(152.4, 25.4) * mm, "radius": 8.47 * mm, "construction": true});
            skCircle(sketch, "E14.6.1.1", {"center": v(152.4, 25.4) * mm, "radius": 2.38 * mm});
            skCircle(sketch, "E14.6.2.0", {"center": v(152.4, 50.8) * mm, "radius": 8.47 * mm, "construction": true});
            skCircle(sketch, "E14.6.2.1", {"center": v(152.4, 50.8) * mm, "radius": 2.38 * mm});
            skCircle(sketch, "E14.6.3.0", {"center": v(152.4, 76.2) * mm, "radius": 8.47 * mm, "construction": true});
            skCircle(sketch, "E14.6.3.1", {"center": v(152.4, 76.2) * mm, "radius": 2.38 * mm});
            skCircle(sketch, "E14.6.4.0", {"center": v(152.4, 101.6) * mm, "radius": 8.47 * mm, "construction": true});
            skCircle(sketch, "E14.6.4.1", {"center": v(152.4, 101.6) * mm, "radius": 2.38 * mm});
            skCircle(sketch, "E14.6.5.0", {"center": v(152.4, 127) * mm, "radius": 8.47 * mm, "construction": true});
            skCircle(sketch, "E14.6.5.1", {"center": v(152.4, 127) * mm, "radius": 2.38 * mm});
            skCircle(sketch, "E14.6.6.0", {"center": v(152.4, 152.4) * mm, "radius": 8.47 * mm, "construction": true});
            skCircle(sketch, "E14.6.6.1", {"center": v(152.4, 152.4) * mm, "radius": 2.38 * mm});
            skCircle(sketch, "E14.6.7.0", {"center": v(152.4, 177.8) * mm, "radius": 8.47 * mm, "construction": true});
            skCircle(sketch, "E14.6.7.1", {"center": v(152.4, 177.8) * mm, "radius": 2.38 * mm});
            skCircle(sketch, "E14.6.8.0", {"center": v(152.4, 203.2) * mm, "radius": 8.47 * mm, "construction": true});
            skCircle(sketch, "E14.6.8.1", {"center": v(152.4, 203.2) * mm, "radius": 2.38 * mm});
            skCircle(sketch, "E14.6.9.0", {"center": v(152.4, 228.6) * mm, "radius": 8.47 * mm, "construction": true});
            skCircle(sketch, "E14.6.9.1", {"center": v(152.4, 228.6) * mm, "radius": 2.38 * mm});
            skCircle(sketch, "E14.6.10.0", {"center": v(152.4, 254) * mm, "radius": 8.47 * mm, "construction": true});
            skCircle(sketch, "E14.6.10.1", {"center": v(152.4, 254) * mm, "radius": 2.38 * mm});
            skCircle(sketch, "E14.6.11.0", {"center": v(152.4, 279.4) * mm, "radius": 8.47 * mm, "construction": true});
            skCircle(sketch, "E14.6.11.1", {"center": v(152.4, 279.4) * mm, "radius": 2.38 * mm});
            skCircle(sketch, "E14.6.12.0", {"center": v(152.4, 304.8) * mm, "radius": 8.47 * mm, "construction": true});
            skCircle(sketch, "E14.6.12.1", {"center": v(152.4, 304.8) * mm, "radius": 2.38 * mm});
            skCircle(sketch, "E14.6.13.0", {"center": v(152.4, 330.2) * mm, "radius": 8.47 * mm, "construction": true});
            skCircle(sketch, "E14.6.13.1", {"center": v(152.4, 330.2) * mm, "radius": 2.38 * mm});
            skCircle(sketch, "E14.6.14.0", {"center": v(152.4, 355.6) * mm, "radius": 8.47 * mm, "construction": true});
            skCircle(sketch, "E14.6.14.1", {"center": v(152.4, 355.6) * mm, "radius": 2.38 * mm});
            skCircle(sketch, "E14.6.15.0", {"center": v(152.4, 381) * mm, "radius": 8.47 * mm, "construction": true});
            skCircle(sketch, "E14.6.15.1", {"center": v(152.4, 381) * mm, "radius": 2.38 * mm});
            skCircle(sketch, "E14.7.0.0", {"center": v(177.8, 0) * mm, "radius": 8.47 * mm, "construction": true});
            skCircle(sketch, "E14.7.0.1", {"center": v(177.8, 0) * mm, "radius": 2.38 * mm});
            skCircle(sketch, "E14.7.1.0", {"center": v(177.8, 25.4) * mm, "radius": 8.47 * mm, "construction": true});
            skCircle(sketch, "E14.7.1.1", {"center": v(177.8, 25.4) * mm, "radius": 2.38 * mm});
            skCircle(sketch, "E14.7.2.0", {"center": v(177.8, 50.8) * mm, "radius": 8.47 * mm, "construction": true});
            skCircle(sketch, "E14.7.2.1", {"center": v(177.8, 50.8) * mm, "radius": 2.38 * mm});
            skCircle(sketch, "E14.7.3.0", {"center": v(177.8, 76.2) * mm, "radius": 8.47 * mm, "construction": true});
            skCircle(sketch, "E14.7.3.1", {"center": v(177.8, 76.2) * mm, "radius": 2.38 * mm});
            skCircle(sketch, "E14.7.4.0", {"center": v(177.8, 101.6) * mm, "radius": 8.47 * mm, "construction": true});
            skCircle(sketch, "E14.7.4.1", {"center": v(177.8, 101.6) * mm, "radius": 2.38 * mm});
            skCircle(sketch, "E14.7.5.0", {"center": v(177.8, 127) * mm, "radius": 8.47 * mm, "construction": true});
            skCircle(sketch, "E14.7.5.1", {"center": v(177.8, 127) * mm, "radius": 2.38 * mm});
            skCircle(sketch, "E14.7.6.0", {"center": v(177.8, 152.4) * mm, "radius": 8.47 * mm, "construction": true});
            skCircle(sketch, "E14.7.6.1", {"center": v(177.8, 152.4) * mm, "radius": 2.38 * mm});
            skCircle(sketch, "E14.7.7.0", {"center": v(177.8, 177.8) * mm, "radius": 8.47 * mm, "construction": true});
            skCircle(sketch, "E14.7.7.1", {"center": v(177.8, 177.8) * mm, "radius": 2.38 * mm});
            skCircle(sketch, "E14.7.8.0", {"center": v(177.8, 203.2) * mm, "radius": 8.47 * mm, "construction": true});
            skCircle(sketch, "E14.7.8.1", {"center": v(177.8, 203.2) * mm, "radius": 2.38 * mm});
            skCircle(sketch, "E14.7.9.0", {"center": v(177.8, 228.6) * mm, "radius": 8.47 * mm, "construction": true});
            skCircle(sketch, "E14.7.9.1", {"center": v(177.8, 228.6) * mm, "radius": 2.38 * mm});
            skCircle(sketch, "E14.7.10.0", {"center": v(177.8, 254) * mm, "radius": 8.47 * mm, "construction": true});
            skCircle(sketch, "E14.7.10.1", {"center": v(177.8, 254) * mm, "radius": 2.38 * mm});
            skCircle(sketch, "E14.7.11.0", {"center": v(177.8, 279.4) * mm, "radius": 8.47 * mm, "construction": true});
            skCircle(sketch, "E14.7.11.1", {"center": v(177.8, 279.4) * mm, "radius": 2.38 * mm});
            skCircle(sketch, "E14.7.12.0", {"center": v(177.8, 304.8) * mm, "radius": 8.47 * mm, "construction": true});
            skCircle(sketch, "E14.7.12.1", {"center": v(177.8, 304.8) * mm, "radius": 2.38 * mm});
            skCircle(sketch, "E14.7.13.0", {"center": v(177.8, 330.2) * mm, "radius": 8.47 * mm, "construction": true});
            skCircle(sketch, "E14.7.13.1", {"center": v(177.8, 330.2) * mm, "radius": 2.38 * mm});
            skCircle(sketch, "E14.7.14.0", {"center": v(177.8, 355.6) * mm, "radius": 8.47 * mm, "construction": true});
            skCircle(sketch, "E14.7.14.1", {"center": v(177.8, 355.6) * mm, "radius": 2.38 * mm});
            skCircle(sketch, "E14.7.15.0", {"center": v(177.8, 381) * mm, "radius": 8.47 * mm, "construction": true});
            skCircle(sketch, "E14.7.15.1", {"center": v(177.8, 381) * mm, "radius": 2.38 * mm});
            skCircle(sketch, "E14.8.0.0", {"center": v(203.2, 0) * mm, "radius": 8.47 * mm, "construction": true});
            skCircle(sketch, "E14.8.0.1", {"center": v(203.2, 0) * mm, "radius": 2.38 * mm});
            skCircle(sketch, "E14.8.1.0", {"center": v(203.2, 25.4) * mm, "radius": 8.47 * mm, "construction": true});
            skCircle(sketch, "E14.8.1.1", {"center": v(203.2, 25.4) * mm, "radius": 2.38 * mm});
            skCircle(sketch, "E14.8.2.0", {"center": v(203.2, 50.8) * mm, "radius": 8.47 * mm, "construction": true});
            skCircle(sketch, "E14.8.2.1", {"center": v(203.2, 50.8) * mm, "radius": 2.38 * mm});
            skCircle(sketch, "E14.8.3.0", {"center": v(203.2, 76.2) * mm, "radius": 8.47 * mm, "construction": true});
            skCircle(sketch, "E14.8.3.1", {"center": v(203.2, 76.2) * mm, "radius": 2.38 * mm});
            skCircle(sketch, "E14.8.4.0", {"center": v(203.2, 101.6) * mm, "radius": 8.47 * mm, "construction": true});
            skCircle(sketch, "E14.8.4.1", {"center": v(203.2, 101.6) * mm, "radius": 2.38 * mm});
            skCircle(sketch, "E14.8.5.0", {"center": v(203.2, 127) * mm, "radius": 8.47 * mm, "construction": true});
            skCircle(sketch, "E14.8.5.1", {"center": v(203.2, 127) * mm, "radius": 2.38 * mm});
            skCircle(sketch, "E14.8.6.0", {"center": v(203.2, 152.4) * mm, "radius": 8.47 * mm, "construction": true});
            skCircle(sketch, "E14.8.6.1", {"center": v(203.2, 152.4) * mm, "radius": 2.38 * mm});
            skCircle(sketch, "E14.8.7.0", {"center": v(203.2, 177.8) * mm, "radius": 8.47 * mm, "construction": true});
            skCircle(sketch, "E14.8.7.1", {"center": v(203.2, 177.8) * mm, "radius": 2.38 * mm});
            skCircle(sketch, "E14.8.8.0", {"center": v(203.2, 203.2) * mm, "radius": 8.47 * mm, "construction": true});
            skCircle(sketch, "E14.8.8.1", {"center": v(203.2, 203.2) * mm, "radius": 2.38 * mm});
            skCircle(sketch, "E14.8.9.0", {"center": v(203.2, 228.6) * mm, "radius": 8.47 * mm, "construction": true});
            skCircle(sketch, "E14.8.9.1", {"center": v(203.2, 228.6) * mm, "radius": 2.38 * mm});
            skCircle(sketch, "E14.8.10.0", {"center": v(203.2, 254) * mm, "radius": 8.47 * mm, "construction": true});
            skCircle(sketch, "E14.8.10.1", {"center": v(203.2, 254) * mm, "radius": 2.38 * mm});
            skCircle(sketch, "E14.8.11.0", {"center": v(203.2, 279.4) * mm, "radius": 8.47 * mm, "construction": true});
            skCircle(sketch, "E14.8.11.1", {"center": v(203.2, 279.4) * mm, "radius": 2.38 * mm});
            skCircle(sketch, "E14.8.12.0", {"center": v(203.2, 304.8) * mm, "radius": 8.47 * mm, "construction": true});
            skCircle(sketch, "E14.8.12.1", {"center": v(203.2, 304.8) * mm, "radius": 2.38 * mm});
            skCircle(sketch, "E14.8.13.0", {"center": v(203.2, 330.2) * mm, "radius": 8.47 * mm, "construction": true});
            skCircle(sketch, "E14.8.13.1", {"center": v(203.2, 330.2) * mm, "radius": 2.38 * mm});
            skCircle(sketch, "E14.8.14.0", {"center": v(203.2, 355.6) * mm, "radius": 8.47 * mm, "construction": true});
            skCircle(sketch, "E14.8.14.1", {"center": v(203.2, 355.6) * mm, "radius": 2.38 * mm});
            skCircle(sketch, "E14.8.15.0", {"center": v(203.2, 381) * mm, "radius": 8.47 * mm, "construction": true});
            skCircle(sketch, "E14.8.15.1", {"center": v(203.2, 381) * mm, "radius": 2.38 * mm});
            skCircle(sketch, "E14.9.0.0", {"center": v(228.6, 0) * mm, "radius": 8.47 * mm, "construction": true});
            skCircle(sketch, "E14.9.0.1", {"center": v(228.6, 0) * mm, "radius": 2.38 * mm});
            skCircle(sketch, "E14.9.1.0", {"center": v(228.6, 25.4) * mm, "radius": 8.47 * mm, "construction": true});
            skCircle(sketch, "E14.9.1.1", {"center": v(228.6, 25.4) * mm, "radius": 2.38 * mm});
            skCircle(sketch, "E14.9.2.0", {"center": v(228.6, 50.8) * mm, "radius": 8.47 * mm, "construction": true});
            skCircle(sketch, "E14.9.2.1", {"center": v(228.6, 50.8) * mm, "radius": 2.38 * mm});
            skCircle(sketch, "E14.9.3.0", {"center": v(228.6, 76.2) * mm, "radius": 8.47 * mm, "construction": true});
            skCircle(sketch, "E14.9.3.1", {"center": v(228.6, 76.2) * mm, "radius": 2.38 * mm});
            skCircle(sketch, "E14.9.4.0", {"center": v(228.6, 101.6) * mm, "radius": 8.47 * mm, "construction": true});
            skCircle(sketch, "E14.9.4.1", {"center": v(228.6, 101.6) * mm, "radius": 2.38 * mm});
            skCircle(sketch, "E14.9.5.0", {"center": v(228.6, 127) * mm, "radius": 8.47 * mm, "construction": true});
            skCircle(sketch, "E14.9.5.1", {"center": v(228.6, 127) * mm, "radius": 2.38 * mm});
            skCircle(sketch, "E14.9.6.0", {"center": v(228.6, 152.4) * mm, "radius": 8.47 * mm, "construction": true});
            skCircle(sketch, "E14.9.6.1", {"center": v(228.6, 152.4) * mm, "radius": 2.38 * mm});
            skCircle(sketch, "E14.9.7.0", {"center": v(228.6, 177.8) * mm, "radius": 8.47 * mm, "construction": true});
            skCircle(sketch, "E14.9.7.1", {"center": v(228.6, 177.8) * mm, "radius": 2.38 * mm});
            skCircle(sketch, "E14.9.8.0", {"center": v(228.6, 203.2) * mm, "radius": 8.47 * mm, "construction": true});
            skCircle(sketch, "E14.9.8.1", {"center": v(228.6, 203.2) * mm, "radius": 2.38 * mm});
            skCircle(sketch, "E14.9.9.0", {"center": v(228.6, 228.6) * mm, "radius": 8.47 * mm, "construction": true});
            skCircle(sketch, "E14.9.9.1", {"center": v(228.6, 228.6) * mm, "radius": 2.38 * mm});
            skCircle(sketch, "E14.9.10.0", {"center": v(228.6, 254) * mm, "radius": 8.47 * mm, "construction": true});
            skCircle(sketch, "E14.9.10.1", {"center": v(228.6, 254) * mm, "radius": 2.38 * mm});
            skCircle(sketch, "E14.9.11.0", {"center": v(228.6, 279.4) * mm, "radius": 8.47 * mm, "construction": true});
            skCircle(sketch, "E14.9.11.1", {"center": v(228.6, 279.4) * mm, "radius": 2.38 * mm});
            skCircle(sketch, "E14.9.12.0", {"center": v(228.6, 304.8) * mm, "radius": 8.47 * mm, "construction": true});
            skCircle(sketch, "E14.9.12.1", {"center": v(228.6, 304.8) * mm, "radius": 2.38 * mm});
            skCircle(sketch, "E14.9.13.0", {"center": v(228.6, 330.2) * mm, "radius": 8.47 * mm, "construction": true});
            skCircle(sketch, "E14.9.13.1", {"center": v(228.6, 330.2) * mm, "radius": 2.38 * mm});
            skCircle(sketch, "E14.9.14.0", {"center": v(228.6, 355.6) * mm, "radius": 8.47 * mm, "construction": true});
            skCircle(sketch, "E14.9.14.1", {"center": v(228.6, 355.6) * mm, "radius": 2.38 * mm});
            skCircle(sketch, "E14.9.15.0", {"center": v(228.6, 381) * mm, "radius": 8.47 * mm, "construction": true});
            skCircle(sketch, "E14.9.15.1", {"center": v(228.6, 381) * mm, "radius": 2.38 * mm});
            skCircle(sketch, "E14.10.0.0", {"center": v(254, 0) * mm, "radius": 8.47 * mm, "construction": true});
            skCircle(sketch, "E14.10.0.1", {"center": v(254, 0) * mm, "radius": 2.38 * mm});
            skCircle(sketch, "E14.10.1.0", {"center": v(254, 25.4) * mm, "radius": 8.47 * mm, "construction": true});
            skCircle(sketch, "E14.10.1.1", {"center": v(254, 25.4) * mm, "radius": 2.38 * mm});
            skCircle(sketch, "E14.10.2.0", {"center": v(254, 50.8) * mm, "radius": 8.47 * mm, "construction": true});
            skCircle(sketch, "E14.10.2.1", {"center": v(254, 50.8) * mm, "radius": 2.38 * mm});
            skCircle(sketch, "E14.10.3.0", {"center": v(254, 76.2) * mm, "radius": 8.47 * mm, "construction": true});
            skCircle(sketch, "E14.10.3.1", {"center": v(254, 76.2) * mm, "radius": 2.38 * mm});
            skCircle(sketch, "E14.10.4.0", {"center": v(254, 101.6) * mm, "radius": 8.47 * mm, "construction": true});
            skCircle(sketch, "E14.10.4.1", {"center": v(254, 101.6) * mm, "radius": 2.38 * mm});
            skCircle(sketch, "E14.10.5.0", {"center": v(254, 127) * mm, "radius": 8.47 * mm, "construction": true});
            skCircle(sketch, "E14.10.5.1", {"center": v(254, 127) * mm, "radius": 2.38 * mm});
            skCircle(sketch, "E14.10.6.0", {"center": v(254, 152.4) * mm, "radius": 8.47 * mm, "construction": true});
            skCircle(sketch, "E14.10.6.1", {"center": v(254, 152.4) * mm, "radius": 2.38 * mm});
            skCircle(sketch, "E14.10.7.0", {"center": v(254, 177.8) * mm, "radius": 8.47 * mm, "construction": true});
            skCircle(sketch, "E14.10.7.1", {"center": v(254, 177.8) * mm, "radius": 2.38 * mm});
            skCircle(sketch, "E14.10.8.0", {"center": v(254, 203.2) * mm, "radius": 8.47 * mm, "construction": true});
            skCircle(sketch, "E14.10.8.1", {"center": v(254, 203.2) * mm, "radius": 2.38 * mm});
            skCircle(sketch, "E14.10.9.0", {"center": v(254, 228.6) * mm, "radius": 8.47 * mm, "construction": true});
            skCircle(sketch, "E14.10.9.1", {"center": v(254, 228.6) * mm, "radius": 2.38 * mm});
            skCircle(sketch, "E14.10.10.0", {"center": v(254, 254) * mm, "radius": 8.47 * mm, "construction": true});
            skCircle(sketch, "E14.10.10.1", {"center": v(254, 254) * mm, "radius": 2.38 * mm});
            skCircle(sketch, "E14.10.11.0", {"center": v(254, 279.4) * mm, "radius": 8.47 * mm, "construction": true});
            skCircle(sketch, "E14.10.11.1", {"center": v(254, 279.4) * mm, "radius": 2.38 * mm});
            skCircle(sketch, "E14.10.12.0", {"center": v(254, 304.8) * mm, "radius": 8.47 * mm, "construction": true});
            skCircle(sketch, "E14.10.12.1", {"center": v(254, 304.8) * mm, "radius": 2.38 * mm});
            skCircle(sketch, "E14.10.13.0", {"center": v(254, 330.2) * mm, "radius": 8.47 * mm, "construction": true});
            skCircle(sketch, "E14.10.13.1", {"center": v(254, 330.2) * mm, "radius": 2.38 * mm});
            skCircle(sketch, "E14.10.14.0", {"center": v(254, 355.6) * mm, "radius": 8.47 * mm, "construction": true});
            skCircle(sketch, "E14.10.14.1", {"center": v(254, 355.6) * mm, "radius": 2.38 * mm});
            skCircle(sketch, "E14.10.15.0", {"center": v(254, 381) * mm, "radius": 8.47 * mm, "construction": true});
            skCircle(sketch, "E14.10.15.1", {"center": v(254, 381) * mm, "radius": 2.38 * mm});
            skCircle(sketch, "E14.11.0.0", {"center": v(279.4, 0) * mm, "radius": 8.47 * mm, "construction": true});
            skCircle(sketch, "E14.11.0.1", {"center": v(279.4, 0) * mm, "radius": 2.38 * mm});
            skCircle(sketch, "E14.11.1.0", {"center": v(279.4, 25.4) * mm, "radius": 8.47 * mm, "construction": true});
            skCircle(sketch, "E14.11.1.1", {"center": v(279.4, 25.4) * mm, "radius": 2.38 * mm});
            skCircle(sketch, "E14.11.2.0", {"center": v(279.4, 50.8) * mm, "radius": 8.47 * mm, "construction": true});
            skCircle(sketch, "E14.11.2.1", {"center": v(279.4, 50.8) * mm, "radius": 2.38 * mm});
            skCircle(sketch, "E14.11.3.0", {"center": v(279.4, 76.2) * mm, "radius": 8.47 * mm, "construction": true});
            skCircle(sketch, "E14.11.3.1", {"center": v(279.4, 76.2) * mm, "radius": 2.38 * mm});
            skCircle(sketch, "E14.11.4.0", {"center": v(279.4, 101.6) * mm, "radius": 8.47 * mm, "construction": true});
            skCircle(sketch, "E14.11.4.1", {"center": v(279.4, 101.6) * mm, "radius": 2.38 * mm});
            skCircle(sketch, "E14.11.5.0", {"center": v(279.4, 127) * mm, "radius": 8.47 * mm, "construction": true});
            skCircle(sketch, "E14.11.5.1", {"center": v(279.4, 127) * mm, "radius": 2.38 * mm});
            skCircle(sketch, "E14.11.6.0", {"center": v(279.4, 152.4) * mm, "radius": 8.47 * mm, "construction": true});
            skCircle(sketch, "E14.11.6.1", {"center": v(279.4, 152.4) * mm, "radius": 2.38 * mm});
            skCircle(sketch, "E14.11.7.0", {"center": v(279.4, 177.8) * mm, "radius": 8.47 * mm, "construction": true});
            skCircle(sketch, "E14.11.7.1", {"center": v(279.4, 177.8) * mm, "radius": 2.38 * mm});
            skCircle(sketch, "E14.11.8.0", {"center": v(279.4, 203.2) * mm, "radius": 8.47 * mm, "construction": true});
            skCircle(sketch, "E14.11.8.1", {"center": v(279.4, 203.2) * mm, "radius": 2.38 * mm});
            skCircle(sketch, "E14.11.9.0", {"center": v(279.4, 228.6) * mm, "radius": 8.47 * mm, "construction": true});
            skCircle(sketch, "E14.11.9.1", {"center": v(279.4, 228.6) * mm, "radius": 2.38 * mm});
            skCircle(sketch, "E14.11.10.0", {"center": v(279.4, 254) * mm, "radius": 8.47 * mm, "construction": true});
            skCircle(sketch, "E14.11.10.1", {"center": v(279.4, 254) * mm, "radius": 2.38 * mm});
            skCircle(sketch, "E14.11.11.0", {"center": v(279.4, 279.4) * mm, "radius": 8.47 * mm, "construction": true});
            skCircle(sketch, "E14.11.11.1", {"center": v(279.4, 279.4) * mm, "radius": 2.38 * mm});
            skCircle(sketch, "E14.11.12.0", {"center": v(279.4, 304.8) * mm, "radius": 8.47 * mm, "construction": true});
            skCircle(sketch, "E14.11.12.1", {"center": v(279.4, 304.8) * mm, "radius": 2.38 * mm});
            skCircle(sketch, "E14.11.13.0", {"center": v(279.4, 330.2) * mm, "radius": 8.47 * mm, "construction": true});
            skCircle(sketch, "E14.11.13.1", {"center": v(279.4, 330.2) * mm, "radius": 2.38 * mm});
            skCircle(sketch, "E14.11.14.0", {"center": v(279.4, 355.6) * mm, "radius": 8.47 * mm, "construction": true});
            skCircle(sketch, "E14.11.14.1", {"center": v(279.4, 355.6) * mm, "radius": 2.38 * mm});
            skCircle(sketch, "E14.11.15.0", {"center": v(279.4, 381) * mm, "radius": 8.47 * mm, "construction": true});
            skCircle(sketch, "E14.11.15.1", {"center": v(279.4, 381) * mm, "radius": 2.38 * mm});
            skCircle(sketch, "E14.12.0.0", {"center": v(304.8, 0) * mm, "radius": 8.47 * mm, "construction": true});
            skCircle(sketch, "E14.12.0.1", {"center": v(304.8, 0) * mm, "radius": 2.38 * mm});
            skCircle(sketch, "E14.12.1.0", {"center": v(304.8, 25.4) * mm, "radius": 8.47 * mm, "construction": true});
            skCircle(sketch, "E14.12.1.1", {"center": v(304.8, 25.4) * mm, "radius": 2.38 * mm});
            skCircle(sketch, "E14.12.2.0", {"center": v(304.8, 50.8) * mm, "radius": 8.47 * mm, "construction": true});
            skCircle(sketch, "E14.12.2.1", {"center": v(304.8, 50.8) * mm, "radius": 2.38 * mm});
            skCircle(sketch, "E14.12.3.0", {"center": v(304.8, 76.2) * mm, "radius": 8.47 * mm, "construction": true});
            skCircle(sketch, "E14.12.3.1", {"center": v(304.8, 76.2) * mm, "radius": 2.38 * mm});
            skCircle(sketch, "E14.12.4.0", {"center": v(304.8, 101.6) * mm, "radius": 8.47 * mm, "construction": true});
            skCircle(sketch, "E14.12.4.1", {"center": v(304.8, 101.6) * mm, "radius": 2.38 * mm});
            skCircle(sketch, "E14.12.5.0", {"center": v(304.8, 127) * mm, "radius": 8.47 * mm, "construction": true});
            skCircle(sketch, "E14.12.5.1", {"center": v(304.8, 127) * mm, "radius": 2.38 * mm});
            skCircle(sketch, "E14.12.6.0", {"center": v(304.8, 152.4) * mm, "radius": 8.47 * mm, "construction": true});
            skCircle(sketch, "E14.12.6.1", {"center": v(304.8, 152.4) * mm, "radius": 2.38 * mm});
            skCircle(sketch, "E14.12.7.0", {"center": v(304.8, 177.8) * mm, "radius": 8.47 * mm, "construction": true});
            skCircle(sketch, "E14.12.7.1", {"center": v(304.8, 177.8) * mm, "radius": 2.38 * mm});
            skCircle(sketch, "E14.12.8.0", {"center": v(304.8, 203.2) * mm, "radius": 8.47 * mm, "construction": true});
            skCircle(sketch, "E14.12.8.1", {"center": v(304.8, 203.2) * mm, "radius": 2.38 * mm});
            skCircle(sketch, "E14.12.9.0", {"center": v(304.8, 228.6) * mm, "radius": 8.47 * mm, "construction": true});
            skCircle(sketch, "E14.12.9.1", {"center": v(304.8, 228.6) * mm, "radius": 2.38 * mm});
            skCircle(sketch, "E14.12.10.0", {"center": v(304.8, 254) * mm, "radius": 8.47 * mm, "construction": true});
            skCircle(sketch, "E14.12.10.1", {"center": v(304.8, 254) * mm, "radius": 2.38 * mm});
            skCircle(sketch, "E14.12.11.0", {"center": v(304.8, 279.4) * mm, "radius": 8.47 * mm, "construction": true});
            skCircle(sketch, "E14.12.11.1", {"center": v(304.8, 279.4) * mm, "radius": 2.38 * mm});
            skCircle(sketch, "E14.12.12.0", {"center": v(304.8, 304.8) * mm, "radius": 8.47 * mm, "construction": true});
            skCircle(sketch, "E14.12.12.1", {"center": v(304.8, 304.8) * mm, "radius": 2.38 * mm});
            skCircle(sketch, "E14.12.13.0", {"center": v(304.8, 330.2) * mm, "radius": 8.47 * mm, "construction": true});
            skCircle(sketch, "E14.12.13.1", {"center": v(304.8, 330.2) * mm, "radius": 2.38 * mm});
            skCircle(sketch, "E14.12.14.0", {"center": v(304.8, 355.6) * mm, "radius": 8.47 * mm, "construction": true});
            skCircle(sketch, "E14.12.14.1", {"center": v(304.8, 355.6) * mm, "radius": 2.38 * mm});
            skCircle(sketch, "E14.12.15.0", {"center": v(304.8, 381) * mm, "radius": 8.47 * mm, "construction": true});
            skCircle(sketch, "E14.12.15.1", {"center": v(304.8, 381) * mm, "radius": 2.38 * mm});
            skCircle(sketch, "E14.13.0.0", {"center": v(330.2, 0) * mm, "radius": 8.47 * mm, "construction": true});
            skCircle(sketch, "E14.13.0.1", {"center": v(330.2, 0) * mm, "radius": 2.38 * mm});
            skCircle(sketch, "E14.13.1.0", {"center": v(330.2, 25.4) * mm, "radius": 8.47 * mm, "construction": true});
            skCircle(sketch, "E14.13.1.1", {"center": v(330.2, 25.4) * mm, "radius": 2.38 * mm});
            skCircle(sketch, "E14.13.2.0", {"center": v(330.2, 50.8) * mm, "radius": 8.47 * mm, "construction": true});
            skCircle(sketch, "E14.13.2.1", {"center": v(330.2, 50.8) * mm, "radius": 2.38 * mm});
            skCircle(sketch, "E14.13.3.0", {"center": v(330.2, 76.2) * mm, "radius": 8.47 * mm, "construction": true});
            skCircle(sketch, "E14.13.3.1", {"center": v(330.2, 76.2) * mm, "radius": 2.38 * mm});
            skCircle(sketch, "E14.13.4.0", {"center": v(330.2, 101.6) * mm, "radius": 8.47 * mm, "construction": true});
            skCircle(sketch, "E14.13.4.1", {"center": v(330.2, 101.6) * mm, "radius": 2.38 * mm});
            skCircle(sketch, "E14.13.5.0", {"center": v(330.2, 127) * mm, "radius": 8.47 * mm, "construction": true});
            skCircle(sketch, "E14.13.5.1", {"center": v(330.2, 127) * mm, "radius": 2.38 * mm});
            skCircle(sketch, "E14.13.6.0", {"center": v(330.2, 152.4) * mm, "radius": 8.47 * mm, "construction": true});
            skCircle(sketch, "E14.13.6.1", {"center": v(330.2, 152.4) * mm, "radius": 2.38 * mm});
            skCircle(sketch, "E14.13.7.0", {"center": v(330.2, 177.8) * mm, "radius": 8.47 * mm, "construction": true});
            skCircle(sketch, "E14.13.7.1", {"center": v(330.2, 177.8) * mm, "radius": 2.38 * mm});
            skCircle(sketch, "E14.13.8.0", {"center": v(330.2, 203.2) * mm, "radius": 8.47 * mm, "construction": true});
            skCircle(sketch, "E14.13.8.1", {"center": v(330.2, 203.2) * mm, "radius": 2.38 * mm});
            skCircle(sketch, "E14.13.9.0", {"center": v(330.2, 228.6) * mm, "radius": 8.47 * mm, "construction": true});
            skCircle(sketch, "E14.13.9.1", {"center": v(330.2, 228.6) * mm, "radius": 2.38 * mm});
            skCircle(sketch, "E14.13.10.0", {"center": v(330.2, 254) * mm, "radius": 8.47 * mm, "construction": true});
            skCircle(sketch, "E14.13.10.1", {"center": v(330.2, 254) * mm, "radius": 2.38 * mm});
            skCircle(sketch, "E14.13.11.0", {"center": v(330.2, 279.4) * mm, "radius": 8.47 * mm, "construction": true});
            skCircle(sketch, "E14.13.11.1", {"center": v(330.2, 279.4) * mm, "radius": 2.38 * mm});
            skCircle(sketch, "E14.13.12.0", {"center": v(330.2, 304.8) * mm, "radius": 8.47 * mm, "construction": true});
            skCircle(sketch, "E14.13.12.1", {"center": v(330.2, 304.8) * mm, "radius": 2.38 * mm});
            skCircle(sketch, "E14.13.13.0", {"center": v(330.2, 330.2) * mm, "radius": 8.47 * mm, "construction": true});
            skCircle(sketch, "E14.13.13.1", {"center": v(330.2, 330.2) * mm, "radius": 2.38 * mm});
            skCircle(sketch, "E14.13.14.0", {"center": v(330.2, 355.6) * mm, "radius": 8.47 * mm, "construction": true});
            skCircle(sketch, "E14.13.14.1", {"center": v(330.2, 355.6) * mm, "radius": 2.38 * mm});
            skCircle(sketch, "E14.13.15.0", {"center": v(330.2, 381) * mm, "radius": 8.47 * mm, "construction": true});
            skCircle(sketch, "E14.13.15.1", {"center": v(330.2, 381) * mm, "radius": 2.38 * mm});
            skCircle(sketch, "E14.14.0.0", {"center": v(355.6, 0) * mm, "radius": 8.47 * mm, "construction": true});
            skCircle(sketch, "E14.14.0.1", {"center": v(355.6, 0) * mm, "radius": 2.38 * mm});
            skCircle(sketch, "E14.14.1.0", {"center": v(355.6, 25.4) * mm, "radius": 8.47 * mm, "construction": true});
            skCircle(sketch, "E14.14.1.1", {"center": v(355.6, 25.4) * mm, "radius": 2.38 * mm});
            skCircle(sketch, "E14.14.2.0", {"center": v(355.6, 50.8) * mm, "radius": 8.47 * mm, "construction": true});
            skCircle(sketch, "E14.14.2.1", {"center": v(355.6, 50.8) * mm, "radius": 2.38 * mm});
            skCircle(sketch, "E14.14.3.0", {"center": v(355.6, 76.2) * mm, "radius": 8.47 * mm, "construction": true});
            skCircle(sketch, "E14.14.3.1", {"center": v(355.6, 76.2) * mm, "radius": 2.38 * mm});
            skCircle(sketch, "E14.14.4.0", {"center": v(355.6, 101.6) * mm, "radius": 8.47 * mm, "construction": true});
            skCircle(sketch, "E14.14.4.1", {"center": v(355.6, 101.6) * mm, "radius": 2.38 * mm});
            skCircle(sketch, "E14.14.5.0", {"center": v(355.6, 127) * mm, "radius": 8.47 * mm, "construction": true});
            skCircle(sketch, "E14.14.5.1", {"center": v(355.6, 127) * mm, "radius": 2.38 * mm});
            skCircle(sketch, "E14.14.6.0", {"center": v(355.6, 152.4) * mm, "radius": 8.47 * mm, "construction": true});
            skCircle(sketch, "E14.14.6.1", {"center": v(355.6, 152.4) * mm, "radius": 2.38 * mm});
            skCircle(sketch, "E14.14.7.0", {"center": v(355.6, 177.8) * mm, "radius": 8.47 * mm, "construction": true});
            skCircle(sketch, "E14.14.7.1", {"center": v(355.6, 177.8) * mm, "radius": 2.38 * mm});
            skCircle(sketch, "E14.14.8.0", {"center": v(355.6, 203.2) * mm, "radius": 8.47 * mm, "construction": true});
            skCircle(sketch, "E14.14.8.1", {"center": v(355.6, 203.2) * mm, "radius": 2.38 * mm});
            skCircle(sketch, "E14.14.9.0", {"center": v(355.6, 228.6) * mm, "radius": 8.47 * mm, "construction": true});
            skCircle(sketch, "E14.14.9.1", {"center": v(355.6, 228.6) * mm, "radius": 2.38 * mm});
            skCircle(sketch, "E14.14.10.0", {"center": v(355.6, 254) * mm, "radius": 8.47 * mm, "construction": true});
            skCircle(sketch, "E14.14.10.1", {"center": v(355.6, 254) * mm, "radius": 2.38 * mm});
            skCircle(sketch, "E14.14.11.0", {"center": v(355.6, 279.4) * mm, "radius": 8.47 * mm, "construction": true});
            skCircle(sketch, "E14.14.11.1", {"center": v(355.6, 279.4) * mm, "radius": 2.38 * mm});
            skCircle(sketch, "E14.14.12.0", {"center": v(355.6, 304.8) * mm, "radius": 8.47 * mm, "construction": true});
            skCircle(sketch, "E14.14.12.1", {"center": v(355.6, 304.8) * mm, "radius": 2.38 * mm});
            skCircle(sketch, "E14.14.13.0", {"center": v(355.6, 330.2) * mm, "radius": 8.47 * mm, "construction": true});
            skCircle(sketch, "E14.14.13.1", {"center": v(355.6, 330.2) * mm, "radius": 2.38 * mm});
            skCircle(sketch, "E14.14.14.0", {"center": v(355.6, 355.6) * mm, "radius": 8.47 * mm, "construction": true});
            skCircle(sketch, "E14.14.14.1", {"center": v(355.6, 355.6) * mm, "radius": 2.38 * mm});
            skCircle(sketch, "E14.14.15.0", {"center": v(355.6, 381) * mm, "radius": 8.47 * mm, "construction": true});
            skCircle(sketch, "E14.14.15.1", {"center": v(355.6, 381) * mm, "radius": 2.38 * mm});
            skCircle(sketch, "E14.15.0.0", {"center": v(381, 0) * mm, "radius": 8.47 * mm, "construction": true});
            skCircle(sketch, "E14.15.0.1", {"center": v(381, 0) * mm, "radius": 2.38 * mm});
            skCircle(sketch, "E14.15.1.0", {"center": v(381, 25.4) * mm, "radius": 8.47 * mm, "construction": true});
            skCircle(sketch, "E14.15.1.1", {"center": v(381, 25.4) * mm, "radius": 2.38 * mm});
            skCircle(sketch, "E14.15.2.0", {"center": v(381, 50.8) * mm, "radius": 8.47 * mm, "construction": true});
            skCircle(sketch, "E14.15.2.1", {"center": v(381, 50.8) * mm, "radius": 2.38 * mm});
            skCircle(sketch, "E14.15.3.0", {"center": v(381, 76.2) * mm, "radius": 8.47 * mm, "construction": true});
            skCircle(sketch, "E14.15.3.1", {"center": v(381, 76.2) * mm, "radius": 2.38 * mm});
            skCircle(sketch, "E14.15.4.0", {"center": v(381, 101.6) * mm, "radius": 8.47 * mm, "construction": true});
            skCircle(sketch, "E14.15.4.1", {"center": v(381, 101.6) * mm, "radius": 2.38 * mm});
            skCircle(sketch, "E14.15.5.0", {"center": v(381, 127) * mm, "radius": 8.47 * mm, "construction": true});
            skCircle(sketch, "E14.15.5.1", {"center": v(381, 127) * mm, "radius": 2.38 * mm});
            skCircle(sketch, "E14.15.6.0", {"center": v(381, 152.4) * mm, "radius": 8.47 * mm, "construction": true});
            skCircle(sketch, "E14.15.6.1", {"center": v(381, 152.4) * mm, "radius": 2.38 * mm});
            skCircle(sketch, "E14.15.7.0", {"center": v(381, 177.8) * mm, "radius": 8.47 * mm, "construction": true});
            skCircle(sketch, "E14.15.7.1", {"center": v(381, 177.8) * mm, "radius": 2.38 * mm});
            skCircle(sketch, "E14.15.8.0", {"center": v(381, 203.2) * mm, "radius": 8.47 * mm, "construction": true});
            skCircle(sketch, "E14.15.8.1", {"center": v(381, 203.2) * mm, "radius": 2.38 * mm});
            skCircle(sketch, "E14.15.9.0", {"center": v(381, 228.6) * mm, "radius": 8.47 * mm, "construction": true});
            skCircle(sketch, "E14.15.9.1", {"center": v(381, 228.6) * mm, "radius": 2.38 * mm});
            skCircle(sketch, "E14.15.10.0", {"center": v(381, 254) * mm, "radius": 8.47 * mm, "construction": true});
            skCircle(sketch, "E14.15.10.1", {"center": v(381, 254) * mm, "radius": 2.38 * mm});
            skCircle(sketch, "E14.15.11.0", {"center": v(381, 279.4) * mm, "radius": 8.47 * mm, "construction": true});
            skCircle(sketch, "E14.15.11.1", {"center": v(381, 279.4) * mm, "radius": 2.38 * mm});
            skCircle(sketch, "E14.15.12.0", {"center": v(381, 304.8) * mm, "radius": 8.47 * mm, "construction": true});
            skCircle(sketch, "E14.15.12.1", {"center": v(381, 304.8) * mm, "radius": 2.38 * mm});
            skCircle(sketch, "E14.15.13.0", {"center": v(381, 330.2) * mm, "radius": 8.47 * mm, "construction": true});
            skCircle(sketch, "E14.15.13.1", {"center": v(381, 330.2) * mm, "radius": 2.38 * mm});
            skCircle(sketch, "E14.15.14.0", {"center": v(381, 355.6) * mm, "radius": 8.47 * mm, "construction": true});
            skCircle(sketch, "E14.15.14.1", {"center": v(381, 355.6) * mm, "radius": 2.38 * mm});
            skCircle(sketch, "E14.15.15.0", {"center": v(381, 381) * mm, "radius": 8.47 * mm, "construction": true});
            skCircle(sketch, "E14.15.15.1", {"center": v(381, 381) * mm, "radius": 2.38 * mm});
            skCircle(sketch, "E14.16.0.0", {"center": v(406.4, 0) * mm, "radius": 8.47 * mm, "construction": true});
            skCircle(sketch, "E14.16.0.1", {"center": v(406.4, 0) * mm, "radius": 2.38 * mm});
            skCircle(sketch, "E14.16.1.0", {"center": v(406.4, 25.4) * mm, "radius": 8.47 * mm, "construction": true});
            skCircle(sketch, "E14.16.1.1", {"center": v(406.4, 25.4) * mm, "radius": 2.38 * mm});
            skCircle(sketch, "E14.16.2.0", {"center": v(406.4, 50.8) * mm, "radius": 8.47 * mm, "construction": true});
            skCircle(sketch, "E14.16.2.1", {"center": v(406.4, 50.8) * mm, "radius": 2.38 * mm});
            skCircle(sketch, "E14.16.3.0", {"center": v(406.4, 76.2) * mm, "radius": 8.47 * mm, "construction": true});
            skCircle(sketch, "E14.16.3.1", {"center": v(406.4, 76.2) * mm, "radius": 2.38 * mm});
            skCircle(sketch, "E14.16.4.0", {"center": v(406.4, 101.6) * mm, "radius": 8.47 * mm, "construction": true});
            skCircle(sketch, "E14.16.4.1", {"center": v(406.4, 101.6) * mm, "radius": 2.38 * mm});
            skCircle(sketch, "E14.16.5.0", {"center": v(406.4, 127) * mm, "radius": 8.47 * mm, "construction": true});
            skCircle(sketch, "E14.16.5.1", {"center": v(406.4, 127) * mm, "radius": 2.38 * mm});
            skCircle(sketch, "E14.16.6.0", {"center": v(406.4, 152.4) * mm, "radius": 8.47 * mm, "construction": true});
            skCircle(sketch, "E14.16.6.1", {"center": v(406.4, 152.4) * mm, "radius": 2.38 * mm});
            skCircle(sketch, "E14.16.7.0", {"center": v(406.4, 177.8) * mm, "radius": 8.47 * mm, "construction": true});
            skCircle(sketch, "E14.16.7.1", {"center": v(406.4, 177.8) * mm, "radius": 2.38 * mm});
            skCircle(sketch, "E14.16.8.0", {"center": v(406.4, 203.2) * mm, "radius": 8.47 * mm, "construction": true});
            skCircle(sketch, "E14.16.8.1", {"center": v(406.4, 203.2) * mm, "radius": 2.38 * mm});
            skCircle(sketch, "E14.16.9.0", {"center": v(406.4, 228.6) * mm, "radius": 8.47 * mm, "construction": true});
            skCircle(sketch, "E14.16.9.1", {"center": v(406.4, 228.6) * mm, "radius": 2.38 * mm});
            skCircle(sketch, "E14.16.10.0", {"center": v(406.4, 254) * mm, "radius": 8.47 * mm, "construction": true});
            skCircle(sketch, "E14.16.10.1", {"center": v(406.4, 254) * mm, "radius": 2.38 * mm});
            skCircle(sketch, "E14.16.11.0", {"center": v(406.4, 279.4) * mm, "radius": 8.47 * mm, "construction": true});
            skCircle(sketch, "E14.16.11.1", {"center": v(406.4, 279.4) * mm, "radius": 2.38 * mm});
            skCircle(sketch, "E14.16.12.0", {"center": v(406.4, 304.8) * mm, "radius": 8.47 * mm, "construction": true});
            skCircle(sketch, "E14.16.12.1", {"center": v(406.4, 304.8) * mm, "radius": 2.38 * mm});
            skCircle(sketch, "E14.16.13.0", {"center": v(406.4, 330.2) * mm, "radius": 8.47 * mm, "construction": true});
            skCircle(sketch, "E14.16.13.1", {"center": v(406.4, 330.2) * mm, "radius": 2.38 * mm});
            skCircle(sketch, "E14.16.14.0", {"center": v(406.4, 355.6) * mm, "radius": 8.47 * mm, "construction": true});
            skCircle(sketch, "E14.16.14.1", {"center": v(406.4, 355.6) * mm, "radius": 2.38 * mm});
            skCircle(sketch, "E14.16.15.0", {"center": v(406.4, 381) * mm, "radius": 8.47 * mm, "construction": true});
            skCircle(sketch, "E14.16.15.1", {"center": v(406.4, 381) * mm, "radius": 2.38 * mm});
            skCircle(sketch, "E14.17.0.0", {"center": v(431.8, 0) * mm, "radius": 8.47 * mm, "construction": true});
            skCircle(sketch, "E14.17.0.1", {"center": v(431.8, 0) * mm, "radius": 2.38 * mm});
            skCircle(sketch, "E14.17.1.0", {"center": v(431.8, 25.4) * mm, "radius": 8.47 * mm, "construction": true});
            skCircle(sketch, "E14.17.1.1", {"center": v(431.8, 25.4) * mm, "radius": 2.38 * mm});
            skCircle(sketch, "E14.17.2.0", {"center": v(431.8, 50.8) * mm, "radius": 8.47 * mm, "construction": true});
            skCircle(sketch, "E14.17.2.1", {"center": v(431.8, 50.8) * mm, "radius": 2.38 * mm});
            skCircle(sketch, "E14.17.3.0", {"center": v(431.8, 76.2) * mm, "radius": 8.47 * mm, "construction": true});
            skCircle(sketch, "E14.17.3.1", {"center": v(431.8, 76.2) * mm, "radius": 2.38 * mm});
            skCircle(sketch, "E14.17.4.0", {"center": v(431.8, 101.6) * mm, "radius": 8.47 * mm, "construction": true});
            skCircle(sketch, "E14.17.4.1", {"center": v(431.8, 101.6) * mm, "radius": 2.38 * mm});
            skCircle(sketch, "E14.17.5.0", {"center": v(431.8, 127) * mm, "radius": 8.47 * mm, "construction": true});
            skCircle(sketch, "E14.17.5.1", {"center": v(431.8, 127) * mm, "radius": 2.38 * mm});
            skCircle(sketch, "E14.17.6.0", {"center": v(431.8, 152.4) * mm, "radius": 8.47 * mm, "construction": true});
            skCircle(sketch, "E14.17.6.1", {"center": v(431.8, 152.4) * mm, "radius": 2.38 * mm});
            skCircle(sketch, "E14.17.7.0", {"center": v(431.8, 177.8) * mm, "radius": 8.47 * mm, "construction": true});
            skCircle(sketch, "E14.17.7.1", {"center": v(431.8, 177.8) * mm, "radius": 2.38 * mm});
            skCircle(sketch, "E14.17.8.0", {"center": v(431.8, 203.2) * mm, "radius": 8.47 * mm, "construction": true});
            skCircle(sketch, "E14.17.8.1", {"center": v(431.8, 203.2) * mm, "radius": 2.38 * mm});
            skCircle(sketch, "E14.17.9.0", {"center": v(431.8, 228.6) * mm, "radius": 8.47 * mm, "construction": true});
            skCircle(sketch, "E14.17.9.1", {"center": v(431.8, 228.6) * mm, "radius": 2.38 * mm});
            skCircle(sketch, "E14.17.10.0", {"center": v(431.8, 254) * mm, "radius": 8.47 * mm, "construction": true});
            skCircle(sketch, "E14.17.10.1", {"center": v(431.8, 254) * mm, "radius": 2.38 * mm});
            skCircle(sketch, "E14.17.11.0", {"center": v(431.8, 279.4) * mm, "radius": 8.47 * mm, "construction": true});
            skCircle(sketch, "E14.17.11.1", {"center": v(431.8, 279.4) * mm, "radius": 2.38 * mm});
            skCircle(sketch, "E14.17.12.0", {"center": v(431.8, 304.8) * mm, "radius": 8.47 * mm, "construction": true});
            skCircle(sketch, "E14.17.12.1", {"center": v(431.8, 304.8) * mm, "radius": 2.38 * mm});
            skCircle(sketch, "E14.17.13.0", {"center": v(431.8, 330.2) * mm, "radius": 8.47 * mm, "construction": true});
            skCircle(sketch, "E14.17.13.1", {"center": v(431.8, 330.2) * mm, "radius": 2.38 * mm});
            skCircle(sketch, "E14.17.14.0", {"center": v(431.8, 355.6) * mm, "radius": 8.47 * mm, "construction": true});
            skCircle(sketch, "E14.17.14.1", {"center": v(431.8, 355.6) * mm, "radius": 2.38 * mm});
            skCircle(sketch, "E14.17.15.0", {"center": v(431.8, 381) * mm, "radius": 8.47 * mm, "construction": true});
            skCircle(sketch, "E14.17.15.1", {"center": v(431.8, 381) * mm, "radius": 2.38 * mm});
            skCircle(sketch, "E14.18.0.0", {"center": v(457.2, 0) * mm, "radius": 8.47 * mm, "construction": true});
            skCircle(sketch, "E14.18.0.1", {"center": v(457.2, 0) * mm, "radius": 2.38 * mm});
            skCircle(sketch, "E14.18.1.0", {"center": v(457.2, 25.4) * mm, "radius": 8.47 * mm, "construction": true});
            skCircle(sketch, "E14.18.1.1", {"center": v(457.2, 25.4) * mm, "radius": 2.38 * mm});
            skCircle(sketch, "E14.18.2.0", {"center": v(457.2, 50.8) * mm, "radius": 8.47 * mm, "construction": true});
            skCircle(sketch, "E14.18.2.1", {"center": v(457.2, 50.8) * mm, "radius": 2.38 * mm});
            skCircle(sketch, "E14.18.3.0", {"center": v(457.2, 76.2) * mm, "radius": 8.47 * mm, "construction": true});
            skCircle(sketch, "E14.18.3.1", {"center": v(457.2, 76.2) * mm, "radius": 2.38 * mm});
            skCircle(sketch, "E14.18.4.0", {"center": v(457.2, 101.6) * mm, "radius": 8.47 * mm, "construction": true});
            skCircle(sketch, "E14.18.4.1", {"center": v(457.2, 101.6) * mm, "radius": 2.38 * mm});
            skCircle(sketch, "E14.18.5.0", {"center": v(457.2, 127) * mm, "radius": 8.47 * mm, "construction": true});
            skCircle(sketch, "E14.18.5.1", {"center": v(457.2, 127) * mm, "radius": 2.38 * mm});
            skCircle(sketch, "E14.18.6.0", {"center": v(457.2, 152.4) * mm, "radius": 8.47 * mm, "construction": true});
            skCircle(sketch, "E14.18.6.1", {"center": v(457.2, 152.4) * mm, "radius": 2.38 * mm});
            skCircle(sketch, "E14.18.7.0", {"center": v(457.2, 177.8) * mm, "radius": 8.47 * mm, "construction": true});
            skCircle(sketch, "E14.18.7.1", {"center": v(457.2, 177.8) * mm, "radius": 2.38 * mm});
            skCircle(sketch, "E14.18.8.0", {"center": v(457.2, 203.2) * mm, "radius": 8.47 * mm, "construction": true});
            skCircle(sketch, "E14.18.8.1", {"center": v(457.2, 203.2) * mm, "radius": 2.38 * mm});
            skCircle(sketch, "E14.18.9.0", {"center": v(457.2, 228.6) * mm, "radius": 8.47 * mm, "construction": true});
            skCircle(sketch, "E14.18.9.1", {"center": v(457.2, 228.6) * mm, "radius": 2.38 * mm});
            skCircle(sketch, "E14.18.10.0", {"center": v(457.2, 254) * mm, "radius": 8.47 * mm, "construction": true});
            skCircle(sketch, "E14.18.10.1", {"center": v(457.2, 254) * mm, "radius": 2.38 * mm});
            skCircle(sketch, "E14.18.11.0", {"center": v(457.2, 279.4) * mm, "radius": 8.47 * mm, "construction": true});
            skCircle(sketch, "E14.18.11.1", {"center": v(457.2, 279.4) * mm, "radius": 2.38 * mm});
            skCircle(sketch, "E14.18.12.0", {"center": v(457.2, 304.8) * mm, "radius": 8.47 * mm, "construction": true});
            skCircle(sketch, "E14.18.12.1", {"center": v(457.2, 304.8) * mm, "radius": 2.38 * mm});
            skCircle(sketch, "E14.18.13.0", {"center": v(457.2, 330.2) * mm, "radius": 8.47 * mm, "construction": true});
            skCircle(sketch, "E14.18.13.1", {"center": v(457.2, 330.2) * mm, "radius": 2.38 * mm});
            skCircle(sketch, "E14.18.14.0", {"center": v(457.2, 355.6) * mm, "radius": 8.47 * mm, "construction": true});
            skCircle(sketch, "E14.18.14.1", {"center": v(457.2, 355.6) * mm, "radius": 2.38 * mm});
            skCircle(sketch, "E14.18.15.0", {"center": v(457.2, 381) * mm, "radius": 8.47 * mm, "construction": true});
            skCircle(sketch, "E14.18.15.1", {"center": v(457.2, 381) * mm, "radius": 2.38 * mm});
            skCircle(sketch, "E14.19.0.0", {"center": v(482.6, 0) * mm, "radius": 8.47 * mm, "construction": true});
            skCircle(sketch, "E14.19.0.1", {"center": v(482.6, 0) * mm, "radius": 2.38 * mm});
            skCircle(sketch, "E14.19.1.0", {"center": v(482.6, 25.4) * mm, "radius": 8.47 * mm, "construction": true});
            skCircle(sketch, "E14.19.1.1", {"center": v(482.6, 25.4) * mm, "radius": 2.38 * mm});
            skCircle(sketch, "E14.19.2.0", {"center": v(482.6, 50.8) * mm, "radius": 8.47 * mm, "construction": true});
            skCircle(sketch, "E14.19.2.1", {"center": v(482.6, 50.8) * mm, "radius": 2.38 * mm});
            skCircle(sketch, "E14.19.3.0", {"center": v(482.6, 76.2) * mm, "radius": 8.47 * mm, "construction": true});
            skCircle(sketch, "E14.19.3.1", {"center": v(482.6, 76.2) * mm, "radius": 2.38 * mm});
            skCircle(sketch, "E14.19.4.0", {"center": v(482.6, 101.6) * mm, "radius": 8.47 * mm, "construction": true});
            skCircle(sketch, "E14.19.4.1", {"center": v(482.6, 101.6) * mm, "radius": 2.38 * mm});
            skCircle(sketch, "E14.19.5.0", {"center": v(482.6, 127) * mm, "radius": 8.47 * mm, "construction": true});
            skCircle(sketch, "E14.19.5.1", {"center": v(482.6, 127) * mm, "radius": 2.38 * mm});
            skCircle(sketch, "E14.19.6.0", {"center": v(482.6, 152.4) * mm, "radius": 8.47 * mm, "construction": true});
            skCircle(sketch, "E14.19.6.1", {"center": v(482.6, 152.4) * mm, "radius": 2.38 * mm});
            skCircle(sketch, "E14.19.7.0", {"center": v(482.6, 177.8) * mm, "radius": 8.47 * mm, "construction": true});
            skCircle(sketch, "E14.19.7.1", {"center": v(482.6, 177.8) * mm, "radius": 2.38 * mm});
            skCircle(sketch, "E14.19.8.0", {"center": v(482.6, 203.2) * mm, "radius": 8.47 * mm, "construction": true});
            skCircle(sketch, "E14.19.8.1", {"center": v(482.6, 203.2) * mm, "radius": 2.38 * mm});
            skCircle(sketch, "E14.19.9.0", {"center": v(482.6, 228.6) * mm, "radius": 8.47 * mm, "construction": true});
            skCircle(sketch, "E14.19.9.1", {"center": v(482.6, 228.6) * mm, "radius": 2.38 * mm});
            skCircle(sketch, "E14.19.10.0", {"center": v(482.6, 254) * mm, "radius": 8.47 * mm, "construction": true});
            skCircle(sketch, "E14.19.10.1", {"center": v(482.6, 254) * mm, "radius": 2.38 * mm});
            skCircle(sketch, "E14.19.11.0", {"center": v(482.6, 279.4) * mm, "radius": 8.47 * mm, "construction": true});
            skCircle(sketch, "E14.19.11.1", {"center": v(482.6, 279.4) * mm, "radius": 2.38 * mm});
            skCircle(sketch, "E14.19.12.0", {"center": v(482.6, 304.8) * mm, "radius": 8.47 * mm, "construction": true});
            skCircle(sketch, "E14.19.12.1", {"center": v(482.6, 304.8) * mm, "radius": 2.38 * mm});
            skCircle(sketch, "E14.19.13.0", {"center": v(482.6, 330.2) * mm, "radius": 8.47 * mm, "construction": true});
            skCircle(sketch, "E14.19.13.1", {"center": v(482.6, 330.2) * mm, "radius": 2.38 * mm});
            skCircle(sketch, "E14.19.14.0", {"center": v(482.6, 355.6) * mm, "radius": 8.47 * mm, "construction": true});
            skCircle(sketch, "E14.19.14.1", {"center": v(482.6, 355.6) * mm, "radius": 2.38 * mm});
            skCircle(sketch, "E14.19.15.0", {"center": v(482.6, 381) * mm, "radius": 8.47 * mm, "construction": true});
            skCircle(sketch, "E14.19.15.1", {"center": v(482.6, 381) * mm, "radius": 2.38 * mm});
            skCircle(sketch, "E14.20.0.0", {"center": v(508, 0) * mm, "radius": 8.47 * mm, "construction": true});
            skCircle(sketch, "E14.20.0.1", {"center": v(508, 0) * mm, "radius": 2.38 * mm});
            skCircle(sketch, "E14.20.1.0", {"center": v(508, 25.4) * mm, "radius": 8.47 * mm, "construction": true});
            skCircle(sketch, "E14.20.1.1", {"center": v(508, 25.4) * mm, "radius": 2.38 * mm});
            skCircle(sketch, "E14.20.2.0", {"center": v(508, 50.8) * mm, "radius": 8.47 * mm, "construction": true});
            skCircle(sketch, "E14.20.2.1", {"center": v(508, 50.8) * mm, "radius": 2.38 * mm});
            skCircle(sketch, "E14.20.3.0", {"center": v(508, 76.2) * mm, "radius": 8.47 * mm, "construction": true});
            skCircle(sketch, "E14.20.3.1", {"center": v(508, 76.2) * mm, "radius": 2.38 * mm});
            skCircle(sketch, "E14.20.4.0", {"center": v(508, 101.6) * mm, "radius": 8.47 * mm, "construction": true});
            skCircle(sketch, "E14.20.4.1", {"center": v(508, 101.6) * mm, "radius": 2.38 * mm});
            skCircle(sketch, "E14.20.5.0", {"center": v(508, 127) * mm, "radius": 8.47 * mm, "construction": true});
            skCircle(sketch, "E14.20.5.1", {"center": v(508, 127) * mm, "radius": 2.38 * mm});
            skCircle(sketch, "E14.20.6.0", {"center": v(508, 152.4) * mm, "radius": 8.47 * mm, "construction": true});
            skCircle(sketch, "E14.20.6.1", {"center": v(508, 152.4) * mm, "radius": 2.38 * mm});
            skCircle(sketch, "E14.20.7.0", {"center": v(508, 177.8) * mm, "radius": 8.47 * mm, "construction": true});
            skCircle(sketch, "E14.20.7.1", {"center": v(508, 177.8) * mm, "radius": 2.38 * mm});
            skCircle(sketch, "E14.20.8.0", {"center": v(508, 203.2) * mm, "radius": 8.47 * mm, "construction": true});
            skCircle(sketch, "E14.20.8.1", {"center": v(508, 203.2) * mm, "radius": 2.38 * mm});
            skCircle(sketch, "E14.20.9.0", {"center": v(508, 228.6) * mm, "radius": 8.47 * mm, "construction": true});
            skCircle(sketch, "E14.20.9.1", {"center": v(508, 228.6) * mm, "radius": 2.38 * mm});
            skCircle(sketch, "E14.20.10.0", {"center": v(508, 254) * mm, "radius": 8.47 * mm, "construction": true});
            skCircle(sketch, "E14.20.10.1", {"center": v(508, 254) * mm, "radius": 2.38 * mm});
            skCircle(sketch, "E14.20.11.0", {"center": v(508, 279.4) * mm, "radius": 8.47 * mm, "construction": true});
            skCircle(sketch, "E14.20.11.1", {"center": v(508, 279.4) * mm, "radius": 2.38 * mm});
            skCircle(sketch, "E14.20.12.0", {"center": v(508, 304.8) * mm, "radius": 8.47 * mm, "construction": true});
            skCircle(sketch, "E14.20.12.1", {"center": v(508, 304.8) * mm, "radius": 2.38 * mm});
            skCircle(sketch, "E14.20.13.0", {"center": v(508, 330.2) * mm, "radius": 8.47 * mm, "construction": true});
            skCircle(sketch, "E14.20.13.1", {"center": v(508, 330.2) * mm, "radius": 2.38 * mm});
            skCircle(sketch, "E14.20.14.0", {"center": v(508, 355.6) * mm, "radius": 8.47 * mm, "construction": true});
            skCircle(sketch, "E14.20.14.1", {"center": v(508, 355.6) * mm, "radius": 2.38 * mm});
            skCircle(sketch, "E14.20.15.0", {"center": v(508, 381) * mm, "radius": 8.47 * mm, "construction": true});
            skCircle(sketch, "E14.20.15.1", {"center": v(508, 381) * mm, "radius": 2.38 * mm});
            skCircle(sketch, "E14.21.0.0", {"center": v(533.4, 0) * mm, "radius": 8.47 * mm, "construction": true});
            skCircle(sketch, "E14.21.0.1", {"center": v(533.4, 0) * mm, "radius": 2.38 * mm});
            skCircle(sketch, "E14.21.1.0", {"center": v(533.4, 25.4) * mm, "radius": 8.47 * mm, "construction": true});
            skCircle(sketch, "E14.21.1.1", {"center": v(533.4, 25.4) * mm, "radius": 2.38 * mm});
            skCircle(sketch, "E14.21.2.0", {"center": v(533.4, 50.8) * mm, "radius": 8.47 * mm, "construction": true});
            skCircle(sketch, "E14.21.2.1", {"center": v(533.4, 50.8) * mm, "radius": 2.38 * mm});
            skCircle(sketch, "E14.21.3.0", {"center": v(533.4, 76.2) * mm, "radius": 8.47 * mm, "construction": true});
            skCircle(sketch, "E14.21.3.1", {"center": v(533.4, 76.2) * mm, "radius": 2.38 * mm});
            skCircle(sketch, "E14.21.4.0", {"center": v(533.4, 101.6) * mm, "radius": 8.47 * mm, "construction": true});
            skCircle(sketch, "E14.21.4.1", {"center": v(533.4, 101.6) * mm, "radius": 2.38 * mm});
            skCircle(sketch, "E14.21.5.0", {"center": v(533.4, 127) * mm, "radius": 8.47 * mm, "construction": true});
            skCircle(sketch, "E14.21.5.1", {"center": v(533.4, 127) * mm, "radius": 2.38 * mm});
            skCircle(sketch, "E14.21.6.0", {"center": v(533.4, 152.4) * mm, "radius": 8.47 * mm, "construction": true});
            skCircle(sketch, "E14.21.6.1", {"center": v(533.4, 152.4) * mm, "radius": 2.38 * mm});
            skCircle(sketch, "E14.21.7.0", {"center": v(533.4, 177.8) * mm, "radius": 8.47 * mm, "construction": true});
            skCircle(sketch, "E14.21.7.1", {"center": v(533.4, 177.8) * mm, "radius": 2.38 * mm});
            skCircle(sketch, "E14.21.8.0", {"center": v(533.4, 203.2) * mm, "radius": 8.47 * mm, "construction": true});
            skCircle(sketch, "E14.21.8.1", {"center": v(533.4, 203.2) * mm, "radius": 2.38 * mm});
            skCircle(sketch, "E14.21.9.0", {"center": v(533.4, 228.6) * mm, "radius": 8.47 * mm, "construction": true});
            skCircle(sketch, "E14.21.9.1", {"center": v(533.4, 228.6) * mm, "radius": 2.38 * mm});
            skCircle(sketch, "E14.21.10.0", {"center": v(533.4, 254) * mm, "radius": 8.47 * mm, "construction": true});
            skCircle(sketch, "E14.21.10.1", {"center": v(533.4, 254) * mm, "radius": 2.38 * mm});
            skCircle(sketch, "E14.21.11.0", {"center": v(533.4, 279.4) * mm, "radius": 8.47 * mm, "construction": true});
            skCircle(sketch, "E14.21.11.1", {"center": v(533.4, 279.4) * mm, "radius": 2.38 * mm});
            skCircle(sketch, "E14.21.12.0", {"center": v(533.4, 304.8) * mm, "radius": 8.47 * mm, "construction": true});
            skCircle(sketch, "E14.21.12.1", {"center": v(533.4, 304.8) * mm, "radius": 2.38 * mm});
            skCircle(sketch, "E14.21.13.0", {"center": v(533.4, 330.2) * mm, "radius": 8.47 * mm, "construction": true});
            skCircle(sketch, "E14.21.13.1", {"center": v(533.4, 330.2) * mm, "radius": 2.38 * mm});
            skCircle(sketch, "E14.21.14.0", {"center": v(533.4, 355.6) * mm, "radius": 8.47 * mm, "construction": true});
            skCircle(sketch, "E14.21.14.1", {"center": v(533.4, 355.6) * mm, "radius": 2.38 * mm});
            skCircle(sketch, "E14.21.15.0", {"center": v(533.4, 381) * mm, "radius": 8.47 * mm, "construction": true});
            skCircle(sketch, "E14.21.15.1", {"center": v(533.4, 381) * mm, "radius": 2.38 * mm});
            skCircle(sketch, "E14.22.0.0", {"center": v(558.8, 0) * mm, "radius": 8.47 * mm, "construction": true});
            skCircle(sketch, "E14.22.0.1", {"center": v(558.8, 0) * mm, "radius": 2.38 * mm});
            skCircle(sketch, "E14.22.1.0", {"center": v(558.8, 25.4) * mm, "radius": 8.47 * mm, "construction": true});
            skCircle(sketch, "E14.22.1.1", {"center": v(558.8, 25.4) * mm, "radius": 2.38 * mm});
            skCircle(sketch, "E14.22.2.0", {"center": v(558.8, 50.8) * mm, "radius": 8.47 * mm, "construction": true});
            skCircle(sketch, "E14.22.2.1", {"center": v(558.8, 50.8) * mm, "radius": 2.38 * mm});
            skCircle(sketch, "E14.22.3.0", {"center": v(558.8, 76.2) * mm, "radius": 8.47 * mm, "construction": true});
            skCircle(sketch, "E14.22.3.1", {"center": v(558.8, 76.2) * mm, "radius": 2.38 * mm});
            skCircle(sketch, "E14.22.4.0", {"center": v(558.8, 101.6) * mm, "radius": 8.47 * mm, "construction": true});
            skCircle(sketch, "E14.22.4.1", {"center": v(558.8, 101.6) * mm, "radius": 2.38 * mm});
            skCircle(sketch, "E14.22.5.0", {"center": v(558.8, 127) * mm, "radius": 8.47 * mm, "construction": true});
            skCircle(sketch, "E14.22.5.1", {"center": v(558.8, 127) * mm, "radius": 2.38 * mm});
            skCircle(sketch, "E14.22.6.0", {"center": v(558.8, 152.4) * mm, "radius": 8.47 * mm, "construction": true});
            skCircle(sketch, "E14.22.6.1", {"center": v(558.8, 152.4) * mm, "radius": 2.38 * mm});
            skCircle(sketch, "E14.22.7.0", {"center": v(558.8, 177.8) * mm, "radius": 8.47 * mm, "construction": true});
            skCircle(sketch, "E14.22.7.1", {"center": v(558.8, 177.8) * mm, "radius": 2.38 * mm});
            skCircle(sketch, "E14.22.8.0", {"center": v(558.8, 203.2) * mm, "radius": 8.47 * mm, "construction": true});
            skCircle(sketch, "E14.22.8.1", {"center": v(558.8, 203.2) * mm, "radius": 2.38 * mm});
            skCircle(sketch, "E14.22.9.0", {"center": v(558.8, 228.6) * mm, "radius": 8.47 * mm, "construction": true});
            skCircle(sketch, "E14.22.9.1", {"center": v(558.8, 228.6) * mm, "radius": 2.38 * mm});
            skCircle(sketch, "E14.22.10.0", {"center": v(558.8, 254) * mm, "radius": 8.47 * mm, "construction": true});
            skCircle(sketch, "E14.22.10.1", {"center": v(558.8, 254) * mm, "radius": 2.38 * mm});
            skCircle(sketch, "E14.22.11.0", {"center": v(558.8, 279.4) * mm, "radius": 8.47 * mm, "construction": true});
            skCircle(sketch, "E14.22.11.1", {"center": v(558.8, 279.4) * mm, "radius": 2.38 * mm});
            skCircle(sketch, "E14.22.12.0", {"center": v(558.8, 304.8) * mm, "radius": 8.47 * mm, "construction": true});
            skCircle(sketch, "E14.22.12.1", {"center": v(558.8, 304.8) * mm, "radius": 2.38 * mm});
            skCircle(sketch, "E14.22.13.0", {"center": v(558.8, 330.2) * mm, "radius": 8.47 * mm, "construction": true});
            skCircle(sketch, "E14.22.13.1", {"center": v(558.8, 330.2) * mm, "radius": 2.38 * mm});
            skCircle(sketch, "E14.22.14.0", {"center": v(558.8, 355.6) * mm, "radius": 8.47 * mm, "construction": true});
            skCircle(sketch, "E14.22.14.1", {"center": v(558.8, 355.6) * mm, "radius": 2.38 * mm});
            skCircle(sketch, "E14.22.15.0", {"center": v(558.8, 381) * mm, "radius": 8.47 * mm, "construction": true});
            skCircle(sketch, "E14.22.15.1", {"center": v(558.8, 381) * mm, "radius": 2.38 * mm});
            skCircle(sketch, "E14.23.0.0", {"center": v(584.2, 0) * mm, "radius": 8.47 * mm, "construction": true});
            skCircle(sketch, "E14.23.0.1", {"center": v(584.2, 0) * mm, "radius": 2.38 * mm});
            skCircle(sketch, "E14.23.1.0", {"center": v(584.2, 25.4) * mm, "radius": 8.47 * mm, "construction": true});
            skCircle(sketch, "E14.23.1.1", {"center": v(584.2, 25.4) * mm, "radius": 2.38 * mm});
            skCircle(sketch, "E14.23.2.0", {"center": v(584.2, 50.8) * mm, "radius": 8.47 * mm, "construction": true});
            skCircle(sketch, "E14.23.2.1", {"center": v(584.2, 50.8) * mm, "radius": 2.38 * mm});
            skCircle(sketch, "E14.23.3.0", {"center": v(584.2, 76.2) * mm, "radius": 8.47 * mm, "construction": true});
            skCircle(sketch, "E14.23.3.1", {"center": v(584.2, 76.2) * mm, "radius": 2.38 * mm});
            skCircle(sketch, "E14.23.4.0", {"center": v(584.2, 101.6) * mm, "radius": 8.47 * mm, "construction": true});
            skCircle(sketch, "E14.23.4.1", {"center": v(584.2, 101.6) * mm, "radius": 2.38 * mm});
            skCircle(sketch, "E14.23.5.0", {"center": v(584.2, 127) * mm, "radius": 8.47 * mm, "construction": true});
            skCircle(sketch, "E14.23.5.1", {"center": v(584.2, 127) * mm, "radius": 2.38 * mm});
            skCircle(sketch, "E14.23.6.0", {"center": v(584.2, 152.4) * mm, "radius": 8.47 * mm, "construction": true});
            skCircle(sketch, "E14.23.6.1", {"center": v(584.2, 152.4) * mm, "radius": 2.38 * mm});
            skCircle(sketch, "E14.23.7.0", {"center": v(584.2, 177.8) * mm, "radius": 8.47 * mm, "construction": true});
            skCircle(sketch, "E14.23.7.1", {"center": v(584.2, 177.8) * mm, "radius": 2.38 * mm});
            skCircle(sketch, "E14.23.8.0", {"center": v(584.2, 203.2) * mm, "radius": 8.47 * mm, "construction": true});
            skCircle(sketch, "E14.23.8.1", {"center": v(584.2, 203.2) * mm, "radius": 2.38 * mm});
            skCircle(sketch, "E14.23.9.0", {"center": v(584.2, 228.6) * mm, "radius": 8.47 * mm, "construction": true});
            skCircle(sketch, "E14.23.9.1", {"center": v(584.2, 228.6) * mm, "radius": 2.38 * mm});
            skCircle(sketch, "E14.23.10.0", {"center": v(584.2, 254) * mm, "radius": 8.47 * mm, "construction": true});
            skCircle(sketch, "E14.23.10.1", {"center": v(584.2, 254) * mm, "radius": 2.38 * mm});
            skCircle(sketch, "E14.23.11.0", {"center": v(584.2, 279.4) * mm, "radius": 8.47 * mm, "construction": true});
            skCircle(sketch, "E14.23.11.1", {"center": v(584.2, 279.4) * mm, "radius": 2.38 * mm});
            skCircle(sketch, "E14.23.12.0", {"center": v(584.2, 304.8) * mm, "radius": 8.47 * mm, "construction": true});
            skCircle(sketch, "E14.23.12.1", {"center": v(584.2, 304.8) * mm, "radius": 2.38 * mm});
            skCircle(sketch, "E14.23.13.0", {"center": v(584.2, 330.2) * mm, "radius": 8.47 * mm, "construction": true});
            skCircle(sketch, "E14.23.13.1", {"center": v(584.2, 330.2) * mm, "radius": 2.38 * mm});
            skCircle(sketch, "E14.23.14.0", {"center": v(584.2, 355.6) * mm, "radius": 8.47 * mm, "construction": true});
            skCircle(sketch, "E14.23.14.1", {"center": v(584.2, 355.6) * mm, "radius": 2.38 * mm});
            skCircle(sketch, "E14.23.15.0", {"center": v(584.2, 381) * mm, "radius": 8.47 * mm, "construction": true});
            skCircle(sketch, "E14.23.15.1", {"center": v(584.2, 381) * mm, "radius": 2.38 * mm});
            skCircle(sketch, "E14.24.0.0", {"center": v(609.6, 0) * mm, "radius": 8.47 * mm, "construction": true});
            skCircle(sketch, "E14.24.0.1", {"center": v(609.6, 0) * mm, "radius": 2.38 * mm});
            skCircle(sketch, "E14.24.1.0", {"center": v(609.6, 25.4) * mm, "radius": 8.47 * mm, "construction": true});
            skCircle(sketch, "E14.24.1.1", {"center": v(609.6, 25.4) * mm, "radius": 2.38 * mm});
            skCircle(sketch, "E14.24.2.0", {"center": v(609.6, 50.8) * mm, "radius": 8.47 * mm, "construction": true});
            skCircle(sketch, "E14.24.2.1", {"center": v(609.6, 50.8) * mm, "radius": 2.38 * mm});
            skCircle(sketch, "E14.24.3.0", {"center": v(609.6, 76.2) * mm, "radius": 8.47 * mm, "construction": true});
            skCircle(sketch, "E14.24.3.1", {"center": v(609.6, 76.2) * mm, "radius": 2.38 * mm});
            skCircle(sketch, "E14.24.4.0", {"center": v(609.6, 101.6) * mm, "radius": 8.47 * mm, "construction": true});
            skCircle(sketch, "E14.24.4.1", {"center": v(609.6, 101.6) * mm, "radius": 2.38 * mm});
            skCircle(sketch, "E14.24.5.0", {"center": v(609.6, 127) * mm, "radius": 8.47 * mm, "construction": true});
            skCircle(sketch, "E14.24.5.1", {"center": v(609.6, 127) * mm, "radius": 2.38 * mm});
            skCircle(sketch, "E14.24.6.0", {"center": v(609.6, 152.4) * mm, "radius": 8.47 * mm, "construction": true});
            skCircle(sketch, "E14.24.6.1", {"center": v(609.6, 152.4) * mm, "radius": 2.38 * mm});
            skCircle(sketch, "E14.24.7.0", {"center": v(609.6, 177.8) * mm, "radius": 8.47 * mm, "construction": true});
            skCircle(sketch, "E14.24.7.1", {"center": v(609.6, 177.8) * mm, "radius": 2.38 * mm});
            skCircle(sketch, "E14.24.8.0", {"center": v(609.6, 203.2) * mm, "radius": 8.47 * mm, "construction": true});
            skCircle(sketch, "E14.24.8.1", {"center": v(609.6, 203.2) * mm, "radius": 2.38 * mm});
            skCircle(sketch, "E14.24.9.0", {"center": v(609.6, 228.6) * mm, "radius": 8.47 * mm, "construction": true});
            skCircle(sketch, "E14.24.9.1", {"center": v(609.6, 228.6) * mm, "radius": 2.38 * mm});
            skCircle(sketch, "E14.24.10.0", {"center": v(609.6, 254) * mm, "radius": 8.47 * mm, "construction": true});
            skCircle(sketch, "E14.24.10.1", {"center": v(609.6, 254) * mm, "radius": 2.38 * mm});
            skCircle(sketch, "E14.24.11.0", {"center": v(609.6, 279.4) * mm, "radius": 8.47 * mm, "construction": true});
            skCircle(sketch, "E14.24.11.1", {"center": v(609.6, 279.4) * mm, "radius": 2.38 * mm});
            skCircle(sketch, "E14.24.12.0", {"center": v(609.6, 304.8) * mm, "radius": 8.47 * mm, "construction": true});
            skCircle(sketch, "E14.24.12.1", {"center": v(609.6, 304.8) * mm, "radius": 2.38 * mm});
            skCircle(sketch, "E14.24.13.0", {"center": v(609.6, 330.2) * mm, "radius": 8.47 * mm, "construction": true});
            skCircle(sketch, "E14.24.13.1", {"center": v(609.6, 330.2) * mm, "radius": 2.38 * mm});
            skCircle(sketch, "E14.24.14.0", {"center": v(609.6, 355.6) * mm, "radius": 8.47 * mm, "construction": true});
            skCircle(sketch, "E14.24.14.1", {"center": v(609.6, 355.6) * mm, "radius": 2.38 * mm});
            skCircle(sketch, "E14.24.15.0", {"center": v(609.6, 381) * mm, "radius": 8.47 * mm, "construction": true});
            skCircle(sketch, "E14.24.15.1", {"center": v(609.6, 381) * mm, "radius": 2.38 * mm});
            skCircle(sketch, "E14.25.0.0", {"center": v(635, 0) * mm, "radius": 8.47 * mm, "construction": true});
            skCircle(sketch, "E14.25.0.1", {"center": v(635, 0) * mm, "radius": 2.38 * mm});
            skCircle(sketch, "E14.25.1.0", {"center": v(635, 25.4) * mm, "radius": 8.47 * mm, "construction": true});
            skCircle(sketch, "E14.25.1.1", {"center": v(635, 25.4) * mm, "radius": 2.38 * mm});
            skCircle(sketch, "E14.25.2.0", {"center": v(635, 50.8) * mm, "radius": 8.47 * mm, "construction": true});
            skCircle(sketch, "E14.25.2.1", {"center": v(635, 50.8) * mm, "radius": 2.38 * mm});
            skCircle(sketch, "E14.25.3.0", {"center": v(635, 76.2) * mm, "radius": 8.47 * mm, "construction": true});
            skCircle(sketch, "E14.25.3.1", {"center": v(635, 76.2) * mm, "radius": 2.38 * mm});
            skCircle(sketch, "E14.25.4.0", {"center": v(635, 101.6) * mm, "radius": 8.47 * mm, "construction": true});
            skCircle(sketch, "E14.25.4.1", {"center": v(635, 101.6) * mm, "radius": 2.38 * mm});
            skCircle(sketch, "E14.25.5.0", {"center": v(635, 127) * mm, "radius": 8.47 * mm, "construction": true});
            skCircle(sketch, "E14.25.5.1", {"center": v(635, 127) * mm, "radius": 2.38 * mm});
            skCircle(sketch, "E14.25.6.0", {"center": v(635, 152.4) * mm, "radius": 8.47 * mm, "construction": true});
            skCircle(sketch, "E14.25.6.1", {"center": v(635, 152.4) * mm, "radius": 2.38 * mm});
            skCircle(sketch, "E14.25.7.0", {"center": v(635, 177.8) * mm, "radius": 8.47 * mm, "construction": true});
            skCircle(sketch, "E14.25.7.1", {"center": v(635, 177.8) * mm, "radius": 2.38 * mm});
            skCircle(sketch, "E14.25.8.0", {"center": v(635, 203.2) * mm, "radius": 8.47 * mm, "construction": true});
            skCircle(sketch, "E14.25.8.1", {"center": v(635, 203.2) * mm, "radius": 2.38 * mm});
            skCircle(sketch, "E14.25.9.0", {"center": v(635, 228.6) * mm, "radius": 8.47 * mm, "construction": true});
            skCircle(sketch, "E14.25.9.1", {"center": v(635, 228.6) * mm, "radius": 2.38 * mm});
            skCircle(sketch, "E14.25.10.0", {"center": v(635, 254) * mm, "radius": 8.47 * mm, "construction": true});
            skCircle(sketch, "E14.25.10.1", {"center": v(635, 254) * mm, "radius": 2.38 * mm});
            skCircle(sketch, "E14.25.11.0", {"center": v(635, 279.4) * mm, "radius": 8.47 * mm, "construction": true});
            skCircle(sketch, "E14.25.11.1", {"center": v(635, 279.4) * mm, "radius": 2.38 * mm});
            skCircle(sketch, "E14.25.12.0", {"center": v(635, 304.8) * mm, "radius": 8.47 * mm, "construction": true});
            skCircle(sketch, "E14.25.12.1", {"center": v(635, 304.8) * mm, "radius": 2.38 * mm});
            skCircle(sketch, "E14.25.13.0", {"center": v(635, 330.2) * mm, "radius": 8.47 * mm, "construction": true});
            skCircle(sketch, "E14.25.13.1", {"center": v(635, 330.2) * mm, "radius": 2.38 * mm});
            skCircle(sketch, "E14.25.14.0", {"center": v(635, 355.6) * mm, "radius": 8.47 * mm, "construction": true});
            skCircle(sketch, "E14.25.14.1", {"center": v(635, 355.6) * mm, "radius": 2.38 * mm});
            skCircle(sketch, "E14.25.15.0", {"center": v(635, 381) * mm, "radius": 8.47 * mm, "construction": true});
            skCircle(sketch, "E14.25.15.1", {"center": v(635, 381) * mm, "radius": 2.38 * mm});
            skCircle(sketch, "E14.26.0.0", {"center": v(660.4, 0) * mm, "radius": 8.47 * mm, "construction": true});
            skCircle(sketch, "E14.26.0.1", {"center": v(660.4, 0) * mm, "radius": 2.38 * mm});
            skCircle(sketch, "E14.26.1.0", {"center": v(660.4, 25.4) * mm, "radius": 8.47 * mm, "construction": true});
            skCircle(sketch, "E14.26.1.1", {"center": v(660.4, 25.4) * mm, "radius": 2.38 * mm});
            skCircle(sketch, "E14.26.2.0", {"center": v(660.4, 50.8) * mm, "radius": 8.47 * mm, "construction": true});
            skCircle(sketch, "E14.26.2.1", {"center": v(660.4, 50.8) * mm, "radius": 2.38 * mm});
            skCircle(sketch, "E14.26.3.0", {"center": v(660.4, 76.2) * mm, "radius": 8.47 * mm, "construction": true});
            skCircle(sketch, "E14.26.3.1", {"center": v(660.4, 76.2) * mm, "radius": 2.38 * mm});
            skCircle(sketch, "E14.26.4.0", {"center": v(660.4, 101.6) * mm, "radius": 8.47 * mm, "construction": true});
            skCircle(sketch, "E14.26.4.1", {"center": v(660.4, 101.6) * mm, "radius": 2.38 * mm});
            skCircle(sketch, "E14.26.5.0", {"center": v(660.4, 127) * mm, "radius": 8.47 * mm, "construction": true});
            skCircle(sketch, "E14.26.5.1", {"center": v(660.4, 127) * mm, "radius": 2.38 * mm});
            skCircle(sketch, "E14.26.6.0", {"center": v(660.4, 152.4) * mm, "radius": 8.47 * mm, "construction": true});
            skCircle(sketch, "E14.26.6.1", {"center": v(660.4, 152.4) * mm, "radius": 2.38 * mm});
            skCircle(sketch, "E14.26.7.0", {"center": v(660.4, 177.8) * mm, "radius": 8.47 * mm, "construction": true});
            skCircle(sketch, "E14.26.7.1", {"center": v(660.4, 177.8) * mm, "radius": 2.38 * mm});
            skCircle(sketch, "E14.26.8.0", {"center": v(660.4, 203.2) * mm, "radius": 8.47 * mm, "construction": true});
            skCircle(sketch, "E14.26.8.1", {"center": v(660.4, 203.2) * mm, "radius": 2.38 * mm});
            skCircle(sketch, "E14.26.9.0", {"center": v(660.4, 228.6) * mm, "radius": 8.47 * mm, "construction": true});
            skCircle(sketch, "E14.26.9.1", {"center": v(660.4, 228.6) * mm, "radius": 2.38 * mm});
            skCircle(sketch, "E14.26.10.0", {"center": v(660.4, 254) * mm, "radius": 8.47 * mm, "construction": true});
            skCircle(sketch, "E14.26.10.1", {"center": v(660.4, 254) * mm, "radius": 2.38 * mm});
            skCircle(sketch, "E14.26.11.0", {"center": v(660.4, 279.4) * mm, "radius": 8.47 * mm, "construction": true});
            skCircle(sketch, "E14.26.11.1", {"center": v(660.4, 279.4) * mm, "radius": 2.38 * mm});
            skCircle(sketch, "E14.26.12.0", {"center": v(660.4, 304.8) * mm, "radius": 8.47 * mm, "construction": true});
            skCircle(sketch, "E14.26.12.1", {"center": v(660.4, 304.8) * mm, "radius": 2.38 * mm});
            skCircle(sketch, "E14.26.13.0", {"center": v(660.4, 330.2) * mm, "radius": 8.47 * mm, "construction": true});
            skCircle(sketch, "E14.26.13.1", {"center": v(660.4, 330.2) * mm, "radius": 2.38 * mm});
            skCircle(sketch, "E14.26.14.0", {"center": v(660.4, 355.6) * mm, "radius": 8.47 * mm, "construction": true});
            skCircle(sketch, "E14.26.14.1", {"center": v(660.4, 355.6) * mm, "radius": 2.38 * mm});
            skCircle(sketch, "E14.26.15.0", {"center": v(660.4, 381) * mm, "radius": 8.47 * mm, "construction": true});
            skCircle(sketch, "E14.26.15.1", {"center": v(660.4, 381) * mm, "radius": 2.38 * mm});
            skCircle(sketch, "E14.27.0.0", {"center": v(685.8, 0) * mm, "radius": 8.47 * mm, "construction": true});
            skCircle(sketch, "E14.27.0.1", {"center": v(685.8, 0) * mm, "radius": 2.38 * mm});
            skCircle(sketch, "E14.27.1.0", {"center": v(685.8, 25.4) * mm, "radius": 8.47 * mm, "construction": true});
            skCircle(sketch, "E14.27.1.1", {"center": v(685.8, 25.4) * mm, "radius": 2.38 * mm});
            skCircle(sketch, "E14.27.2.0", {"center": v(685.8, 50.8) * mm, "radius": 8.47 * mm, "construction": true});
            skCircle(sketch, "E14.27.2.1", {"center": v(685.8, 50.8) * mm, "radius": 2.38 * mm});
            skCircle(sketch, "E14.27.3.0", {"center": v(685.8, 76.2) * mm, "radius": 8.47 * mm, "construction": true});
            skCircle(sketch, "E14.27.3.1", {"center": v(685.8, 76.2) * mm, "radius": 2.38 * mm});
            skCircle(sketch, "E14.27.4.0", {"center": v(685.8, 101.6) * mm, "radius": 8.47 * mm, "construction": true});
            skCircle(sketch, "E14.27.4.1", {"center": v(685.8, 101.6) * mm, "radius": 2.38 * mm});
            skCircle(sketch, "E14.27.5.0", {"center": v(685.8, 127) * mm, "radius": 8.47 * mm, "construction": true});
            skCircle(sketch, "E14.27.5.1", {"center": v(685.8, 127) * mm, "radius": 2.38 * mm});
            skCircle(sketch, "E14.27.6.0", {"center": v(685.8, 152.4) * mm, "radius": 8.47 * mm, "construction": true});
            skCircle(sketch, "E14.27.6.1", {"center": v(685.8, 152.4) * mm, "radius": 2.38 * mm});
            skCircle(sketch, "E14.27.7.0", {"center": v(685.8, 177.8) * mm, "radius": 8.47 * mm, "construction": true});
            skCircle(sketch, "E14.27.7.1", {"center": v(685.8, 177.8) * mm, "radius": 2.38 * mm});
            skCircle(sketch, "E14.27.8.0", {"center": v(685.8, 203.2) * mm, "radius": 8.47 * mm, "construction": true});
            skCircle(sketch, "E14.27.8.1", {"center": v(685.8, 203.2) * mm, "radius": 2.38 * mm});
            skCircle(sketch, "E14.27.9.0", {"center": v(685.8, 228.6) * mm, "radius": 8.47 * mm, "construction": true});
            skCircle(sketch, "E14.27.9.1", {"center": v(685.8, 228.6) * mm, "radius": 2.38 * mm});
            skCircle(sketch, "E14.27.10.0", {"center": v(685.8, 254) * mm, "radius": 8.47 * mm, "construction": true});
            skCircle(sketch, "E14.27.10.1", {"center": v(685.8, 254) * mm, "radius": 2.38 * mm});
            skCircle(sketch, "E14.27.11.0", {"center": v(685.8, 279.4) * mm, "radius": 8.47 * mm, "construction": true});
            skCircle(sketch, "E14.27.11.1", {"center": v(685.8, 279.4) * mm, "radius": 2.38 * mm});
            skCircle(sketch, "E14.27.12.0", {"center": v(685.8, 304.8) * mm, "radius": 8.47 * mm, "construction": true});
            skCircle(sketch, "E14.27.12.1", {"center": v(685.8, 304.8) * mm, "radius": 2.38 * mm});
            skCircle(sketch, "E14.27.13.0", {"center": v(685.8, 330.2) * mm, "radius": 8.47 * mm, "construction": true});
            skCircle(sketch, "E14.27.13.1", {"center": v(685.8, 330.2) * mm, "radius": 2.38 * mm});
            skCircle(sketch, "E14.27.14.0", {"center": v(685.8, 355.6) * mm, "radius": 8.47 * mm, "construction": true});
            skCircle(sketch, "E14.27.14.1", {"center": v(685.8, 355.6) * mm, "radius": 2.38 * mm});
            skCircle(sketch, "E14.27.15.0", {"center": v(685.8, 381) * mm, "radius": 8.47 * mm, "construction": true});
            skCircle(sketch, "E14.27.15.1", {"center": v(685.8, 381) * mm, "radius": 2.38 * mm});
            skLineSegment(sketch, "E14.direction1", {"start": v(0, 0) * mm, "end": v(25.4, 0) * mm, "construction": true});
            skLineSegment(sketch, "E14.direction2", {"start": v(0, 0) * mm, "end": v(0, 25.4) * mm, "construction": true});
            skLineSegment(sketch, "E15", {"start": v(-8.47, 0) * mm, "end": v(-8.47, 381) * mm});
            skLineSegment(sketch, "E16", {"start": v(0, 389.47) * mm, "end": v(685.8, 389.47) * mm});
            skLineSegment(sketch, "E17", {"start": v(694.27, 381) * mm, "end": v(694.27, 0) * mm});
            skLineSegment(sketch, "E18", {"start": v(685.8, -8.47) * mm, "end": v(0, -8.47) * mm});
            skArc(sketch, "E19", {"start": v(0, 389.47) * mm, "mid": v(-5.99, 386.99) * mm, "end": v(-8.47, 381) * mm});
            skArc(sketch, "E20", {"start": v(694.27, 381) * mm, "mid": v(691.79, 386.99) * mm, "end": v(685.8, 389.47) * mm});
            skArc(sketch, "E21", {"start": v(685.8, -8.47) * mm, "mid": v(691.79, -5.99) * mm, "end": v(694.27, 0) * mm});
            skSolve(sketch);
        }
        {
            var Q0;
            Q0=makeQuery(id+"F3.imprint","IMPRINT",FACE,{"disambiguationData":[TD([[makeQuery(id+"F3.imprint","IMPRINT",EDGE,{"derivedFrom":sQuery(id+"F3.wireOp",EDGE,"E12.0")}),-1.0]])]});
            var Q1;
            Q1=sQuery(id+"F2.wireOp",VERTEX,"E11.top.start");
            extrude(context, id + "F4", {"entities" : qUnion([Q0]), "endBound" : BoundingType.UP_TO_VERTEX, "oppositeDirection" : true, "endBoundEntityVertex" : qUnion([Q1]), "depth" : 25.4 * mm});
        }
        {
            var Q0;
            Q0=makeQuery(id+"F1.imprint","IMPRINT",FACE,{"disambiguationData":[TD([[makeQuery(id+"F1.imprint","IMPRINT",EDGE,{"derivedFrom":sQuery(id+"F1.wireOp",EDGE,"E0")}),-1.0]])]});
            var Q1;
            Q1=sQuery(id+"F2.wireOp",VERTEX,"E11.left.end");
            extrude(context, id + "F5", {"entities" : qUnion([Q0]), "endBound" : BoundingType.UP_TO_VERTEX, "oppositeDirection" : true, "endBoundEntityVertex" : qUnion([Q1]), "depth" : 25.4 * mm});
        }
        {
            var Q0;
            Q0=qCreatedBy(makeId("Top.planeOp"),FACE);
            var sketch = newSketch(context, id + "F6", { "sketchPlane" : qUnion([Q0])});
            skCircle(sketch, "E22", {"center": v(622.3, 38.1) * mm, "radius": 16.17 * mm, "construction": true});
            skCircle(sketch, "E23", {"center": v(63.5, 38.1) * mm, "radius": 33.34 * mm, "construction": true});
            skCircle(sketch, "E24", {"center": v(103.19, 38.1) * mm, "radius": 6.35 * mm, "construction": true});
            skCircle(sketch, "E25", {"center": v(63.5, 38.1) * mm, "radius": 16.17 * mm, "construction": true});
            skLineSegment(sketch, "E26", {"start": v(63.5, 54.27) * mm, "end": v(622.3, 54.27) * mm, "construction": true});
            skLineSegment(sketch, "E27", {"start": v(63.5, 21.93) * mm, "end": v(622.3, 21.93) * mm, "construction": true});
            skCircle(sketch, "E28", {"center": v(103.19, 38.1) * mm, "radius": 19.05 * mm, "construction": true});
            skLineSegment(sketch, "E29", {"start": v(0, -11.68) * mm, "end": v(685.8, -11.68) * mm, "construction": true});
            skLineSegment(sketch, "E30", {"start": v(342.9, -11.68) * mm, "end": v(342.9, 21.93) * mm, "construction": true});
            skLineSegment(sketch, "E31", {"start": v(0, 50.8) * mm, "end": v(0, 25.4) * mm, "construction": true});
            skPoint(sketch, "E32", {"position": v(0, 38.1) * mm});
            skSolve(sketch);
        }
        {
            var Q0;
            Q0=qCreatedBy(makeId("Top.planeOp"),FACE);
            var sketch = newSketch(context, id + "F7", { "sketchPlane" : qUnion([Q0])});
            skCircle(sketch, "E33", {"center": v(63.5, 38.1) * mm, "radius": 4.76 * mm});
            skCircle(sketch, "E34", {"center": v(103.19, 38.1) * mm, "radius": 6.73 * mm});
            skCircle(sketch, "E35", {"center": v(96.69, 26.84) * mm, "radius": 1.59 * mm});
            skCircle(sketch, "E36", {"center": v(90.19, 38.1) * mm, "radius": 1.59 * mm});
            skCircle(sketch, "E37", {"center": v(96.69, 49.36) * mm, "radius": 1.59 * mm});
            skLineSegment(sketch, "E38", {"start": v(96.69, 26.84) * mm, "end": v(103.19, 38.1) * mm, "construction": true});
            skLineSegment(sketch, "E39", {"start": v(103.19, 38.1) * mm, "end": v(90.19, 38.1) * mm, "construction": true});
            skLineSegment(sketch, "E40", {"start": v(103.19, 38.1) * mm, "end": v(96.69, 49.36) * mm, "construction": true});
            skLineSegment(sketch, "E41", {"start": v(103.19, 38.1) * mm, "end": v(116.19, 38.1) * mm, "construction": true});
            skCircle(sketch, "E42", {"center": v(116.19, 38.1) * mm, "radius": 1.59 * mm});
            skCircle(sketch, "E43.0", {"center": v(0, 0) * mm, "radius": 8.47 * mm, "construction": true});
            skCircle(sketch, "E43.1", {"center": v(0, 0) * mm, "radius": 2.38 * mm, "construction": true});
            skCircle(sketch, "E44.0.1.0", {"center": v(0, 25.4) * mm, "radius": 8.47 * mm, "construction": true});
            skCircle(sketch, "E44.0.1.1", {"center": v(0, 25.4) * mm, "radius": 2.38 * mm, "construction": true});
            skCircle(sketch, "E44.0.2.0", {"center": v(0, 50.8) * mm, "radius": 8.47 * mm, "construction": true});
            skCircle(sketch, "E44.0.2.1", {"center": v(0, 50.8) * mm, "radius": 2.38 * mm, "construction": true});
            skCircle(sketch, "E44.0.3.0", {"center": v(0, 76.2) * mm, "radius": 8.47 * mm, "construction": true});
            skCircle(sketch, "E44.0.3.1", {"center": v(0, 76.2) * mm, "radius": 2.38 * mm, "construction": true});
            skCircle(sketch, "E44.1.0.0", {"center": v(25.4, 0) * mm, "radius": 8.47 * mm, "construction": true});
            skCircle(sketch, "E44.1.0.1", {"center": v(25.4, 0) * mm, "radius": 2.38 * mm, "construction": true});
            skCircle(sketch, "E44.1.1.0", {"center": v(25.4, 25.4) * mm, "radius": 8.47 * mm, "construction": true});
            skCircle(sketch, "E44.1.1.1", {"center": v(25.4, 25.4) * mm, "radius": 2.38 * mm, "construction": true});
            skCircle(sketch, "E44.1.2.0", {"center": v(25.4, 50.8) * mm, "radius": 8.47 * mm, "construction": true});
            skCircle(sketch, "E44.1.2.1", {"center": v(25.4, 50.8) * mm, "radius": 2.38 * mm, "construction": true});
            skCircle(sketch, "E44.1.3.0", {"center": v(25.4, 76.2) * mm, "radius": 8.47 * mm, "construction": true});
            skCircle(sketch, "E44.1.3.1", {"center": v(25.4, 76.2) * mm, "radius": 2.38 * mm, "construction": true});
            skCircle(sketch, "E44.2.0.0", {"center": v(50.8, 0) * mm, "radius": 8.47 * mm, "construction": true});
            skCircle(sketch, "E44.2.0.1", {"center": v(50.8, 0) * mm, "radius": 2.38 * mm});
            skCircle(sketch, "E44.2.1.0", {"center": v(50.8, 25.4) * mm, "radius": 8.47 * mm, "construction": true});
            skCircle(sketch, "E44.2.1.1", {"center": v(50.8, 25.4) * mm, "radius": 2.38 * mm});
            skCircle(sketch, "E44.2.2.0", {"center": v(50.8, 50.8) * mm, "radius": 8.47 * mm, "construction": true});
            skCircle(sketch, "E44.2.2.1", {"center": v(50.8, 50.8) * mm, "radius": 2.38 * mm});
            skCircle(sketch, "E44.2.3.0", {"center": v(50.8, 76.2) * mm, "radius": 8.47 * mm, "construction": true});
            skCircle(sketch, "E44.2.3.1", {"center": v(50.8, 76.2) * mm, "radius": 2.38 * mm});
            skCircle(sketch, "E44.3.0.0", {"center": v(76.2, 0) * mm, "radius": 8.47 * mm, "construction": true});
            skCircle(sketch, "E44.3.0.1", {"center": v(76.2, 0) * mm, "radius": 2.38 * mm});
            skCircle(sketch, "E44.3.1.0", {"center": v(76.2, 25.4) * mm, "radius": 8.47 * mm, "construction": true});
            skCircle(sketch, "E44.3.1.1", {"center": v(76.2, 25.4) * mm, "radius": 2.38 * mm});
            skCircle(sketch, "E44.3.2.0", {"center": v(76.2, 50.8) * mm, "radius": 8.47 * mm, "construction": true});
            skCircle(sketch, "E44.3.2.1", {"center": v(76.2, 50.8) * mm, "radius": 2.38 * mm});
            skCircle(sketch, "E44.3.3.0", {"center": v(76.2, 76.2) * mm, "radius": 8.47 * mm, "construction": true});
            skCircle(sketch, "E44.3.3.1", {"center": v(76.2, 76.2) * mm, "radius": 2.38 * mm});
            skCircle(sketch, "E44.4.0.0", {"center": v(101.6, 0) * mm, "radius": 8.47 * mm, "construction": true});
            skCircle(sketch, "E44.4.0.1", {"center": v(101.6, 0) * mm, "radius": 2.38 * mm});
            skCircle(sketch, "E44.4.1.0", {"center": v(101.6, 25.4) * mm, "radius": 8.47 * mm, "construction": true});
            skCircle(sketch, "E44.4.1.1", {"center": v(101.6, 25.4) * mm, "radius": 2.38 * mm, "construction": true});
            skCircle(sketch, "E44.4.2.0", {"center": v(101.6, 50.8) * mm, "radius": 8.47 * mm, "construction": true});
            skCircle(sketch, "E44.4.2.1", {"center": v(101.6, 50.8) * mm, "radius": 2.38 * mm, "construction": true});
            skCircle(sketch, "E44.4.3.0", {"center": v(101.6, 76.2) * mm, "radius": 8.47 * mm, "construction": true});
            skCircle(sketch, "E44.4.3.1", {"center": v(101.6, 76.2) * mm, "radius": 2.38 * mm});
            skCircle(sketch, "E44.5.0.0", {"center": v(127, 0) * mm, "radius": 8.47 * mm, "construction": true});
            skCircle(sketch, "E44.5.0.1", {"center": v(127, 0) * mm, "radius": 2.38 * mm});
            skCircle(sketch, "E44.5.1.0", {"center": v(127, 25.4) * mm, "radius": 8.47 * mm, "construction": true});
            skCircle(sketch, "E44.5.1.1", {"center": v(127, 25.4) * mm, "radius": 2.38 * mm});
            skCircle(sketch, "E44.5.2.0", {"center": v(127, 50.8) * mm, "radius": 8.47 * mm, "construction": true});
            skCircle(sketch, "E44.5.2.1", {"center": v(127, 50.8) * mm, "radius": 2.38 * mm});
            skCircle(sketch, "E44.5.3.0", {"center": v(127, 76.2) * mm, "radius": 8.47 * mm, "construction": true});
            skCircle(sketch, "E44.5.3.1", {"center": v(127, 76.2) * mm, "radius": 2.38 * mm});
            skCircle(sketch, "E44.6.0.0", {"center": v(152.4, 0) * mm, "radius": 8.47 * mm, "construction": true});
            skCircle(sketch, "E44.6.0.1", {"center": v(152.4, 0) * mm, "radius": 2.38 * mm, "construction": true});
            skCircle(sketch, "E44.6.1.0", {"center": v(152.4, 25.4) * mm, "radius": 8.47 * mm, "construction": true});
            skCircle(sketch, "E44.6.1.1", {"center": v(152.4, 25.4) * mm, "radius": 2.38 * mm, "construction": true});
            skCircle(sketch, "E44.6.2.0", {"center": v(152.4, 50.8) * mm, "radius": 8.47 * mm, "construction": true});
            skCircle(sketch, "E44.6.2.1", {"center": v(152.4, 50.8) * mm, "radius": 2.38 * mm, "construction": true});
            skCircle(sketch, "E44.6.3.0", {"center": v(152.4, 76.2) * mm, "radius": 8.47 * mm, "construction": true});
            skCircle(sketch, "E44.6.3.1", {"center": v(152.4, 76.2) * mm, "radius": 2.38 * mm, "construction": true});
            skCircle(sketch, "E44.7.0.0", {"center": v(177.8, 0) * mm, "radius": 8.47 * mm, "construction": true});
            skCircle(sketch, "E44.7.0.1", {"center": v(177.8, 0) * mm, "radius": 2.38 * mm, "construction": true});
            skCircle(sketch, "E44.7.1.0", {"center": v(177.8, 25.4) * mm, "radius": 8.47 * mm, "construction": true});
            skCircle(sketch, "E44.7.1.1", {"center": v(177.8, 25.4) * mm, "radius": 2.38 * mm, "construction": true});
            skCircle(sketch, "E44.7.2.0", {"center": v(177.8, 50.8) * mm, "radius": 8.47 * mm, "construction": true});
            skCircle(sketch, "E44.7.2.1", {"center": v(177.8, 50.8) * mm, "radius": 2.38 * mm, "construction": true});
            skCircle(sketch, "E44.7.3.0", {"center": v(177.8, 76.2) * mm, "radius": 8.47 * mm, "construction": true});
            skCircle(sketch, "E44.7.3.1", {"center": v(177.8, 76.2) * mm, "radius": 2.38 * mm, "construction": true});
            skCircle(sketch, "E44.8.0.0", {"center": v(203.2, 0) * mm, "radius": 8.47 * mm, "construction": true});
            skCircle(sketch, "E44.8.0.1", {"center": v(203.2, 0) * mm, "radius": 2.38 * mm, "construction": true});
            skCircle(sketch, "E44.8.1.0", {"center": v(203.2, 25.4) * mm, "radius": 8.47 * mm, "construction": true});
            skCircle(sketch, "E44.8.1.1", {"center": v(203.2, 25.4) * mm, "radius": 2.38 * mm, "construction": true});
            skCircle(sketch, "E44.8.2.0", {"center": v(203.2, 50.8) * mm, "radius": 8.47 * mm, "construction": true});
            skCircle(sketch, "E44.8.2.1", {"center": v(203.2, 50.8) * mm, "radius": 2.38 * mm, "construction": true});
            skCircle(sketch, "E44.8.3.0", {"center": v(203.2, 76.2) * mm, "radius": 8.47 * mm, "construction": true});
            skCircle(sketch, "E44.8.3.1", {"center": v(203.2, 76.2) * mm, "radius": 2.38 * mm, "construction": true});
            skCircle(sketch, "E44.9.0.0", {"center": v(228.6, 0) * mm, "radius": 8.47 * mm, "construction": true});
            skCircle(sketch, "E44.9.0.1", {"center": v(228.6, 0) * mm, "radius": 2.38 * mm, "construction": true});
            skCircle(sketch, "E44.9.1.0", {"center": v(228.6, 25.4) * mm, "radius": 8.47 * mm, "construction": true});
            skCircle(sketch, "E44.9.1.1", {"center": v(228.6, 25.4) * mm, "radius": 2.38 * mm, "construction": true});
            skCircle(sketch, "E44.9.2.0", {"center": v(228.6, 50.8) * mm, "radius": 8.47 * mm, "construction": true});
            skCircle(sketch, "E44.9.2.1", {"center": v(228.6, 50.8) * mm, "radius": 2.38 * mm, "construction": true});
            skCircle(sketch, "E44.9.3.0", {"center": v(228.6, 76.2) * mm, "radius": 8.47 * mm, "construction": true});
            skCircle(sketch, "E44.9.3.1", {"center": v(228.6, 76.2) * mm, "radius": 2.38 * mm, "construction": true});
            skCircle(sketch, "E44.10.0.0", {"center": v(254, 0) * mm, "radius": 8.47 * mm, "construction": true});
            skCircle(sketch, "E44.10.0.1", {"center": v(254, 0) * mm, "radius": 2.38 * mm, "construction": true});
            skCircle(sketch, "E44.10.1.0", {"center": v(254, 25.4) * mm, "radius": 8.47 * mm, "construction": true});
            skCircle(sketch, "E44.10.1.1", {"center": v(254, 25.4) * mm, "radius": 2.38 * mm, "construction": true});
            skCircle(sketch, "E44.10.2.0", {"center": v(254, 50.8) * mm, "radius": 8.47 * mm, "construction": true});
            skCircle(sketch, "E44.10.2.1", {"center": v(254, 50.8) * mm, "radius": 2.38 * mm, "construction": true});
            skCircle(sketch, "E44.10.3.0", {"center": v(254, 76.2) * mm, "radius": 8.47 * mm, "construction": true});
            skCircle(sketch, "E44.10.3.1", {"center": v(254, 76.2) * mm, "radius": 2.38 * mm, "construction": true});
            skCircle(sketch, "E44.11.0.0", {"center": v(279.4, 0) * mm, "radius": 8.47 * mm, "construction": true});
            skCircle(sketch, "E44.11.0.1", {"center": v(279.4, 0) * mm, "radius": 2.38 * mm, "construction": true});
            skCircle(sketch, "E44.11.1.0", {"center": v(279.4, 25.4) * mm, "radius": 8.47 * mm, "construction": true});
            skCircle(sketch, "E44.11.1.1", {"center": v(279.4, 25.4) * mm, "radius": 2.38 * mm, "construction": true});
            skCircle(sketch, "E44.11.2.0", {"center": v(279.4, 50.8) * mm, "radius": 8.47 * mm, "construction": true});
            skCircle(sketch, "E44.11.2.1", {"center": v(279.4, 50.8) * mm, "radius": 2.38 * mm, "construction": true});
            skCircle(sketch, "E44.11.3.0", {"center": v(279.4, 76.2) * mm, "radius": 8.47 * mm, "construction": true});
            skCircle(sketch, "E44.11.3.1", {"center": v(279.4, 76.2) * mm, "radius": 2.38 * mm, "construction": true});
            skCircle(sketch, "E44.12.0.0", {"center": v(304.8, 0) * mm, "radius": 8.47 * mm, "construction": true});
            skCircle(sketch, "E44.12.0.1", {"center": v(304.8, 0) * mm, "radius": 2.38 * mm, "construction": true});
            skCircle(sketch, "E44.12.1.0", {"center": v(304.8, 25.4) * mm, "radius": 8.47 * mm, "construction": true});
            skCircle(sketch, "E44.12.1.1", {"center": v(304.8, 25.4) * mm, "radius": 2.38 * mm, "construction": true});
            skCircle(sketch, "E44.12.2.0", {"center": v(304.8, 50.8) * mm, "radius": 8.47 * mm, "construction": true});
            skCircle(sketch, "E44.12.2.1", {"center": v(304.8, 50.8) * mm, "radius": 2.38 * mm, "construction": true});
            skCircle(sketch, "E44.12.3.0", {"center": v(304.8, 76.2) * mm, "radius": 8.47 * mm, "construction": true});
            skCircle(sketch, "E44.12.3.1", {"center": v(304.8, 76.2) * mm, "radius": 2.38 * mm, "construction": true});
            skCircle(sketch, "E44.13.0.0", {"center": v(330.2, 0) * mm, "radius": 8.47 * mm, "construction": true});
            skCircle(sketch, "E44.13.0.1", {"center": v(330.2, 0) * mm, "radius": 2.38 * mm, "construction": true});
            skCircle(sketch, "E44.13.1.0", {"center": v(330.2, 25.4) * mm, "radius": 8.47 * mm, "construction": true});
            skCircle(sketch, "E44.13.1.1", {"center": v(330.2, 25.4) * mm, "radius": 2.38 * mm, "construction": true});
            skCircle(sketch, "E44.13.2.0", {"center": v(330.2, 50.8) * mm, "radius": 8.47 * mm, "construction": true});
            skCircle(sketch, "E44.13.2.1", {"center": v(330.2, 50.8) * mm, "radius": 2.38 * mm, "construction": true});
            skCircle(sketch, "E44.13.3.0", {"center": v(330.2, 76.2) * mm, "radius": 8.47 * mm, "construction": true});
            skCircle(sketch, "E44.13.3.1", {"center": v(330.2, 76.2) * mm, "radius": 2.38 * mm, "construction": true});
            skCircle(sketch, "E44.14.0.0", {"center": v(355.6, 0) * mm, "radius": 8.47 * mm, "construction": true});
            skCircle(sketch, "E44.14.0.1", {"center": v(355.6, 0) * mm, "radius": 2.38 * mm, "construction": true});
            skCircle(sketch, "E44.14.1.0", {"center": v(355.6, 25.4) * mm, "radius": 8.47 * mm, "construction": true});
            skCircle(sketch, "E44.14.1.1", {"center": v(355.6, 25.4) * mm, "radius": 2.38 * mm, "construction": true});
            skCircle(sketch, "E44.14.2.0", {"center": v(355.6, 50.8) * mm, "radius": 8.47 * mm, "construction": true});
            skCircle(sketch, "E44.14.2.1", {"center": v(355.6, 50.8) * mm, "radius": 2.38 * mm, "construction": true});
            skCircle(sketch, "E44.14.3.0", {"center": v(355.6, 76.2) * mm, "radius": 8.47 * mm, "construction": true});
            skCircle(sketch, "E44.14.3.1", {"center": v(355.6, 76.2) * mm, "radius": 2.38 * mm, "construction": true});
            skCircle(sketch, "E44.15.0.0", {"center": v(381, 0) * mm, "radius": 8.47 * mm, "construction": true});
            skCircle(sketch, "E44.15.0.1", {"center": v(381, 0) * mm, "radius": 2.38 * mm, "construction": true});
            skCircle(sketch, "E44.15.1.0", {"center": v(381, 25.4) * mm, "radius": 8.47 * mm, "construction": true});
            skCircle(sketch, "E44.15.1.1", {"center": v(381, 25.4) * mm, "radius": 2.38 * mm, "construction": true});
            skCircle(sketch, "E44.15.2.0", {"center": v(381, 50.8) * mm, "radius": 8.47 * mm, "construction": true});
            skCircle(sketch, "E44.15.2.1", {"center": v(381, 50.8) * mm, "radius": 2.38 * mm, "construction": true});
            skCircle(sketch, "E44.15.3.0", {"center": v(381, 76.2) * mm, "radius": 8.47 * mm, "construction": true});
            skCircle(sketch, "E44.15.3.1", {"center": v(381, 76.2) * mm, "radius": 2.38 * mm, "construction": true});
            skCircle(sketch, "E44.16.0.0", {"center": v(406.4, 0) * mm, "radius": 8.47 * mm, "construction": true});
            skCircle(sketch, "E44.16.0.1", {"center": v(406.4, 0) * mm, "radius": 2.38 * mm, "construction": true});
            skCircle(sketch, "E44.16.1.0", {"center": v(406.4, 25.4) * mm, "radius": 8.47 * mm, "construction": true});
            skCircle(sketch, "E44.16.1.1", {"center": v(406.4, 25.4) * mm, "radius": 2.38 * mm, "construction": true});
            skCircle(sketch, "E44.16.2.0", {"center": v(406.4, 50.8) * mm, "radius": 8.47 * mm, "construction": true});
            skCircle(sketch, "E44.16.2.1", {"center": v(406.4, 50.8) * mm, "radius": 2.38 * mm, "construction": true});
            skCircle(sketch, "E44.16.3.0", {"center": v(406.4, 76.2) * mm, "radius": 8.47 * mm, "construction": true});
            skCircle(sketch, "E44.16.3.1", {"center": v(406.4, 76.2) * mm, "radius": 2.38 * mm, "construction": true});
            skCircle(sketch, "E44.17.0.0", {"center": v(431.8, 0) * mm, "radius": 8.47 * mm, "construction": true});
            skCircle(sketch, "E44.17.0.1", {"center": v(431.8, 0) * mm, "radius": 2.38 * mm, "construction": true});
            skCircle(sketch, "E44.17.1.0", {"center": v(431.8, 25.4) * mm, "radius": 8.47 * mm, "construction": true});
            skCircle(sketch, "E44.17.1.1", {"center": v(431.8, 25.4) * mm, "radius": 2.38 * mm, "construction": true});
            skCircle(sketch, "E44.17.2.0", {"center": v(431.8, 50.8) * mm, "radius": 8.47 * mm, "construction": true});
            skCircle(sketch, "E44.17.2.1", {"center": v(431.8, 50.8) * mm, "radius": 2.38 * mm, "construction": true});
            skCircle(sketch, "E44.17.3.0", {"center": v(431.8, 76.2) * mm, "radius": 8.47 * mm, "construction": true});
            skCircle(sketch, "E44.17.3.1", {"center": v(431.8, 76.2) * mm, "radius": 2.38 * mm, "construction": true});
            skCircle(sketch, "E44.18.0.0", {"center": v(457.2, 0) * mm, "radius": 8.47 * mm, "construction": true});
            skCircle(sketch, "E44.18.0.1", {"center": v(457.2, 0) * mm, "radius": 2.38 * mm, "construction": true});
            skCircle(sketch, "E44.18.1.0", {"center": v(457.2, 25.4) * mm, "radius": 8.47 * mm, "construction": true});
            skCircle(sketch, "E44.18.1.1", {"center": v(457.2, 25.4) * mm, "radius": 2.38 * mm, "construction": true});
            skCircle(sketch, "E44.18.2.0", {"center": v(457.2, 50.8) * mm, "radius": 8.47 * mm, "construction": true});
            skCircle(sketch, "E44.18.2.1", {"center": v(457.2, 50.8) * mm, "radius": 2.38 * mm, "construction": true});
            skCircle(sketch, "E44.18.3.0", {"center": v(457.2, 76.2) * mm, "radius": 8.47 * mm, "construction": true});
            skCircle(sketch, "E44.18.3.1", {"center": v(457.2, 76.2) * mm, "radius": 2.38 * mm, "construction": true});
            skCircle(sketch, "E44.19.0.0", {"center": v(482.6, 0) * mm, "radius": 8.47 * mm, "construction": true});
            skCircle(sketch, "E44.19.0.1", {"center": v(482.6, 0) * mm, "radius": 2.38 * mm, "construction": true});
            skCircle(sketch, "E44.19.1.0", {"center": v(482.6, 25.4) * mm, "radius": 8.47 * mm, "construction": true});
            skCircle(sketch, "E44.19.1.1", {"center": v(482.6, 25.4) * mm, "radius": 2.38 * mm, "construction": true});
            skCircle(sketch, "E44.19.2.0", {"center": v(482.6, 50.8) * mm, "radius": 8.47 * mm, "construction": true});
            skCircle(sketch, "E44.19.2.1", {"center": v(482.6, 50.8) * mm, "radius": 2.38 * mm, "construction": true});
            skCircle(sketch, "E44.19.3.0", {"center": v(482.6, 76.2) * mm, "radius": 8.47 * mm, "construction": true});
            skCircle(sketch, "E44.19.3.1", {"center": v(482.6, 76.2) * mm, "radius": 2.38 * mm, "construction": true});
            skCircle(sketch, "E44.20.0.0", {"center": v(508, 0) * mm, "radius": 8.47 * mm, "construction": true});
            skCircle(sketch, "E44.20.0.1", {"center": v(508, 0) * mm, "radius": 2.38 * mm, "construction": true});
            skCircle(sketch, "E44.20.1.0", {"center": v(508, 25.4) * mm, "radius": 8.47 * mm, "construction": true});
            skCircle(sketch, "E44.20.1.1", {"center": v(508, 25.4) * mm, "radius": 2.38 * mm, "construction": true});
            skCircle(sketch, "E44.20.2.0", {"center": v(508, 50.8) * mm, "radius": 8.47 * mm, "construction": true});
            skCircle(sketch, "E44.20.2.1", {"center": v(508, 50.8) * mm, "radius": 2.38 * mm, "construction": true});
            skCircle(sketch, "E44.20.3.0", {"center": v(508, 76.2) * mm, "radius": 8.47 * mm, "construction": true});
            skCircle(sketch, "E44.20.3.1", {"center": v(508, 76.2) * mm, "radius": 2.38 * mm, "construction": true});
            skCircle(sketch, "E44.21.0.0", {"center": v(533.4, 0) * mm, "radius": 8.47 * mm, "construction": true});
            skCircle(sketch, "E44.21.0.1", {"center": v(533.4, 0) * mm, "radius": 2.38 * mm, "construction": true});
            skCircle(sketch, "E44.21.1.0", {"center": v(533.4, 25.4) * mm, "radius": 8.47 * mm, "construction": true});
            skCircle(sketch, "E44.21.1.1", {"center": v(533.4, 25.4) * mm, "radius": 2.38 * mm, "construction": true});
            skCircle(sketch, "E44.21.2.0", {"center": v(533.4, 50.8) * mm, "radius": 8.47 * mm, "construction": true});
            skCircle(sketch, "E44.21.2.1", {"center": v(533.4, 50.8) * mm, "radius": 2.38 * mm, "construction": true});
            skCircle(sketch, "E44.21.3.0", {"center": v(533.4, 76.2) * mm, "radius": 8.47 * mm, "construction": true});
            skCircle(sketch, "E44.21.3.1", {"center": v(533.4, 76.2) * mm, "radius": 2.38 * mm, "construction": true});
            skCircle(sketch, "E44.22.0.0", {"center": v(558.8, 0) * mm, "radius": 8.47 * mm, "construction": true});
            skCircle(sketch, "E44.22.0.1", {"center": v(558.8, 0) * mm, "radius": 2.38 * mm, "construction": true});
            skCircle(sketch, "E44.22.1.0", {"center": v(558.8, 25.4) * mm, "radius": 8.47 * mm, "construction": true});
            skCircle(sketch, "E44.22.1.1", {"center": v(558.8, 25.4) * mm, "radius": 2.38 * mm, "construction": true});
            skCircle(sketch, "E44.22.2.0", {"center": v(558.8, 50.8) * mm, "radius": 8.47 * mm, "construction": true});
            skCircle(sketch, "E44.22.2.1", {"center": v(558.8, 50.8) * mm, "radius": 2.38 * mm, "construction": true});
            skCircle(sketch, "E44.22.3.0", {"center": v(558.8, 76.2) * mm, "radius": 8.47 * mm, "construction": true});
            skCircle(sketch, "E44.22.3.1", {"center": v(558.8, 76.2) * mm, "radius": 2.38 * mm, "construction": true});
            skCircle(sketch, "E44.23.0.0", {"center": v(584.2, 0) * mm, "radius": 8.47 * mm, "construction": true});
            skCircle(sketch, "E44.23.0.1", {"center": v(584.2, 0) * mm, "radius": 2.38 * mm, "construction": true});
            skCircle(sketch, "E44.23.1.0", {"center": v(584.2, 25.4) * mm, "radius": 8.47 * mm, "construction": true});
            skCircle(sketch, "E44.23.1.1", {"center": v(584.2, 25.4) * mm, "radius": 2.38 * mm, "construction": true});
            skCircle(sketch, "E44.23.2.0", {"center": v(584.2, 50.8) * mm, "radius": 8.47 * mm, "construction": true});
            skCircle(sketch, "E44.23.2.1", {"center": v(584.2, 50.8) * mm, "radius": 2.38 * mm, "construction": true});
            skCircle(sketch, "E44.23.3.0", {"center": v(584.2, 76.2) * mm, "radius": 8.47 * mm, "construction": true});
            skCircle(sketch, "E44.23.3.1", {"center": v(584.2, 76.2) * mm, "radius": 2.38 * mm, "construction": true});
            skCircle(sketch, "E44.24.0.0", {"center": v(609.6, 0) * mm, "radius": 8.47 * mm, "construction": true});
            skCircle(sketch, "E44.24.0.1", {"center": v(609.6, 0) * mm, "radius": 2.38 * mm, "construction": true});
            skCircle(sketch, "E44.24.1.0", {"center": v(609.6, 25.4) * mm, "radius": 8.47 * mm, "construction": true});
            skCircle(sketch, "E44.24.1.1", {"center": v(609.6, 25.4) * mm, "radius": 2.38 * mm, "construction": true});
            skCircle(sketch, "E44.24.2.0", {"center": v(609.6, 50.8) * mm, "radius": 8.47 * mm, "construction": true});
            skCircle(sketch, "E44.24.2.1", {"center": v(609.6, 50.8) * mm, "radius": 2.38 * mm, "construction": true});
            skCircle(sketch, "E44.24.3.0", {"center": v(609.6, 76.2) * mm, "radius": 8.47 * mm, "construction": true});
            skCircle(sketch, "E44.24.3.1", {"center": v(609.6, 76.2) * mm, "radius": 2.38 * mm, "construction": true});
            skCircle(sketch, "E44.25.0.0", {"center": v(635, 0) * mm, "radius": 8.47 * mm, "construction": true});
            skCircle(sketch, "E44.25.0.1", {"center": v(635, 0) * mm, "radius": 2.38 * mm, "construction": true});
            skCircle(sketch, "E44.25.1.0", {"center": v(635, 25.4) * mm, "radius": 8.47 * mm, "construction": true});
            skCircle(sketch, "E44.25.1.1", {"center": v(635, 25.4) * mm, "radius": 2.38 * mm, "construction": true});
            skCircle(sketch, "E44.25.2.0", {"center": v(635, 50.8) * mm, "radius": 8.47 * mm, "construction": true});
            skCircle(sketch, "E44.25.2.1", {"center": v(635, 50.8) * mm, "radius": 2.38 * mm, "construction": true});
            skCircle(sketch, "E44.25.3.0", {"center": v(635, 76.2) * mm, "radius": 8.47 * mm, "construction": true});
            skCircle(sketch, "E44.25.3.1", {"center": v(635, 76.2) * mm, "radius": 2.38 * mm, "construction": true});
            skCircle(sketch, "E44.26.0.0", {"center": v(660.4, 0) * mm, "radius": 8.47 * mm, "construction": true});
            skCircle(sketch, "E44.26.0.1", {"center": v(660.4, 0) * mm, "radius": 2.38 * mm, "construction": true});
            skCircle(sketch, "E44.26.1.0", {"center": v(660.4, 25.4) * mm, "radius": 8.47 * mm, "construction": true});
            skCircle(sketch, "E44.26.1.1", {"center": v(660.4, 25.4) * mm, "radius": 2.38 * mm, "construction": true});
            skCircle(sketch, "E44.26.2.0", {"center": v(660.4, 50.8) * mm, "radius": 8.47 * mm, "construction": true});
            skCircle(sketch, "E44.26.2.1", {"center": v(660.4, 50.8) * mm, "radius": 2.38 * mm, "construction": true});
            skCircle(sketch, "E44.26.3.0", {"center": v(660.4, 76.2) * mm, "radius": 8.47 * mm, "construction": true});
            skCircle(sketch, "E44.26.3.1", {"center": v(660.4, 76.2) * mm, "radius": 2.38 * mm, "construction": true});
            skCircle(sketch, "E44.27.0.0", {"center": v(685.8, 0) * mm, "radius": 8.47 * mm, "construction": true});
            skCircle(sketch, "E44.27.0.1", {"center": v(685.8, 0) * mm, "radius": 2.38 * mm, "construction": true});
            skCircle(sketch, "E44.27.1.0", {"center": v(685.8, 25.4) * mm, "radius": 8.47 * mm, "construction": true});
            skCircle(sketch, "E44.27.1.1", {"center": v(685.8, 25.4) * mm, "radius": 2.38 * mm, "construction": true});
            skCircle(sketch, "E44.27.2.0", {"center": v(685.8, 50.8) * mm, "radius": 8.47 * mm, "construction": true});
            skCircle(sketch, "E44.27.2.1", {"center": v(685.8, 50.8) * mm, "radius": 2.38 * mm, "construction": true});
            skCircle(sketch, "E44.27.3.0", {"center": v(685.8, 76.2) * mm, "radius": 8.47 * mm, "construction": true});
            skCircle(sketch, "E44.27.3.1", {"center": v(685.8, 76.2) * mm, "radius": 2.38 * mm, "construction": true});
            skLineSegment(sketch, "E44.direction1", {"start": v(0, 0) * mm, "end": v(25.4, 0) * mm, "construction": true});
            skLineSegment(sketch, "E44.direction2", {"start": v(0, 0) * mm, "end": v(0, 25.4) * mm, "construction": true});
            skLineSegment(sketch, "E45.bottom", {"start": v(50.8, 84.67) * mm, "end": v(127, 84.67) * mm});
            skLineSegment(sketch, "E45.top", {"start": v(50.8, -8.47) * mm, "end": v(127, -8.47) * mm});
            skLineSegment(sketch, "E45.left", {"start": v(42.33, 76.2) * mm, "end": v(42.33, 0) * mm});
            skLineSegment(sketch, "E45.right", {"start": v(135.47, 76.2) * mm, "end": v(135.47, 0) * mm});
            skPoint(sketch, "E46.visualSharp", {"position": v(42.33, -8.47) * mm});
            skArc(sketch, "E46.filletArc", {"start": v(42.33, 0) * mm, "mid": v(44.81, -5.99) * mm, "end": v(50.8, -8.47) * mm});
            skPoint(sketch, "E47.visualSharp", {"position": v(42.33, 84.67) * mm});
            skArc(sketch, "E47.filletArc", {"start": v(50.8, 84.67) * mm, "mid": v(44.81, 82.19) * mm, "end": v(42.33, 76.2) * mm});
            skPoint(sketch, "E48.visualSharp", {"position": v(135.47, 84.67) * mm});
            skArc(sketch, "E48.filletArc", {"start": v(135.47, 76.2) * mm, "mid": v(132.99, 82.19) * mm, "end": v(127, 84.67) * mm});
            skPoint(sketch, "E49.visualSharp", {"position": v(135.47, -8.47) * mm});
            skArc(sketch, "E49.filletArc", {"start": v(127, -8.47) * mm, "mid": v(132.99, -5.99) * mm, "end": v(135.47, 0) * mm});
            skSolve(sketch);
        }
        {
            var Q0;
            Q0=makeQuery(id+"F7.imprint","IMPRINT",FACE,{"disambiguationData":[TD([[makeQuery(id+"F7.imprint","IMPRINT",EDGE,{"derivedFrom":sQuery(id+"F7.wireOp",EDGE,"E33")}),-1.0]])]});
            var Q1;
            Q1=sQuery(id+"F2.wireOp",VERTEX,"E11.left.end");
            extrude(context, id + "F8", {"entities" : qUnion([Q0]), "endBound" : BoundingType.UP_TO_VERTEX, "oppositeDirection" : true, "endBoundEntityVertex" : qUnion([Q1]), "depth" : 25.4 * mm});
        }
        {
            var Q0;
            Q0=qCreatedBy(makeId("Top.planeOp"),FACE);
            var sketch = newSketch(context, id + "F9", { "sketchPlane" : qUnion([Q0])});
            skCircle(sketch, "E50.0", {"center": v(63.5, 38.1) * mm, "radius": 4.76 * mm});
            skCircle(sketch, "E51", {"center": v(622.3, 38.1) * mm, "radius": 4.76 * mm, "construction": true});
            skLineSegment(sketch, "E52", {"start": v(609.6, 42.86) * mm, "end": v(625.48, 42.86) * mm});
            skLineSegment(sketch, "E53", {"start": v(625.48, 33.34) * mm, "end": v(609.6, 33.34) * mm});
            skArc(sketch, "E54", {"start": v(609.6, 42.86) * mm, "mid": v(604.84, 38.1) * mm, "end": v(609.6, 33.34) * mm});
            skArc(sketch, "E55", {"start": v(625.48, 33.34) * mm, "mid": v(630.24, 38.1) * mm, "end": v(625.48, 42.86) * mm});
            skCircle(sketch, "E56.0", {"center": v(0, 0) * mm, "radius": 2.38 * mm});
            skCircle(sketch, "E56.1", {"center": v(0, 0) * mm, "radius": 8.47 * mm, "construction": true});
            skCircle(sketch, "E57.0.1.0", {"center": v(0, 25.4) * mm, "radius": 2.38 * mm});
            skCircle(sketch, "E57.0.1.1", {"center": v(0, 25.4) * mm, "radius": 8.47 * mm, "construction": true});
            skCircle(sketch, "E57.0.2.0", {"center": v(0, 50.8) * mm, "radius": 2.38 * mm});
            skCircle(sketch, "E57.0.2.1", {"center": v(0, 50.8) * mm, "radius": 8.47 * mm, "construction": true});
            skCircle(sketch, "E57.0.3.0", {"center": v(0, 76.2) * mm, "radius": 2.38 * mm});
            skCircle(sketch, "E57.0.3.1", {"center": v(0, 76.2) * mm, "radius": 8.47 * mm, "construction": true});
            skCircle(sketch, "E57.1.0.0", {"center": v(25.4, 0) * mm, "radius": 2.38 * mm});
            skCircle(sketch, "E57.1.0.1", {"center": v(25.4, 0) * mm, "radius": 8.47 * mm, "construction": true});
            skCircle(sketch, "E57.1.1.0", {"center": v(25.4, 25.4) * mm, "radius": 2.38 * mm});
            skCircle(sketch, "E57.1.1.1", {"center": v(25.4, 25.4) * mm, "radius": 8.47 * mm, "construction": true});
            skCircle(sketch, "E57.1.2.0", {"center": v(25.4, 50.8) * mm, "radius": 2.38 * mm});
            skCircle(sketch, "E57.1.2.1", {"center": v(25.4, 50.8) * mm, "radius": 8.47 * mm, "construction": true});
            skCircle(sketch, "E57.1.3.0", {"center": v(25.4, 76.2) * mm, "radius": 2.38 * mm});
            skCircle(sketch, "E57.1.3.1", {"center": v(25.4, 76.2) * mm, "radius": 8.47 * mm, "construction": true});
            skCircle(sketch, "E57.2.0.0", {"center": v(50.8, 0) * mm, "radius": 2.38 * mm});
            skCircle(sketch, "E57.2.0.1", {"center": v(50.8, 0) * mm, "radius": 8.47 * mm, "construction": true});
            skCircle(sketch, "E57.2.1.0", {"center": v(50.8, 25.4) * mm, "radius": 2.38 * mm});
            skCircle(sketch, "E57.2.1.1", {"center": v(50.8, 25.4) * mm, "radius": 8.47 * mm, "construction": true});
            skCircle(sketch, "E57.2.2.0", {"center": v(50.8, 50.8) * mm, "radius": 2.38 * mm});
            skCircle(sketch, "E57.2.2.1", {"center": v(50.8, 50.8) * mm, "radius": 8.47 * mm, "construction": true});
            skCircle(sketch, "E57.2.3.0", {"center": v(50.8, 76.2) * mm, "radius": 2.38 * mm});
            skCircle(sketch, "E57.2.3.1", {"center": v(50.8, 76.2) * mm, "radius": 8.47 * mm, "construction": true});
            skCircle(sketch, "E57.3.0.0", {"center": v(76.2, 0) * mm, "radius": 2.38 * mm});
            skCircle(sketch, "E57.3.0.1", {"center": v(76.2, 0) * mm, "radius": 8.47 * mm, "construction": true});
            skCircle(sketch, "E57.3.1.0", {"center": v(76.2, 25.4) * mm, "radius": 2.38 * mm});
            skCircle(sketch, "E57.3.1.1", {"center": v(76.2, 25.4) * mm, "radius": 8.47 * mm, "construction": true});
            skCircle(sketch, "E57.3.2.0", {"center": v(76.2, 50.8) * mm, "radius": 2.38 * mm});
            skCircle(sketch, "E57.3.2.1", {"center": v(76.2, 50.8) * mm, "radius": 8.47 * mm, "construction": true});
            skCircle(sketch, "E57.3.3.0", {"center": v(76.2, 76.2) * mm, "radius": 2.38 * mm});
            skCircle(sketch, "E57.3.3.1", {"center": v(76.2, 76.2) * mm, "radius": 8.47 * mm, "construction": true});
            skCircle(sketch, "E57.4.0.0", {"center": v(101.6, 0) * mm, "radius": 2.38 * mm});
            skCircle(sketch, "E57.4.0.1", {"center": v(101.6, 0) * mm, "radius": 8.47 * mm, "construction": true});
            skCircle(sketch, "E57.4.1.0", {"center": v(101.6, 25.4) * mm, "radius": 2.38 * mm});
            skCircle(sketch, "E57.4.1.1", {"center": v(101.6, 25.4) * mm, "radius": 8.47 * mm, "construction": true});
            skCircle(sketch, "E57.4.2.0", {"center": v(101.6, 50.8) * mm, "radius": 2.38 * mm});
            skCircle(sketch, "E57.4.2.1", {"center": v(101.6, 50.8) * mm, "radius": 8.47 * mm, "construction": true});
            skCircle(sketch, "E57.4.3.0", {"center": v(101.6, 76.2) * mm, "radius": 2.38 * mm});
            skCircle(sketch, "E57.4.3.1", {"center": v(101.6, 76.2) * mm, "radius": 8.47 * mm, "construction": true});
            skCircle(sketch, "E57.5.0.0", {"center": v(127, 0) * mm, "radius": 2.38 * mm, "construction": true});
            skCircle(sketch, "E57.5.0.1", {"center": v(127, 0) * mm, "radius": 8.47 * mm, "construction": true});
            skCircle(sketch, "E57.5.1.0", {"center": v(127, 25.4) * mm, "radius": 2.38 * mm, "construction": true});
            skCircle(sketch, "E57.5.1.1", {"center": v(127, 25.4) * mm, "radius": 8.47 * mm, "construction": true});
            skCircle(sketch, "E57.5.2.0", {"center": v(127, 50.8) * mm, "radius": 2.38 * mm, "construction": true});
            skCircle(sketch, "E57.5.2.1", {"center": v(127, 50.8) * mm, "radius": 8.47 * mm, "construction": true});
            skCircle(sketch, "E57.5.3.0", {"center": v(127, 76.2) * mm, "radius": 2.38 * mm, "construction": true});
            skCircle(sketch, "E57.5.3.1", {"center": v(127, 76.2) * mm, "radius": 8.47 * mm, "construction": true});
            skCircle(sketch, "E57.6.0.0", {"center": v(152.4, 0) * mm, "radius": 2.38 * mm, "construction": true});
            skCircle(sketch, "E57.6.0.1", {"center": v(152.4, 0) * mm, "radius": 8.47 * mm, "construction": true});
            skCircle(sketch, "E57.6.1.0", {"center": v(152.4, 25.4) * mm, "radius": 2.38 * mm, "construction": true});
            skCircle(sketch, "E57.6.1.1", {"center": v(152.4, 25.4) * mm, "radius": 8.47 * mm, "construction": true});
            skCircle(sketch, "E57.6.2.0", {"center": v(152.4, 50.8) * mm, "radius": 2.38 * mm, "construction": true});
            skCircle(sketch, "E57.6.2.1", {"center": v(152.4, 50.8) * mm, "radius": 8.47 * mm, "construction": true});
            skCircle(sketch, "E57.6.3.0", {"center": v(152.4, 76.2) * mm, "radius": 2.38 * mm, "construction": true});
            skCircle(sketch, "E57.6.3.1", {"center": v(152.4, 76.2) * mm, "radius": 8.47 * mm, "construction": true});
            skCircle(sketch, "E57.7.0.0", {"center": v(177.8, 0) * mm, "radius": 2.38 * mm, "construction": true});
            skCircle(sketch, "E57.7.0.1", {"center": v(177.8, 0) * mm, "radius": 8.47 * mm, "construction": true});
            skCircle(sketch, "E57.7.1.0", {"center": v(177.8, 25.4) * mm, "radius": 2.38 * mm, "construction": true});
            skCircle(sketch, "E57.7.1.1", {"center": v(177.8, 25.4) * mm, "radius": 8.47 * mm, "construction": true});
            skCircle(sketch, "E57.7.2.0", {"center": v(177.8, 50.8) * mm, "radius": 2.38 * mm, "construction": true});
            skCircle(sketch, "E57.7.2.1", {"center": v(177.8, 50.8) * mm, "radius": 8.47 * mm, "construction": true});
            skCircle(sketch, "E57.7.3.0", {"center": v(177.8, 76.2) * mm, "radius": 2.38 * mm, "construction": true});
            skCircle(sketch, "E57.7.3.1", {"center": v(177.8, 76.2) * mm, "radius": 8.47 * mm, "construction": true});
            skCircle(sketch, "E57.8.0.0", {"center": v(203.2, 0) * mm, "radius": 2.38 * mm, "construction": true});
            skCircle(sketch, "E57.8.0.1", {"center": v(203.2, 0) * mm, "radius": 8.47 * mm, "construction": true});
            skCircle(sketch, "E57.8.1.0", {"center": v(203.2, 25.4) * mm, "radius": 2.38 * mm, "construction": true});
            skCircle(sketch, "E57.8.1.1", {"center": v(203.2, 25.4) * mm, "radius": 8.47 * mm, "construction": true});
            skCircle(sketch, "E57.8.2.0", {"center": v(203.2, 50.8) * mm, "radius": 2.38 * mm, "construction": true});
            skCircle(sketch, "E57.8.2.1", {"center": v(203.2, 50.8) * mm, "radius": 8.47 * mm, "construction": true});
            skCircle(sketch, "E57.8.3.0", {"center": v(203.2, 76.2) * mm, "radius": 2.38 * mm, "construction": true});
            skCircle(sketch, "E57.8.3.1", {"center": v(203.2, 76.2) * mm, "radius": 8.47 * mm, "construction": true});
            skCircle(sketch, "E57.9.0.0", {"center": v(228.6, 0) * mm, "radius": 2.38 * mm, "construction": true});
            skCircle(sketch, "E57.9.0.1", {"center": v(228.6, 0) * mm, "radius": 8.47 * mm, "construction": true});
            skCircle(sketch, "E57.9.1.0", {"center": v(228.6, 25.4) * mm, "radius": 2.38 * mm, "construction": true});
            skCircle(sketch, "E57.9.1.1", {"center": v(228.6, 25.4) * mm, "radius": 8.47 * mm, "construction": true});
            skCircle(sketch, "E57.9.2.0", {"center": v(228.6, 50.8) * mm, "radius": 2.38 * mm, "construction": true});
            skCircle(sketch, "E57.9.2.1", {"center": v(228.6, 50.8) * mm, "radius": 8.47 * mm, "construction": true});
            skCircle(sketch, "E57.9.3.0", {"center": v(228.6, 76.2) * mm, "radius": 2.38 * mm, "construction": true});
            skCircle(sketch, "E57.9.3.1", {"center": v(228.6, 76.2) * mm, "radius": 8.47 * mm, "construction": true});
            skCircle(sketch, "E57.10.0.0", {"center": v(254, 0) * mm, "radius": 2.38 * mm, "construction": true});
            skCircle(sketch, "E57.10.0.1", {"center": v(254, 0) * mm, "radius": 8.47 * mm, "construction": true});
            skCircle(sketch, "E57.10.1.0", {"center": v(254, 25.4) * mm, "radius": 2.38 * mm, "construction": true});
            skCircle(sketch, "E57.10.1.1", {"center": v(254, 25.4) * mm, "radius": 8.47 * mm, "construction": true});
            skCircle(sketch, "E57.10.2.0", {"center": v(254, 50.8) * mm, "radius": 2.38 * mm, "construction": true});
            skCircle(sketch, "E57.10.2.1", {"center": v(254, 50.8) * mm, "radius": 8.47 * mm, "construction": true});
            skCircle(sketch, "E57.10.3.0", {"center": v(254, 76.2) * mm, "radius": 2.38 * mm, "construction": true});
            skCircle(sketch, "E57.10.3.1", {"center": v(254, 76.2) * mm, "radius": 8.47 * mm, "construction": true});
            skCircle(sketch, "E57.11.0.0", {"center": v(279.4, 0) * mm, "radius": 2.38 * mm, "construction": true});
            skCircle(sketch, "E57.11.0.1", {"center": v(279.4, 0) * mm, "radius": 8.47 * mm, "construction": true});
            skCircle(sketch, "E57.11.1.0", {"center": v(279.4, 25.4) * mm, "radius": 2.38 * mm, "construction": true});
            skCircle(sketch, "E57.11.1.1", {"center": v(279.4, 25.4) * mm, "radius": 8.47 * mm, "construction": true});
            skCircle(sketch, "E57.11.2.0", {"center": v(279.4, 50.8) * mm, "radius": 2.38 * mm, "construction": true});
            skCircle(sketch, "E57.11.2.1", {"center": v(279.4, 50.8) * mm, "radius": 8.47 * mm, "construction": true});
            skCircle(sketch, "E57.11.3.0", {"center": v(279.4, 76.2) * mm, "radius": 2.38 * mm, "construction": true});
            skCircle(sketch, "E57.11.3.1", {"center": v(279.4, 76.2) * mm, "radius": 8.47 * mm, "construction": true});
            skCircle(sketch, "E57.12.0.0", {"center": v(304.8, 0) * mm, "radius": 2.38 * mm, "construction": true});
            skCircle(sketch, "E57.12.0.1", {"center": v(304.8, 0) * mm, "radius": 8.47 * mm, "construction": true});
            skCircle(sketch, "E57.12.1.0", {"center": v(304.8, 25.4) * mm, "radius": 2.38 * mm, "construction": true});
            skCircle(sketch, "E57.12.1.1", {"center": v(304.8, 25.4) * mm, "radius": 8.47 * mm, "construction": true});
            skCircle(sketch, "E57.12.2.0", {"center": v(304.8, 50.8) * mm, "radius": 2.38 * mm, "construction": true});
            skCircle(sketch, "E57.12.2.1", {"center": v(304.8, 50.8) * mm, "radius": 8.47 * mm, "construction": true});
            skCircle(sketch, "E57.12.3.0", {"center": v(304.8, 76.2) * mm, "radius": 2.38 * mm, "construction": true});
            skCircle(sketch, "E57.12.3.1", {"center": v(304.8, 76.2) * mm, "radius": 8.47 * mm, "construction": true});
            skCircle(sketch, "E57.13.0.0", {"center": v(330.2, 0) * mm, "radius": 2.38 * mm, "construction": true});
            skCircle(sketch, "E57.13.0.1", {"center": v(330.2, 0) * mm, "radius": 8.47 * mm, "construction": true});
            skCircle(sketch, "E57.13.1.0", {"center": v(330.2, 25.4) * mm, "radius": 2.38 * mm, "construction": true});
            skCircle(sketch, "E57.13.1.1", {"center": v(330.2, 25.4) * mm, "radius": 8.47 * mm, "construction": true});
            skCircle(sketch, "E57.13.2.0", {"center": v(330.2, 50.8) * mm, "radius": 2.38 * mm, "construction": true});
            skCircle(sketch, "E57.13.2.1", {"center": v(330.2, 50.8) * mm, "radius": 8.47 * mm, "construction": true});
            skCircle(sketch, "E57.13.3.0", {"center": v(330.2, 76.2) * mm, "radius": 2.38 * mm, "construction": true});
            skCircle(sketch, "E57.13.3.1", {"center": v(330.2, 76.2) * mm, "radius": 8.47 * mm, "construction": true});
            skCircle(sketch, "E57.14.0.0", {"center": v(355.6, 0) * mm, "radius": 2.38 * mm, "construction": true});
            skCircle(sketch, "E57.14.0.1", {"center": v(355.6, 0) * mm, "radius": 8.47 * mm, "construction": true});
            skCircle(sketch, "E57.14.1.0", {"center": v(355.6, 25.4) * mm, "radius": 2.38 * mm, "construction": true});
            skCircle(sketch, "E57.14.1.1", {"center": v(355.6, 25.4) * mm, "radius": 8.47 * mm, "construction": true});
            skCircle(sketch, "E57.14.2.0", {"center": v(355.6, 50.8) * mm, "radius": 2.38 * mm, "construction": true});
            skCircle(sketch, "E57.14.2.1", {"center": v(355.6, 50.8) * mm, "radius": 8.47 * mm, "construction": true});
            skCircle(sketch, "E57.14.3.0", {"center": v(355.6, 76.2) * mm, "radius": 2.38 * mm, "construction": true});
            skCircle(sketch, "E57.14.3.1", {"center": v(355.6, 76.2) * mm, "radius": 8.47 * mm, "construction": true});
            skCircle(sketch, "E57.15.0.0", {"center": v(381, 0) * mm, "radius": 2.38 * mm, "construction": true});
            skCircle(sketch, "E57.15.0.1", {"center": v(381, 0) * mm, "radius": 8.47 * mm, "construction": true});
            skCircle(sketch, "E57.15.1.0", {"center": v(381, 25.4) * mm, "radius": 2.38 * mm, "construction": true});
            skCircle(sketch, "E57.15.1.1", {"center": v(381, 25.4) * mm, "radius": 8.47 * mm, "construction": true});
            skCircle(sketch, "E57.15.2.0", {"center": v(381, 50.8) * mm, "radius": 2.38 * mm, "construction": true});
            skCircle(sketch, "E57.15.2.1", {"center": v(381, 50.8) * mm, "radius": 8.47 * mm, "construction": true});
            skCircle(sketch, "E57.15.3.0", {"center": v(381, 76.2) * mm, "radius": 2.38 * mm, "construction": true});
            skCircle(sketch, "E57.15.3.1", {"center": v(381, 76.2) * mm, "radius": 8.47 * mm, "construction": true});
            skCircle(sketch, "E57.16.0.0", {"center": v(406.4, 0) * mm, "radius": 2.38 * mm, "construction": true});
            skCircle(sketch, "E57.16.0.1", {"center": v(406.4, 0) * mm, "radius": 8.47 * mm, "construction": true});
            skCircle(sketch, "E57.16.1.0", {"center": v(406.4, 25.4) * mm, "radius": 2.38 * mm, "construction": true});
            skCircle(sketch, "E57.16.1.1", {"center": v(406.4, 25.4) * mm, "radius": 8.47 * mm, "construction": true});
            skCircle(sketch, "E57.16.2.0", {"center": v(406.4, 50.8) * mm, "radius": 2.38 * mm, "construction": true});
            skCircle(sketch, "E57.16.2.1", {"center": v(406.4, 50.8) * mm, "radius": 8.47 * mm, "construction": true});
            skCircle(sketch, "E57.16.3.0", {"center": v(406.4, 76.2) * mm, "radius": 2.38 * mm, "construction": true});
            skCircle(sketch, "E57.16.3.1", {"center": v(406.4, 76.2) * mm, "radius": 8.47 * mm, "construction": true});
            skCircle(sketch, "E57.17.0.0", {"center": v(431.8, 0) * mm, "radius": 2.38 * mm, "construction": true});
            skCircle(sketch, "E57.17.0.1", {"center": v(431.8, 0) * mm, "radius": 8.47 * mm, "construction": true});
            skCircle(sketch, "E57.17.1.0", {"center": v(431.8, 25.4) * mm, "radius": 2.38 * mm, "construction": true});
            skCircle(sketch, "E57.17.1.1", {"center": v(431.8, 25.4) * mm, "radius": 8.47 * mm, "construction": true});
            skCircle(sketch, "E57.17.2.0", {"center": v(431.8, 50.8) * mm, "radius": 2.38 * mm, "construction": true});
            skCircle(sketch, "E57.17.2.1", {"center": v(431.8, 50.8) * mm, "radius": 8.47 * mm, "construction": true});
            skCircle(sketch, "E57.17.3.0", {"center": v(431.8, 76.2) * mm, "radius": 2.38 * mm, "construction": true});
            skCircle(sketch, "E57.17.3.1", {"center": v(431.8, 76.2) * mm, "radius": 8.47 * mm, "construction": true});
            skCircle(sketch, "E57.18.0.0", {"center": v(457.2, 0) * mm, "radius": 2.38 * mm, "construction": true});
            skCircle(sketch, "E57.18.0.1", {"center": v(457.2, 0) * mm, "radius": 8.47 * mm, "construction": true});
            skCircle(sketch, "E57.18.1.0", {"center": v(457.2, 25.4) * mm, "radius": 2.38 * mm, "construction": true});
            skCircle(sketch, "E57.18.1.1", {"center": v(457.2, 25.4) * mm, "radius": 8.47 * mm, "construction": true});
            skCircle(sketch, "E57.18.2.0", {"center": v(457.2, 50.8) * mm, "radius": 2.38 * mm, "construction": true});
            skCircle(sketch, "E57.18.2.1", {"center": v(457.2, 50.8) * mm, "radius": 8.47 * mm, "construction": true});
            skCircle(sketch, "E57.18.3.0", {"center": v(457.2, 76.2) * mm, "radius": 2.38 * mm, "construction": true});
            skCircle(sketch, "E57.18.3.1", {"center": v(457.2, 76.2) * mm, "radius": 8.47 * mm, "construction": true});
            skCircle(sketch, "E57.19.0.0", {"center": v(482.6, 0) * mm, "radius": 2.38 * mm, "construction": true});
            skCircle(sketch, "E57.19.0.1", {"center": v(482.6, 0) * mm, "radius": 8.47 * mm, "construction": true});
            skCircle(sketch, "E57.19.1.0", {"center": v(482.6, 25.4) * mm, "radius": 2.38 * mm, "construction": true});
            skCircle(sketch, "E57.19.1.1", {"center": v(482.6, 25.4) * mm, "radius": 8.47 * mm, "construction": true});
            skCircle(sketch, "E57.19.2.0", {"center": v(482.6, 50.8) * mm, "radius": 2.38 * mm, "construction": true});
            skCircle(sketch, "E57.19.2.1", {"center": v(482.6, 50.8) * mm, "radius": 8.47 * mm, "construction": true});
            skCircle(sketch, "E57.19.3.0", {"center": v(482.6, 76.2) * mm, "radius": 2.38 * mm, "construction": true});
            skCircle(sketch, "E57.19.3.1", {"center": v(482.6, 76.2) * mm, "radius": 8.47 * mm, "construction": true});
            skCircle(sketch, "E57.20.0.0", {"center": v(508, 0) * mm, "radius": 2.38 * mm, "construction": true});
            skCircle(sketch, "E57.20.0.1", {"center": v(508, 0) * mm, "radius": 8.47 * mm, "construction": true});
            skCircle(sketch, "E57.20.1.0", {"center": v(508, 25.4) * mm, "radius": 2.38 * mm, "construction": true});
            skCircle(sketch, "E57.20.1.1", {"center": v(508, 25.4) * mm, "radius": 8.47 * mm, "construction": true});
            skCircle(sketch, "E57.20.2.0", {"center": v(508, 50.8) * mm, "radius": 2.38 * mm, "construction": true});
            skCircle(sketch, "E57.20.2.1", {"center": v(508, 50.8) * mm, "radius": 8.47 * mm, "construction": true});
            skCircle(sketch, "E57.20.3.0", {"center": v(508, 76.2) * mm, "radius": 2.38 * mm, "construction": true});
            skCircle(sketch, "E57.20.3.1", {"center": v(508, 76.2) * mm, "radius": 8.47 * mm, "construction": true});
            skCircle(sketch, "E57.21.0.0", {"center": v(533.4, 0) * mm, "radius": 2.38 * mm, "construction": true});
            skCircle(sketch, "E57.21.0.1", {"center": v(533.4, 0) * mm, "radius": 8.47 * mm, "construction": true});
            skCircle(sketch, "E57.21.1.0", {"center": v(533.4, 25.4) * mm, "radius": 2.38 * mm, "construction": true});
            skCircle(sketch, "E57.21.1.1", {"center": v(533.4, 25.4) * mm, "radius": 8.47 * mm, "construction": true});
            skCircle(sketch, "E57.21.2.0", {"center": v(533.4, 50.8) * mm, "radius": 2.38 * mm, "construction": true});
            skCircle(sketch, "E57.21.2.1", {"center": v(533.4, 50.8) * mm, "radius": 8.47 * mm, "construction": true});
            skCircle(sketch, "E57.21.3.0", {"center": v(533.4, 76.2) * mm, "radius": 2.38 * mm, "construction": true});
            skCircle(sketch, "E57.21.3.1", {"center": v(533.4, 76.2) * mm, "radius": 8.47 * mm, "construction": true});
            skCircle(sketch, "E57.22.0.0", {"center": v(558.8, 0) * mm, "radius": 2.38 * mm, "construction": true});
            skCircle(sketch, "E57.22.0.1", {"center": v(558.8, 0) * mm, "radius": 8.47 * mm, "construction": true});
            skCircle(sketch, "E57.22.1.0", {"center": v(558.8, 25.4) * mm, "radius": 2.38 * mm, "construction": true});
            skCircle(sketch, "E57.22.1.1", {"center": v(558.8, 25.4) * mm, "radius": 8.47 * mm, "construction": true});
            skCircle(sketch, "E57.22.2.0", {"center": v(558.8, 50.8) * mm, "radius": 2.38 * mm, "construction": true});
            skCircle(sketch, "E57.22.2.1", {"center": v(558.8, 50.8) * mm, "radius": 8.47 * mm, "construction": true});
            skCircle(sketch, "E57.22.3.0", {"center": v(558.8, 76.2) * mm, "radius": 2.38 * mm, "construction": true});
            skCircle(sketch, "E57.22.3.1", {"center": v(558.8, 76.2) * mm, "radius": 8.47 * mm, "construction": true});
            skCircle(sketch, "E57.23.0.0", {"center": v(584.2, 0) * mm, "radius": 2.38 * mm});
            skCircle(sketch, "E57.23.0.1", {"center": v(584.2, 0) * mm, "radius": 8.47 * mm, "construction": true});
            skCircle(sketch, "E57.23.1.0", {"center": v(584.2, 25.4) * mm, "radius": 2.38 * mm});
            skCircle(sketch, "E57.23.1.1", {"center": v(584.2, 25.4) * mm, "radius": 8.47 * mm, "construction": true});
            skCircle(sketch, "E57.23.2.0", {"center": v(584.2, 50.8) * mm, "radius": 2.38 * mm});
            skCircle(sketch, "E57.23.2.1", {"center": v(584.2, 50.8) * mm, "radius": 8.47 * mm, "construction": true});
            skCircle(sketch, "E57.23.3.0", {"center": v(584.2, 76.2) * mm, "radius": 2.38 * mm});
            skCircle(sketch, "E57.23.3.1", {"center": v(584.2, 76.2) * mm, "radius": 8.47 * mm, "construction": true});
            skCircle(sketch, "E57.24.0.0", {"center": v(609.6, 0) * mm, "radius": 2.38 * mm});
            skCircle(sketch, "E57.24.0.1", {"center": v(609.6, 0) * mm, "radius": 8.47 * mm, "construction": true});
            skCircle(sketch, "E57.24.1.0", {"center": v(609.6, 25.4) * mm, "radius": 2.38 * mm, "construction": true});
            skCircle(sketch, "E57.24.1.1", {"center": v(609.6, 25.4) * mm, "radius": 8.47 * mm, "construction": true});
            skCircle(sketch, "E57.24.2.0", {"center": v(609.6, 50.8) * mm, "radius": 2.38 * mm, "construction": true});
            skCircle(sketch, "E57.24.2.1", {"center": v(609.6, 50.8) * mm, "radius": 8.47 * mm, "construction": true});
            skCircle(sketch, "E57.24.3.0", {"center": v(609.6, 76.2) * mm, "radius": 2.38 * mm});
            skCircle(sketch, "E57.24.3.1", {"center": v(609.6, 76.2) * mm, "radius": 8.47 * mm, "construction": true});
            skCircle(sketch, "E57.25.0.0", {"center": v(635, 0) * mm, "radius": 2.38 * mm});
            skCircle(sketch, "E57.25.0.1", {"center": v(635, 0) * mm, "radius": 8.47 * mm, "construction": true});
            skCircle(sketch, "E57.25.1.0", {"center": v(635, 25.4) * mm, "radius": 2.38 * mm});
            skCircle(sketch, "E57.25.1.1", {"center": v(635, 25.4) * mm, "radius": 8.47 * mm, "construction": true});
            skCircle(sketch, "E57.25.2.0", {"center": v(635, 50.8) * mm, "radius": 2.38 * mm});
            skCircle(sketch, "E57.25.2.1", {"center": v(635, 50.8) * mm, "radius": 8.47 * mm, "construction": true});
            skCircle(sketch, "E57.25.3.0", {"center": v(635, 76.2) * mm, "radius": 2.38 * mm});
            skCircle(sketch, "E57.25.3.1", {"center": v(635, 76.2) * mm, "radius": 8.47 * mm, "construction": true});
            skCircle(sketch, "E57.26.0.0", {"center": v(660.4, 0) * mm, "radius": 2.38 * mm});
            skCircle(sketch, "E57.26.0.1", {"center": v(660.4, 0) * mm, "radius": 8.47 * mm, "construction": true});
            skCircle(sketch, "E57.26.1.0", {"center": v(660.4, 25.4) * mm, "radius": 2.38 * mm});
            skCircle(sketch, "E57.26.1.1", {"center": v(660.4, 25.4) * mm, "radius": 8.47 * mm, "construction": true});
            skCircle(sketch, "E57.26.2.0", {"center": v(660.4, 50.8) * mm, "radius": 2.38 * mm});
            skCircle(sketch, "E57.26.2.1", {"center": v(660.4, 50.8) * mm, "radius": 8.47 * mm, "construction": true});
            skCircle(sketch, "E57.26.3.0", {"center": v(660.4, 76.2) * mm, "radius": 2.38 * mm});
            skCircle(sketch, "E57.26.3.1", {"center": v(660.4, 76.2) * mm, "radius": 8.47 * mm, "construction": true});
            skCircle(sketch, "E57.27.0.0", {"center": v(685.8, 0) * mm, "radius": 2.38 * mm});
            skCircle(sketch, "E57.27.0.1", {"center": v(685.8, 0) * mm, "radius": 8.47 * mm, "construction": true});
            skCircle(sketch, "E57.27.1.0", {"center": v(685.8, 25.4) * mm, "radius": 2.38 * mm});
            skCircle(sketch, "E57.27.1.1", {"center": v(685.8, 25.4) * mm, "radius": 8.47 * mm, "construction": true});
            skCircle(sketch, "E57.27.2.0", {"center": v(685.8, 50.8) * mm, "radius": 2.38 * mm});
            skCircle(sketch, "E57.27.2.1", {"center": v(685.8, 50.8) * mm, "radius": 8.47 * mm, "construction": true});
            skCircle(sketch, "E57.27.3.0", {"center": v(685.8, 76.2) * mm, "radius": 2.38 * mm});
            skCircle(sketch, "E57.27.3.1", {"center": v(685.8, 76.2) * mm, "radius": 8.47 * mm, "construction": true});
            skLineSegment(sketch, "E57.direction1", {"start": v(0, 0) * mm, "end": v(25.4, 0) * mm, "construction": true});
            skLineSegment(sketch, "E57.direction2", {"start": v(0, 0) * mm, "end": v(0, 25.4) * mm, "construction": true});
            skLineSegment(sketch, "E58.bottom", {"start": v(0, -8.47) * mm, "end": v(101.6, -8.47) * mm});
            skLineSegment(sketch, "E58.top", {"start": v(0, 84.67) * mm, "end": v(101.6, 84.67) * mm});
            skLineSegment(sketch, "E58.left", {"start": v(-8.47, 0) * mm, "end": v(-8.47, 76.2) * mm});
            skLineSegment(sketch, "E58.right", {"start": v(110.07, 0) * mm, "end": v(110.07, 76.2) * mm});
            skLineSegment(sketch, "E59.bottom", {"start": v(685.8, -8.47) * mm, "end": v(584.2, -8.47) * mm});
            skLineSegment(sketch, "E59.top", {"start": v(685.8, 84.67) * mm, "end": v(584.2, 84.67) * mm});
            skLineSegment(sketch, "E59.left", {"start": v(694.27, 0) * mm, "end": v(694.27, 76.2) * mm});
            skLineSegment(sketch, "E59.right", {"start": v(575.73, 0) * mm, "end": v(575.73, 76.2) * mm});
            skPoint(sketch, "E60.visualSharp", {"position": v(-8.47, 84.67) * mm});
            skArc(sketch, "E60.filletArc", {"start": v(0, 84.67) * mm, "mid": v(-5.99, 82.19) * mm, "end": v(-8.47, 76.2) * mm});
            skPoint(sketch, "E61.visualSharp", {"position": v(110.07, 84.67) * mm});
            skArc(sketch, "E61.filletArc", {"start": v(110.07, 76.2) * mm, "mid": v(107.59, 82.19) * mm, "end": v(101.6, 84.67) * mm});
            skPoint(sketch, "E62.visualSharp", {"position": v(110.07, -8.47) * mm});
            skArc(sketch, "E62.filletArc", {"start": v(101.6, -8.47) * mm, "mid": v(107.59, -5.99) * mm, "end": v(110.07, 0) * mm});
            skPoint(sketch, "E63.visualSharp", {"position": v(-8.47, -8.47) * mm});
            skArc(sketch, "E63.filletArc", {"start": v(-8.47, 0) * mm, "mid": v(-5.99, -5.99) * mm, "end": v(0, -8.47) * mm});
            skPoint(sketch, "E64.visualSharp", {"position": v(575.73, 84.67) * mm});
            skArc(sketch, "E64.filletArc", {"start": v(584.2, 84.67) * mm, "mid": v(578.21, 82.19) * mm, "end": v(575.73, 76.2) * mm});
            skPoint(sketch, "E65.visualSharp", {"position": v(694.27, 84.67) * mm});
            skArc(sketch, "E65.filletArc", {"start": v(694.27, 76.2) * mm, "mid": v(691.79, 82.19) * mm, "end": v(685.8, 84.67) * mm});
            skPoint(sketch, "E66.visualSharp", {"position": v(694.27, -8.47) * mm});
            skArc(sketch, "E66.filletArc", {"start": v(685.8, -8.47) * mm, "mid": v(691.79, -5.99) * mm, "end": v(694.27, 0) * mm});
            skPoint(sketch, "E67.visualSharp", {"position": v(575.73, -8.47) * mm});
            skArc(sketch, "E67.filletArc", {"start": v(575.73, 0) * mm, "mid": v(578.21, -5.99) * mm, "end": v(584.2, -8.47) * mm});
            skSolve(sketch);
        }
        {
            var Q0;
            Q0=makeQuery(id+"F9.imprint","IMPRINT",FACE,{"disambiguationData":[TD([[makeQuery(id+"F9.imprint","IMPRINT",EDGE,{"derivedFrom":sQuery(id+"F9.wireOp",EDGE,"E50.0")}),-1.0]])]});
            var Q1;
            Q1=makeQuery(id+"F9.imprint","IMPRINT",FACE,{"disambiguationData":[TD([[makeQuery(id+"F9.imprint","IMPRINT",EDGE,{"derivedFrom":sQuery(id+"F9.wireOp",EDGE,"E52")}),1.0]])]});
            var Q2;
            Q2=sQuery(id+"F2.wireOp",VERTEX,"E11.left.end");
            extrude(context, id + "F10", {"entities" : qUnion([Q0, Q1]), "endBound" : BoundingType.UP_TO_VERTEX, "oppositeDirection" : true, "endBoundEntityVertex" : qUnion([Q2]), "depth" : 25.4 * mm});
        }
        {
            var Q0;
            Q0=qCreatedBy(makeId("Top.planeOp"),FACE);
            var sketch = newSketch(context, id + "F11", { "sketchPlane" : qUnion([Q0])});
            skCircle(sketch, "E68.0", {"center": v(103.19, 38.1) * mm, "radius": 19.05 * mm, "construction": true});
            skArc(sketch, "E69", {"start": v(95, 20.47) * mm, "mid": v(117.85, 50.85) * mm, "end": v(84.6, 32.45) * mm});
            skLineSegment(sketch, "E70", {"start": v(103.19, 38.1) * mm, "end": v(80.22, 18.13) * mm, "construction": true});
            skCircle(sketch, "E71.0", {"center": v(90.19, 38.1) * mm, "radius": 1.59 * mm, "construction": true});
            skCircle(sketch, "E71.1", {"center": v(96.69, 49.36) * mm, "radius": 1.59 * mm, "construction": true});
            skCircle(sketch, "E71.3", {"center": v(96.69, 26.84) * mm, "radius": 1.59 * mm, "construction": true});
            skLineSegment(sketch, "E72", {"start": v(84.6, 32.45) * mm, "end": v(75, 24.12) * mm});
            skLineSegment(sketch, "E73", {"start": v(75, 24.12) * mm, "end": v(85.42, 12.14) * mm});
            skLineSegment(sketch, "E74", {"start": v(85.42, 12.14) * mm, "end": v(95, 20.47) * mm});
            skLineSegment(sketch, "E75", {"start": v(90.19, 38.1) * mm, "end": v(116.19, 38.1) * mm, "construction": true});
            skCircle(sketch, "E76", {"center": v(116.19, 38.1) * mm, "radius": 1.59 * mm, "construction": true});
            skCircle(sketch, "E77.0", {"center": v(0, 0) * mm, "radius": 2.38 * mm, "construction": true});
            skCircle(sketch, "E77.1", {"center": v(0, 0) * mm, "radius": 8.47 * mm, "construction": true});
            skCircle(sketch, "E78.0.1.0", {"center": v(0, 25.4) * mm, "radius": 8.47 * mm, "construction": true});
            skCircle(sketch, "E78.0.1.1", {"center": v(0, 25.4) * mm, "radius": 2.38 * mm, "construction": true});
            skCircle(sketch, "E78.0.2.0", {"center": v(0, 50.8) * mm, "radius": 8.47 * mm, "construction": true});
            skCircle(sketch, "E78.0.2.1", {"center": v(0, 50.8) * mm, "radius": 2.38 * mm, "construction": true});
            skCircle(sketch, "E78.0.3.0", {"center": v(0, 76.2) * mm, "radius": 8.47 * mm, "construction": true});
            skCircle(sketch, "E78.0.3.1", {"center": v(0, 76.2) * mm, "radius": 2.38 * mm, "construction": true});
            skCircle(sketch, "E78.1.0.0", {"center": v(25.4, 0) * mm, "radius": 8.47 * mm, "construction": true});
            skCircle(sketch, "E78.1.0.1", {"center": v(25.4, 0) * mm, "radius": 2.38 * mm, "construction": true});
            skCircle(sketch, "E78.1.1.0", {"center": v(25.4, 25.4) * mm, "radius": 8.47 * mm, "construction": true});
            skCircle(sketch, "E78.1.1.1", {"center": v(25.4, 25.4) * mm, "radius": 2.38 * mm, "construction": true});
            skCircle(sketch, "E78.1.2.0", {"center": v(25.4, 50.8) * mm, "radius": 8.47 * mm, "construction": true});
            skCircle(sketch, "E78.1.2.1", {"center": v(25.4, 50.8) * mm, "radius": 2.38 * mm, "construction": true});
            skCircle(sketch, "E78.1.3.0", {"center": v(25.4, 76.2) * mm, "radius": 8.47 * mm, "construction": true});
            skCircle(sketch, "E78.1.3.1", {"center": v(25.4, 76.2) * mm, "radius": 2.38 * mm, "construction": true});
            skCircle(sketch, "E78.2.0.0", {"center": v(50.8, 0) * mm, "radius": 8.47 * mm, "construction": true});
            skCircle(sketch, "E78.2.0.1", {"center": v(50.8, 0) * mm, "radius": 2.38 * mm});
            skCircle(sketch, "E78.2.1.0", {"center": v(50.8, 25.4) * mm, "radius": 8.47 * mm, "construction": true});
            skCircle(sketch, "E78.2.1.1", {"center": v(50.8, 25.4) * mm, "radius": 2.38 * mm});
            skCircle(sketch, "E78.2.2.0", {"center": v(50.8, 50.8) * mm, "radius": 8.47 * mm, "construction": true});
            skCircle(sketch, "E78.2.2.1", {"center": v(50.8, 50.8) * mm, "radius": 2.38 * mm});
            skCircle(sketch, "E78.2.3.0", {"center": v(50.8, 76.2) * mm, "radius": 8.47 * mm, "construction": true});
            skCircle(sketch, "E78.2.3.1", {"center": v(50.8, 76.2) * mm, "radius": 2.38 * mm});
            skCircle(sketch, "E78.3.0.0", {"center": v(76.2, 0) * mm, "radius": 8.47 * mm, "construction": true});
            skCircle(sketch, "E78.3.0.1", {"center": v(76.2, 0) * mm, "radius": 2.38 * mm});
            skCircle(sketch, "E78.3.1.0", {"center": v(76.2, 25.4) * mm, "radius": 8.47 * mm, "construction": true});
            skCircle(sketch, "E78.3.1.1", {"center": v(76.2, 25.4) * mm, "radius": 2.38 * mm, "construction": true});
            skCircle(sketch, "E78.3.2.0", {"center": v(76.2, 50.8) * mm, "radius": 8.47 * mm, "construction": true});
            skCircle(sketch, "E78.3.2.1", {"center": v(76.2, 50.8) * mm, "radius": 2.38 * mm});
            skCircle(sketch, "E78.3.3.0", {"center": v(76.2, 76.2) * mm, "radius": 8.47 * mm, "construction": true});
            skCircle(sketch, "E78.3.3.1", {"center": v(76.2, 76.2) * mm, "radius": 2.38 * mm});
            skCircle(sketch, "E78.4.0.0", {"center": v(101.6, 0) * mm, "radius": 8.47 * mm, "construction": true});
            skCircle(sketch, "E78.4.0.1", {"center": v(101.6, 0) * mm, "radius": 2.38 * mm});
            skCircle(sketch, "E78.4.1.0", {"center": v(101.6, 25.4) * mm, "radius": 8.47 * mm, "construction": true});
            skCircle(sketch, "E78.4.1.1", {"center": v(101.6, 25.4) * mm, "radius": 2.38 * mm, "construction": true});
            skCircle(sketch, "E78.4.2.0", {"center": v(101.6, 50.8) * mm, "radius": 8.47 * mm, "construction": true});
            skCircle(sketch, "E78.4.2.1", {"center": v(101.6, 50.8) * mm, "radius": 2.38 * mm, "construction": true});
            skCircle(sketch, "E78.4.3.0", {"center": v(101.6, 76.2) * mm, "radius": 8.47 * mm, "construction": true});
            skCircle(sketch, "E78.4.3.1", {"center": v(101.6, 76.2) * mm, "radius": 2.38 * mm});
            skCircle(sketch, "E78.5.0.0", {"center": v(127, 0) * mm, "radius": 8.47 * mm, "construction": true});
            skCircle(sketch, "E78.5.0.1", {"center": v(127, 0) * mm, "radius": 2.38 * mm});
            skCircle(sketch, "E78.5.1.0", {"center": v(127, 25.4) * mm, "radius": 8.47 * mm, "construction": true});
            skCircle(sketch, "E78.5.1.1", {"center": v(127, 25.4) * mm, "radius": 2.38 * mm, "construction": true});
            skCircle(sketch, "E78.5.2.0", {"center": v(127, 50.8) * mm, "radius": 8.47 * mm, "construction": true});
            skCircle(sketch, "E78.5.2.1", {"center": v(127, 50.8) * mm, "radius": 2.38 * mm, "construction": true});
            skCircle(sketch, "E78.5.3.0", {"center": v(127, 76.2) * mm, "radius": 8.47 * mm, "construction": true});
            skCircle(sketch, "E78.5.3.1", {"center": v(127, 76.2) * mm, "radius": 2.38 * mm});
            skCircle(sketch, "E78.6.0.0", {"center": v(152.4, 0) * mm, "radius": 8.47 * mm, "construction": true});
            skCircle(sketch, "E78.6.0.1", {"center": v(152.4, 0) * mm, "radius": 2.38 * mm});
            skCircle(sketch, "E78.6.1.0", {"center": v(152.4, 25.4) * mm, "radius": 8.47 * mm, "construction": true});
            skCircle(sketch, "E78.6.1.1", {"center": v(152.4, 25.4) * mm, "radius": 2.38 * mm});
            skCircle(sketch, "E78.6.2.0", {"center": v(152.4, 50.8) * mm, "radius": 8.47 * mm, "construction": true});
            skCircle(sketch, "E78.6.2.1", {"center": v(152.4, 50.8) * mm, "radius": 2.38 * mm});
            skCircle(sketch, "E78.6.3.0", {"center": v(152.4, 76.2) * mm, "radius": 8.47 * mm, "construction": true});
            skCircle(sketch, "E78.6.3.1", {"center": v(152.4, 76.2) * mm, "radius": 2.38 * mm});
            skCircle(sketch, "E78.7.0.0", {"center": v(177.8, 0) * mm, "radius": 8.47 * mm, "construction": true});
            skCircle(sketch, "E78.7.0.1", {"center": v(177.8, 0) * mm, "radius": 2.38 * mm, "construction": true});
            skCircle(sketch, "E78.7.1.0", {"center": v(177.8, 25.4) * mm, "radius": 8.47 * mm, "construction": true});
            skCircle(sketch, "E78.7.1.1", {"center": v(177.8, 25.4) * mm, "radius": 2.38 * mm, "construction": true});
            skCircle(sketch, "E78.7.2.0", {"center": v(177.8, 50.8) * mm, "radius": 8.47 * mm, "construction": true});
            skCircle(sketch, "E78.7.2.1", {"center": v(177.8, 50.8) * mm, "radius": 2.38 * mm, "construction": true});
            skCircle(sketch, "E78.7.3.0", {"center": v(177.8, 76.2) * mm, "radius": 8.47 * mm, "construction": true});
            skCircle(sketch, "E78.7.3.1", {"center": v(177.8, 76.2) * mm, "radius": 2.38 * mm, "construction": true});
            skCircle(sketch, "E78.8.0.0", {"center": v(203.2, 0) * mm, "radius": 8.47 * mm, "construction": true});
            skCircle(sketch, "E78.8.0.1", {"center": v(203.2, 0) * mm, "radius": 2.38 * mm, "construction": true});
            skCircle(sketch, "E78.8.1.0", {"center": v(203.2, 25.4) * mm, "radius": 8.47 * mm, "construction": true});
            skCircle(sketch, "E78.8.1.1", {"center": v(203.2, 25.4) * mm, "radius": 2.38 * mm, "construction": true});
            skCircle(sketch, "E78.8.2.0", {"center": v(203.2, 50.8) * mm, "radius": 8.47 * mm, "construction": true});
            skCircle(sketch, "E78.8.2.1", {"center": v(203.2, 50.8) * mm, "radius": 2.38 * mm, "construction": true});
            skCircle(sketch, "E78.8.3.0", {"center": v(203.2, 76.2) * mm, "radius": 8.47 * mm, "construction": true});
            skCircle(sketch, "E78.8.3.1", {"center": v(203.2, 76.2) * mm, "radius": 2.38 * mm, "construction": true});
            skCircle(sketch, "E78.9.0.0", {"center": v(228.6, 0) * mm, "radius": 8.47 * mm, "construction": true});
            skCircle(sketch, "E78.9.0.1", {"center": v(228.6, 0) * mm, "radius": 2.38 * mm, "construction": true});
            skCircle(sketch, "E78.9.1.0", {"center": v(228.6, 25.4) * mm, "radius": 8.47 * mm, "construction": true});
            skCircle(sketch, "E78.9.1.1", {"center": v(228.6, 25.4) * mm, "radius": 2.38 * mm, "construction": true});
            skCircle(sketch, "E78.9.2.0", {"center": v(228.6, 50.8) * mm, "radius": 8.47 * mm, "construction": true});
            skCircle(sketch, "E78.9.2.1", {"center": v(228.6, 50.8) * mm, "radius": 2.38 * mm, "construction": true});
            skCircle(sketch, "E78.9.3.0", {"center": v(228.6, 76.2) * mm, "radius": 8.47 * mm, "construction": true});
            skCircle(sketch, "E78.9.3.1", {"center": v(228.6, 76.2) * mm, "radius": 2.38 * mm, "construction": true});
            skCircle(sketch, "E78.10.0.0", {"center": v(254, 0) * mm, "radius": 8.47 * mm, "construction": true});
            skCircle(sketch, "E78.10.0.1", {"center": v(254, 0) * mm, "radius": 2.38 * mm, "construction": true});
            skCircle(sketch, "E78.10.1.0", {"center": v(254, 25.4) * mm, "radius": 8.47 * mm, "construction": true});
            skCircle(sketch, "E78.10.1.1", {"center": v(254, 25.4) * mm, "radius": 2.38 * mm, "construction": true});
            skCircle(sketch, "E78.10.2.0", {"center": v(254, 50.8) * mm, "radius": 8.47 * mm, "construction": true});
            skCircle(sketch, "E78.10.2.1", {"center": v(254, 50.8) * mm, "radius": 2.38 * mm, "construction": true});
            skCircle(sketch, "E78.10.3.0", {"center": v(254, 76.2) * mm, "radius": 8.47 * mm, "construction": true});
            skCircle(sketch, "E78.10.3.1", {"center": v(254, 76.2) * mm, "radius": 2.38 * mm, "construction": true});
            skCircle(sketch, "E78.11.0.0", {"center": v(279.4, 0) * mm, "radius": 8.47 * mm, "construction": true});
            skCircle(sketch, "E78.11.0.1", {"center": v(279.4, 0) * mm, "radius": 2.38 * mm, "construction": true});
            skCircle(sketch, "E78.11.1.0", {"center": v(279.4, 25.4) * mm, "radius": 8.47 * mm, "construction": true});
            skCircle(sketch, "E78.11.1.1", {"center": v(279.4, 25.4) * mm, "radius": 2.38 * mm, "construction": true});
            skCircle(sketch, "E78.11.2.0", {"center": v(279.4, 50.8) * mm, "radius": 8.47 * mm, "construction": true});
            skCircle(sketch, "E78.11.2.1", {"center": v(279.4, 50.8) * mm, "radius": 2.38 * mm, "construction": true});
            skCircle(sketch, "E78.11.3.0", {"center": v(279.4, 76.2) * mm, "radius": 8.47 * mm, "construction": true});
            skCircle(sketch, "E78.11.3.1", {"center": v(279.4, 76.2) * mm, "radius": 2.38 * mm, "construction": true});
            skCircle(sketch, "E78.12.0.0", {"center": v(304.8, 0) * mm, "radius": 8.47 * mm, "construction": true});
            skCircle(sketch, "E78.12.0.1", {"center": v(304.8, 0) * mm, "radius": 2.38 * mm, "construction": true});
            skCircle(sketch, "E78.12.1.0", {"center": v(304.8, 25.4) * mm, "radius": 8.47 * mm, "construction": true});
            skCircle(sketch, "E78.12.1.1", {"center": v(304.8, 25.4) * mm, "radius": 2.38 * mm, "construction": true});
            skCircle(sketch, "E78.12.2.0", {"center": v(304.8, 50.8) * mm, "radius": 8.47 * mm, "construction": true});
            skCircle(sketch, "E78.12.2.1", {"center": v(304.8, 50.8) * mm, "radius": 2.38 * mm, "construction": true});
            skCircle(sketch, "E78.12.3.0", {"center": v(304.8, 76.2) * mm, "radius": 8.47 * mm, "construction": true});
            skCircle(sketch, "E78.12.3.1", {"center": v(304.8, 76.2) * mm, "radius": 2.38 * mm, "construction": true});
            skCircle(sketch, "E78.13.0.0", {"center": v(330.2, 0) * mm, "radius": 8.47 * mm, "construction": true});
            skCircle(sketch, "E78.13.0.1", {"center": v(330.2, 0) * mm, "radius": 2.38 * mm, "construction": true});
            skCircle(sketch, "E78.13.1.0", {"center": v(330.2, 25.4) * mm, "radius": 8.47 * mm, "construction": true});
            skCircle(sketch, "E78.13.1.1", {"center": v(330.2, 25.4) * mm, "radius": 2.38 * mm, "construction": true});
            skCircle(sketch, "E78.13.2.0", {"center": v(330.2, 50.8) * mm, "radius": 8.47 * mm, "construction": true});
            skCircle(sketch, "E78.13.2.1", {"center": v(330.2, 50.8) * mm, "radius": 2.38 * mm, "construction": true});
            skCircle(sketch, "E78.13.3.0", {"center": v(330.2, 76.2) * mm, "radius": 8.47 * mm, "construction": true});
            skCircle(sketch, "E78.13.3.1", {"center": v(330.2, 76.2) * mm, "radius": 2.38 * mm, "construction": true});
            skCircle(sketch, "E78.14.0.0", {"center": v(355.6, 0) * mm, "radius": 8.47 * mm, "construction": true});
            skCircle(sketch, "E78.14.0.1", {"center": v(355.6, 0) * mm, "radius": 2.38 * mm, "construction": true});
            skCircle(sketch, "E78.14.1.0", {"center": v(355.6, 25.4) * mm, "radius": 8.47 * mm, "construction": true});
            skCircle(sketch, "E78.14.1.1", {"center": v(355.6, 25.4) * mm, "radius": 2.38 * mm, "construction": true});
            skCircle(sketch, "E78.14.2.0", {"center": v(355.6, 50.8) * mm, "radius": 8.47 * mm, "construction": true});
            skCircle(sketch, "E78.14.2.1", {"center": v(355.6, 50.8) * mm, "radius": 2.38 * mm, "construction": true});
            skCircle(sketch, "E78.14.3.0", {"center": v(355.6, 76.2) * mm, "radius": 8.47 * mm, "construction": true});
            skCircle(sketch, "E78.14.3.1", {"center": v(355.6, 76.2) * mm, "radius": 2.38 * mm, "construction": true});
            skCircle(sketch, "E78.15.0.0", {"center": v(381, 0) * mm, "radius": 8.47 * mm, "construction": true});
            skCircle(sketch, "E78.15.0.1", {"center": v(381, 0) * mm, "radius": 2.38 * mm, "construction": true});
            skCircle(sketch, "E78.15.1.0", {"center": v(381, 25.4) * mm, "radius": 8.47 * mm, "construction": true});
            skCircle(sketch, "E78.15.1.1", {"center": v(381, 25.4) * mm, "radius": 2.38 * mm, "construction": true});
            skCircle(sketch, "E78.15.2.0", {"center": v(381, 50.8) * mm, "radius": 8.47 * mm, "construction": true});
            skCircle(sketch, "E78.15.2.1", {"center": v(381, 50.8) * mm, "radius": 2.38 * mm, "construction": true});
            skCircle(sketch, "E78.15.3.0", {"center": v(381, 76.2) * mm, "radius": 8.47 * mm, "construction": true});
            skCircle(sketch, "E78.15.3.1", {"center": v(381, 76.2) * mm, "radius": 2.38 * mm, "construction": true});
            skCircle(sketch, "E78.16.0.0", {"center": v(406.4, 0) * mm, "radius": 8.47 * mm, "construction": true});
            skCircle(sketch, "E78.16.0.1", {"center": v(406.4, 0) * mm, "radius": 2.38 * mm, "construction": true});
            skCircle(sketch, "E78.16.1.0", {"center": v(406.4, 25.4) * mm, "radius": 8.47 * mm, "construction": true});
            skCircle(sketch, "E78.16.1.1", {"center": v(406.4, 25.4) * mm, "radius": 2.38 * mm, "construction": true});
            skCircle(sketch, "E78.16.2.0", {"center": v(406.4, 50.8) * mm, "radius": 8.47 * mm, "construction": true});
            skCircle(sketch, "E78.16.2.1", {"center": v(406.4, 50.8) * mm, "radius": 2.38 * mm, "construction": true});
            skCircle(sketch, "E78.16.3.0", {"center": v(406.4, 76.2) * mm, "radius": 8.47 * mm, "construction": true});
            skCircle(sketch, "E78.16.3.1", {"center": v(406.4, 76.2) * mm, "radius": 2.38 * mm, "construction": true});
            skCircle(sketch, "E78.17.0.0", {"center": v(431.8, 0) * mm, "radius": 8.47 * mm, "construction": true});
            skCircle(sketch, "E78.17.0.1", {"center": v(431.8, 0) * mm, "radius": 2.38 * mm, "construction": true});
            skCircle(sketch, "E78.17.1.0", {"center": v(431.8, 25.4) * mm, "radius": 8.47 * mm, "construction": true});
            skCircle(sketch, "E78.17.1.1", {"center": v(431.8, 25.4) * mm, "radius": 2.38 * mm, "construction": true});
            skCircle(sketch, "E78.17.2.0", {"center": v(431.8, 50.8) * mm, "radius": 8.47 * mm, "construction": true});
            skCircle(sketch, "E78.17.2.1", {"center": v(431.8, 50.8) * mm, "radius": 2.38 * mm, "construction": true});
            skCircle(sketch, "E78.17.3.0", {"center": v(431.8, 76.2) * mm, "radius": 8.47 * mm, "construction": true});
            skCircle(sketch, "E78.17.3.1", {"center": v(431.8, 76.2) * mm, "radius": 2.38 * mm, "construction": true});
            skCircle(sketch, "E78.18.0.0", {"center": v(457.2, 0) * mm, "radius": 8.47 * mm, "construction": true});
            skCircle(sketch, "E78.18.0.1", {"center": v(457.2, 0) * mm, "radius": 2.38 * mm, "construction": true});
            skCircle(sketch, "E78.18.1.0", {"center": v(457.2, 25.4) * mm, "radius": 8.47 * mm, "construction": true});
            skCircle(sketch, "E78.18.1.1", {"center": v(457.2, 25.4) * mm, "radius": 2.38 * mm, "construction": true});
            skCircle(sketch, "E78.18.2.0", {"center": v(457.2, 50.8) * mm, "radius": 8.47 * mm, "construction": true});
            skCircle(sketch, "E78.18.2.1", {"center": v(457.2, 50.8) * mm, "radius": 2.38 * mm, "construction": true});
            skCircle(sketch, "E78.18.3.0", {"center": v(457.2, 76.2) * mm, "radius": 8.47 * mm, "construction": true});
            skCircle(sketch, "E78.18.3.1", {"center": v(457.2, 76.2) * mm, "radius": 2.38 * mm, "construction": true});
            skCircle(sketch, "E78.19.0.0", {"center": v(482.6, 0) * mm, "radius": 8.47 * mm, "construction": true});
            skCircle(sketch, "E78.19.0.1", {"center": v(482.6, 0) * mm, "radius": 2.38 * mm, "construction": true});
            skCircle(sketch, "E78.19.1.0", {"center": v(482.6, 25.4) * mm, "radius": 8.47 * mm, "construction": true});
            skCircle(sketch, "E78.19.1.1", {"center": v(482.6, 25.4) * mm, "radius": 2.38 * mm, "construction": true});
            skCircle(sketch, "E78.19.2.0", {"center": v(482.6, 50.8) * mm, "radius": 8.47 * mm, "construction": true});
            skCircle(sketch, "E78.19.2.1", {"center": v(482.6, 50.8) * mm, "radius": 2.38 * mm, "construction": true});
            skCircle(sketch, "E78.19.3.0", {"center": v(482.6, 76.2) * mm, "radius": 8.47 * mm, "construction": true});
            skCircle(sketch, "E78.19.3.1", {"center": v(482.6, 76.2) * mm, "radius": 2.38 * mm, "construction": true});
            skCircle(sketch, "E78.20.0.0", {"center": v(508, 0) * mm, "radius": 8.47 * mm, "construction": true});
            skCircle(sketch, "E78.20.0.1", {"center": v(508, 0) * mm, "radius": 2.38 * mm, "construction": true});
            skCircle(sketch, "E78.20.1.0", {"center": v(508, 25.4) * mm, "radius": 8.47 * mm, "construction": true});
            skCircle(sketch, "E78.20.1.1", {"center": v(508, 25.4) * mm, "radius": 2.38 * mm, "construction": true});
            skCircle(sketch, "E78.20.2.0", {"center": v(508, 50.8) * mm, "radius": 8.47 * mm, "construction": true});
            skCircle(sketch, "E78.20.2.1", {"center": v(508, 50.8) * mm, "radius": 2.38 * mm, "construction": true});
            skCircle(sketch, "E78.20.3.0", {"center": v(508, 76.2) * mm, "radius": 8.47 * mm, "construction": true});
            skCircle(sketch, "E78.20.3.1", {"center": v(508, 76.2) * mm, "radius": 2.38 * mm, "construction": true});
            skCircle(sketch, "E78.21.0.0", {"center": v(533.4, 0) * mm, "radius": 8.47 * mm, "construction": true});
            skCircle(sketch, "E78.21.0.1", {"center": v(533.4, 0) * mm, "radius": 2.38 * mm, "construction": true});
            skCircle(sketch, "E78.21.1.0", {"center": v(533.4, 25.4) * mm, "radius": 8.47 * mm, "construction": true});
            skCircle(sketch, "E78.21.1.1", {"center": v(533.4, 25.4) * mm, "radius": 2.38 * mm, "construction": true});
            skCircle(sketch, "E78.21.2.0", {"center": v(533.4, 50.8) * mm, "radius": 8.47 * mm, "construction": true});
            skCircle(sketch, "E78.21.2.1", {"center": v(533.4, 50.8) * mm, "radius": 2.38 * mm, "construction": true});
            skCircle(sketch, "E78.21.3.0", {"center": v(533.4, 76.2) * mm, "radius": 8.47 * mm, "construction": true});
            skCircle(sketch, "E78.21.3.1", {"center": v(533.4, 76.2) * mm, "radius": 2.38 * mm, "construction": true});
            skCircle(sketch, "E78.22.0.0", {"center": v(558.8, 0) * mm, "radius": 8.47 * mm, "construction": true});
            skCircle(sketch, "E78.22.0.1", {"center": v(558.8, 0) * mm, "radius": 2.38 * mm, "construction": true});
            skCircle(sketch, "E78.22.1.0", {"center": v(558.8, 25.4) * mm, "radius": 8.47 * mm, "construction": true});
            skCircle(sketch, "E78.22.1.1", {"center": v(558.8, 25.4) * mm, "radius": 2.38 * mm, "construction": true});
            skCircle(sketch, "E78.22.2.0", {"center": v(558.8, 50.8) * mm, "radius": 8.47 * mm, "construction": true});
            skCircle(sketch, "E78.22.2.1", {"center": v(558.8, 50.8) * mm, "radius": 2.38 * mm, "construction": true});
            skCircle(sketch, "E78.22.3.0", {"center": v(558.8, 76.2) * mm, "radius": 8.47 * mm, "construction": true});
            skCircle(sketch, "E78.22.3.1", {"center": v(558.8, 76.2) * mm, "radius": 2.38 * mm, "construction": true});
            skCircle(sketch, "E78.23.0.0", {"center": v(584.2, 0) * mm, "radius": 8.47 * mm, "construction": true});
            skCircle(sketch, "E78.23.0.1", {"center": v(584.2, 0) * mm, "radius": 2.38 * mm, "construction": true});
            skCircle(sketch, "E78.23.1.0", {"center": v(584.2, 25.4) * mm, "radius": 8.47 * mm, "construction": true});
            skCircle(sketch, "E78.23.1.1", {"center": v(584.2, 25.4) * mm, "radius": 2.38 * mm, "construction": true});
            skCircle(sketch, "E78.23.2.0", {"center": v(584.2, 50.8) * mm, "radius": 8.47 * mm, "construction": true});
            skCircle(sketch, "E78.23.2.1", {"center": v(584.2, 50.8) * mm, "radius": 2.38 * mm, "construction": true});
            skCircle(sketch, "E78.23.3.0", {"center": v(584.2, 76.2) * mm, "radius": 8.47 * mm, "construction": true});
            skCircle(sketch, "E78.23.3.1", {"center": v(584.2, 76.2) * mm, "radius": 2.38 * mm, "construction": true});
            skCircle(sketch, "E78.24.0.0", {"center": v(609.6, 0) * mm, "radius": 8.47 * mm, "construction": true});
            skCircle(sketch, "E78.24.0.1", {"center": v(609.6, 0) * mm, "radius": 2.38 * mm, "construction": true});
            skCircle(sketch, "E78.24.1.0", {"center": v(609.6, 25.4) * mm, "radius": 8.47 * mm, "construction": true});
            skCircle(sketch, "E78.24.1.1", {"center": v(609.6, 25.4) * mm, "radius": 2.38 * mm, "construction": true});
            skCircle(sketch, "E78.24.2.0", {"center": v(609.6, 50.8) * mm, "radius": 8.47 * mm, "construction": true});
            skCircle(sketch, "E78.24.2.1", {"center": v(609.6, 50.8) * mm, "radius": 2.38 * mm, "construction": true});
            skCircle(sketch, "E78.24.3.0", {"center": v(609.6, 76.2) * mm, "radius": 8.47 * mm, "construction": true});
            skCircle(sketch, "E78.24.3.1", {"center": v(609.6, 76.2) * mm, "radius": 2.38 * mm, "construction": true});
            skCircle(sketch, "E78.25.0.0", {"center": v(635, 0) * mm, "radius": 8.47 * mm, "construction": true});
            skCircle(sketch, "E78.25.0.1", {"center": v(635, 0) * mm, "radius": 2.38 * mm, "construction": true});
            skCircle(sketch, "E78.25.1.0", {"center": v(635, 25.4) * mm, "radius": 8.47 * mm, "construction": true});
            skCircle(sketch, "E78.25.1.1", {"center": v(635, 25.4) * mm, "radius": 2.38 * mm, "construction": true});
            skCircle(sketch, "E78.25.2.0", {"center": v(635, 50.8) * mm, "radius": 8.47 * mm, "construction": true});
            skCircle(sketch, "E78.25.2.1", {"center": v(635, 50.8) * mm, "radius": 2.38 * mm, "construction": true});
            skCircle(sketch, "E78.25.3.0", {"center": v(635, 76.2) * mm, "radius": 8.47 * mm, "construction": true});
            skCircle(sketch, "E78.25.3.1", {"center": v(635, 76.2) * mm, "radius": 2.38 * mm, "construction": true});
            skCircle(sketch, "E78.26.0.0", {"center": v(660.4, 0) * mm, "radius": 8.47 * mm, "construction": true});
            skCircle(sketch, "E78.26.0.1", {"center": v(660.4, 0) * mm, "radius": 2.38 * mm, "construction": true});
            skCircle(sketch, "E78.26.1.0", {"center": v(660.4, 25.4) * mm, "radius": 8.47 * mm, "construction": true});
            skCircle(sketch, "E78.26.1.1", {"center": v(660.4, 25.4) * mm, "radius": 2.38 * mm, "construction": true});
            skCircle(sketch, "E78.26.2.0", {"center": v(660.4, 50.8) * mm, "radius": 8.47 * mm, "construction": true});
            skCircle(sketch, "E78.26.2.1", {"center": v(660.4, 50.8) * mm, "radius": 2.38 * mm, "construction": true});
            skCircle(sketch, "E78.26.3.0", {"center": v(660.4, 76.2) * mm, "radius": 8.47 * mm, "construction": true});
            skCircle(sketch, "E78.26.3.1", {"center": v(660.4, 76.2) * mm, "radius": 2.38 * mm, "construction": true});
            skCircle(sketch, "E78.27.0.0", {"center": v(685.8, 0) * mm, "radius": 8.47 * mm, "construction": true});
            skCircle(sketch, "E78.27.0.1", {"center": v(685.8, 0) * mm, "radius": 2.38 * mm, "construction": true});
            skCircle(sketch, "E78.27.1.0", {"center": v(685.8, 25.4) * mm, "radius": 8.47 * mm, "construction": true});
            skCircle(sketch, "E78.27.1.1", {"center": v(685.8, 25.4) * mm, "radius": 2.38 * mm, "construction": true});
            skCircle(sketch, "E78.27.2.0", {"center": v(685.8, 50.8) * mm, "radius": 8.47 * mm, "construction": true});
            skCircle(sketch, "E78.27.2.1", {"center": v(685.8, 50.8) * mm, "radius": 2.38 * mm, "construction": true});
            skCircle(sketch, "E78.27.3.0", {"center": v(685.8, 76.2) * mm, "radius": 8.47 * mm, "construction": true});
            skCircle(sketch, "E78.27.3.1", {"center": v(685.8, 76.2) * mm, "radius": 2.38 * mm, "construction": true});
            skLineSegment(sketch, "E78.direction1", {"start": v(0, 0) * mm, "end": v(25.4, 0) * mm, "construction": true});
            skLineSegment(sketch, "E78.direction2", {"start": v(0, 0) * mm, "end": v(0, 25.4) * mm, "construction": true});
            skLineSegment(sketch, "E79.bottom", {"start": v(50.8, 84.67) * mm, "end": v(152.4, 84.67) * mm});
            skLineSegment(sketch, "E79.top", {"start": v(50.8, -8.47) * mm, "end": v(152.4, -8.47) * mm});
            skLineSegment(sketch, "E79.left", {"start": v(42.33, 76.2) * mm, "end": v(42.33, 0) * mm});
            skLineSegment(sketch, "E79.right", {"start": v(160.87, 76.2) * mm, "end": v(160.87, 0) * mm});
            skPoint(sketch, "E80.visualSharp", {"position": v(42.33, 84.67) * mm});
            skArc(sketch, "E80.filletArc", {"start": v(50.8, 84.67) * mm, "mid": v(44.81, 82.19) * mm, "end": v(42.33, 76.2) * mm});
            skPoint(sketch, "E81.visualSharp", {"position": v(160.87, 84.67) * mm});
            skArc(sketch, "E81.filletArc", {"start": v(160.87, 76.2) * mm, "mid": v(158.39, 82.19) * mm, "end": v(152.4, 84.67) * mm});
            skPoint(sketch, "E82.visualSharp", {"position": v(160.87, -8.47) * mm});
            skArc(sketch, "E82.filletArc", {"start": v(152.4, -8.47) * mm, "mid": v(158.39, -5.99) * mm, "end": v(160.87, 0) * mm});
            skPoint(sketch, "E83.visualSharp", {"position": v(42.33, -8.47) * mm});
            skArc(sketch, "E83.filletArc", {"start": v(42.33, 0) * mm, "mid": v(44.81, -5.99) * mm, "end": v(50.8, -8.47) * mm});
            skSolve(sketch);
        }
        {
            var Q0;
            Q0=makeQuery(id+"F11.imprint","IMPRINT",FACE,{"disambiguationData":[TD([[makeQuery(id+"F11.imprint","IMPRINT",EDGE,{"derivedFrom":sQuery(id+"F11.wireOp",EDGE,"E69")}),-1.0]])]});
            var Q1;
            Q1=sQuery(id+"F2.wireOp",VERTEX,"E11.left.end");
            extrude(context, id + "F12", {"entities" : qUnion([Q0]), "endBound" : BoundingType.UP_TO_VERTEX, "oppositeDirection" : true, "endBoundEntityVertex" : qUnion([Q1]), "depth" : 25.4 * mm});
        }
        {
            var Q0;
            Q0=makeQuery(id+"F12.opExtrude","SWEPT_EDGE",EDGE,{"disambiguationData":[OSD([sQuery(id+"F11.wireOp",EDGE,"E69"),sQuery(id+"F11.wireOp",EDGE,"E72")])]});
            var Q1;
            Q1=makeQuery(id+"F12.opExtrude","SWEPT_EDGE",EDGE,{"disambiguationData":[OSD([sQuery(id+"F11.wireOp",EDGE,"E72"),sQuery(id+"F11.wireOp",EDGE,"E73")])]});
            var Q2;
            Q2=makeQuery(id+"F12.opExtrude","SWEPT_EDGE",EDGE,{"disambiguationData":[OSD([sQuery(id+"F11.wireOp",EDGE,"E73"),sQuery(id+"F11.wireOp",EDGE,"E74")])]});
            var Q3;
            Q3=makeQuery(id+"F12.opExtrude","SWEPT_EDGE",EDGE,{"disambiguationData":[OSD([sQuery(id+"F11.wireOp",EDGE,"E69"),sQuery(id+"F11.wireOp",EDGE,"E74")])]});
            fillet(context, id + "F13", {"entities" : qUnion([Q0, Q1, Q2, Q3]), "radius" : (getVariable(context, 'bitDiameter') / 2) * mm, "tangentPropagation" : true, "allowEdgeOverflow" : false});
        }
        {
            var Q0;
            Q0=qCreatedBy(makeId("Top.planeOp"),FACE);
            var sketch = newSketch(context, id + "F14", { "sketchPlane" : qUnion([Q0])});
            skCircle(sketch, "E84", {"center": v(0, 0) * mm, "radius": 2.38 * mm});
            skCircle(sketch, "E85", {"center": v(0, 0) * mm, "radius": 8.47 * mm, "construction": true});
            skCircle(sketch, "E86.0.1.0", {"center": v(0, 25.4) * mm, "radius": 8.47 * mm, "construction": true});
            skCircle(sketch, "E86.0.1.1", {"center": v(0, 25.4) * mm, "radius": 2.38 * mm});
            skCircle(sketch, "E86.0.2.0", {"center": v(0, 50.8) * mm, "radius": 8.47 * mm, "construction": true});
            skCircle(sketch, "E86.0.2.1", {"center": v(0, 50.8) * mm, "radius": 2.38 * mm});
            skCircle(sketch, "E86.1.0.0", {"center": v(25.4, 0) * mm, "radius": 8.47 * mm, "construction": true});
            skCircle(sketch, "E86.1.0.1", {"center": v(25.4, 0) * mm, "radius": 2.38 * mm});
            skCircle(sketch, "E86.1.1.0", {"center": v(25.4, 25.4) * mm, "radius": 8.47 * mm, "construction": true});
            skCircle(sketch, "E86.1.1.1", {"center": v(25.4, 25.4) * mm, "radius": 2.38 * mm});
            skCircle(sketch, "E86.1.2.0", {"center": v(25.4, 50.8) * mm, "radius": 8.47 * mm, "construction": true});
            skCircle(sketch, "E86.1.2.1", {"center": v(25.4, 50.8) * mm, "radius": 2.38 * mm});
            skCircle(sketch, "E86.2.0.0", {"center": v(50.8, 0) * mm, "radius": 8.47 * mm, "construction": true});
            skCircle(sketch, "E86.2.0.1", {"center": v(50.8, 0) * mm, "radius": 2.38 * mm});
            skCircle(sketch, "E86.2.1.0", {"center": v(50.8, 25.4) * mm, "radius": 8.47 * mm, "construction": true});
            skCircle(sketch, "E86.2.1.1", {"center": v(50.8, 25.4) * mm, "radius": 2.38 * mm});
            skCircle(sketch, "E86.2.2.0", {"center": v(50.8, 50.8) * mm, "radius": 8.47 * mm, "construction": true});
            skCircle(sketch, "E86.2.2.1", {"center": v(50.8, 50.8) * mm, "radius": 2.38 * mm, "construction": true});
            skLineSegment(sketch, "E86.direction1", {"start": v(0, 0) * mm, "end": v(25.4, 0) * mm, "construction": true});
            skLineSegment(sketch, "E86.direction2", {"start": v(0, 0) * mm, "end": v(0, 25.4) * mm, "construction": true});
            skLineSegment(sketch, "E87", {"start": v(-8.47, 0) * mm, "end": v(-8.47, 50.8) * mm});
            skLineSegment(sketch, "E88", {"start": v(5.99, 56.79) * mm, "end": v(56.79, 5.99) * mm});
            skLineSegment(sketch, "E89", {"start": v(0, -8.47) * mm, "end": v(50.8, -8.47) * mm});
            skArc(sketch, "E90.filletArc", {"start": v(-8.47, 0) * mm, "mid": v(-5.99, -5.99) * mm, "end": v(0, -8.47) * mm});
            skArc(sketch, "E91.filletArc", {"start": v(5.99, 56.79) * mm, "mid": v(-3.24, 58.62) * mm, "end": v(-8.47, 50.8) * mm});
            skArc(sketch, "E92.filletArc", {"start": v(50.8, -8.47) * mm, "mid": v(58.62, -3.24) * mm, "end": v(56.79, 5.99) * mm});
            skCircle(sketch, "E93.0.0.3", {"center": v(0, 76.2) * mm, "radius": 8.47 * mm, "construction": true});
            skCircle(sketch, "E93.2.0.3", {"center": v(0, 76.2) * mm, "radius": 2.38 * mm});
            skCircle(sketch, "E93.0.0.4", {"center": v(0, 101.6) * mm, "radius": 8.47 * mm, "construction": true});
            skCircle(sketch, "E93.2.0.4", {"center": v(0, 101.6) * mm, "radius": 2.38 * mm, "construction": true});
            skCircle(sketch, "E93.0.0.5", {"center": v(0, 127) * mm, "radius": 8.47 * mm, "construction": true});
            skCircle(sketch, "E93.2.0.5", {"center": v(0, 127) * mm, "radius": 2.38 * mm, "construction": true});
            skCircle(sketch, "E93.0.1.3", {"center": v(25.4, 76.2) * mm, "radius": 8.47 * mm, "construction": true});
            skCircle(sketch, "E93.2.1.3", {"center": v(25.4, 76.2) * mm, "radius": 2.38 * mm, "construction": true});
            skCircle(sketch, "E93.0.1.4", {"center": v(25.4, 101.6) * mm, "radius": 8.47 * mm, "construction": true});
            skCircle(sketch, "E93.2.1.4", {"center": v(25.4, 101.6) * mm, "radius": 2.38 * mm, "construction": true});
            skCircle(sketch, "E93.0.1.5", {"center": v(25.4, 127) * mm, "radius": 8.47 * mm, "construction": true});
            skCircle(sketch, "E93.2.1.5", {"center": v(25.4, 127) * mm, "radius": 2.38 * mm, "construction": true});
            skCircle(sketch, "E93.0.2.3", {"center": v(50.8, 76.2) * mm, "radius": 8.47 * mm, "construction": true});
            skCircle(sketch, "E93.2.2.3", {"center": v(50.8, 76.2) * mm, "radius": 2.38 * mm, "construction": true});
            skCircle(sketch, "E93.0.2.4", {"center": v(50.8, 101.6) * mm, "radius": 8.47 * mm, "construction": true});
            skCircle(sketch, "E93.2.2.4", {"center": v(50.8, 101.6) * mm, "radius": 2.38 * mm, "construction": true});
            skCircle(sketch, "E93.0.2.5", {"center": v(50.8, 127) * mm, "radius": 8.47 * mm, "construction": true});
            skCircle(sketch, "E93.2.2.5", {"center": v(50.8, 127) * mm, "radius": 2.38 * mm, "construction": true});
            skCircle(sketch, "E94.0.3.0", {"center": v(76.2, 0) * mm, "radius": 8.47 * mm, "construction": true});
            skCircle(sketch, "E94.2.3.0", {"center": v(76.2, 0) * mm, "radius": 2.38 * mm});
            skCircle(sketch, "E94.0.3.1", {"center": v(76.2, 25.4) * mm, "radius": 8.47 * mm, "construction": true});
            skCircle(sketch, "E94.2.3.1", {"center": v(76.2, 25.4) * mm, "radius": 2.38 * mm, "construction": true});
            skCircle(sketch, "E94.0.3.2", {"center": v(76.2, 50.8) * mm, "radius": 8.47 * mm, "construction": true});
            skCircle(sketch, "E94.2.3.2", {"center": v(76.2, 50.8) * mm, "radius": 2.38 * mm, "construction": true});
            skCircle(sketch, "E94.0.3.3", {"center": v(76.2, 76.2) * mm, "radius": 8.47 * mm, "construction": true});
            skCircle(sketch, "E94.2.3.3", {"center": v(76.2, 76.2) * mm, "radius": 2.38 * mm, "construction": true});
            skCircle(sketch, "E94.0.3.4", {"center": v(76.2, 101.6) * mm, "radius": 8.47 * mm, "construction": true});
            skCircle(sketch, "E94.2.3.4", {"center": v(76.2, 101.6) * mm, "radius": 2.38 * mm, "construction": true});
            skCircle(sketch, "E94.0.3.5", {"center": v(76.2, 127) * mm, "radius": 8.47 * mm, "construction": true});
            skCircle(sketch, "E94.2.3.5", {"center": v(76.2, 127) * mm, "radius": 2.38 * mm, "construction": true});
            skCircle(sketch, "E94.0.4.0", {"center": v(101.6, 0) * mm, "radius": 8.47 * mm, "construction": true});
            skCircle(sketch, "E94.2.4.0", {"center": v(101.6, 0) * mm, "radius": 2.38 * mm, "construction": true});
            skCircle(sketch, "E94.0.4.1", {"center": v(101.6, 25.4) * mm, "radius": 8.47 * mm, "construction": true});
            skCircle(sketch, "E94.2.4.1", {"center": v(101.6, 25.4) * mm, "radius": 2.38 * mm, "construction": true});
            skCircle(sketch, "E94.0.4.2", {"center": v(101.6, 50.8) * mm, "radius": 8.47 * mm, "construction": true});
            skCircle(sketch, "E94.2.4.2", {"center": v(101.6, 50.8) * mm, "radius": 2.38 * mm, "construction": true});
            skCircle(sketch, "E94.0.4.3", {"center": v(101.6, 76.2) * mm, "radius": 8.47 * mm, "construction": true});
            skCircle(sketch, "E94.2.4.3", {"center": v(101.6, 76.2) * mm, "radius": 2.38 * mm, "construction": true});
            skCircle(sketch, "E94.0.4.4", {"center": v(101.6, 101.6) * mm, "radius": 8.47 * mm, "construction": true});
            skCircle(sketch, "E94.2.4.4", {"center": v(101.6, 101.6) * mm, "radius": 2.38 * mm, "construction": true});
            skCircle(sketch, "E94.0.4.5", {"center": v(101.6, 127) * mm, "radius": 8.47 * mm, "construction": true});
            skCircle(sketch, "E94.2.4.5", {"center": v(101.6, 127) * mm, "radius": 2.38 * mm, "construction": true});
            skCircle(sketch, "E94.0.5.0", {"center": v(127, 0) * mm, "radius": 8.47 * mm, "construction": true});
            skCircle(sketch, "E94.2.5.0", {"center": v(127, 0) * mm, "radius": 2.38 * mm, "construction": true});
            skCircle(sketch, "E94.0.5.1", {"center": v(127, 25.4) * mm, "radius": 8.47 * mm, "construction": true});
            skCircle(sketch, "E94.2.5.1", {"center": v(127, 25.4) * mm, "radius": 2.38 * mm, "construction": true});
            skCircle(sketch, "E94.0.5.2", {"center": v(127, 50.8) * mm, "radius": 8.47 * mm, "construction": true});
            skCircle(sketch, "E94.2.5.2", {"center": v(127, 50.8) * mm, "radius": 2.38 * mm, "construction": true});
            skCircle(sketch, "E94.0.5.3", {"center": v(127, 76.2) * mm, "radius": 8.47 * mm, "construction": true});
            skCircle(sketch, "E94.2.5.3", {"center": v(127, 76.2) * mm, "radius": 2.38 * mm, "construction": true});
            skCircle(sketch, "E94.0.5.4", {"center": v(127, 101.6) * mm, "radius": 8.47 * mm, "construction": true});
            skCircle(sketch, "E94.2.5.4", {"center": v(127, 101.6) * mm, "radius": 2.38 * mm, "construction": true});
            skCircle(sketch, "E94.0.5.5", {"center": v(127, 127) * mm, "radius": 8.47 * mm, "construction": true});
            skCircle(sketch, "E94.2.5.5", {"center": v(127, 127) * mm, "radius": 2.38 * mm, "construction": true});
            skLineSegment(sketch, "E95", {"start": v(-8.47, 50.8) * mm, "end": v(-8.47, 76.2) * mm});
            skLineSegment(sketch, "E96", {"start": v(5.99, 82.19) * mm, "end": v(82.19, 5.99) * mm});
            skLineSegment(sketch, "E97", {"start": v(76.2, -8.47) * mm, "end": v(50.8, -8.47) * mm});
            skArc(sketch, "E98.filletArc", {"start": v(5.99, 82.19) * mm, "mid": v(-3.24, 84.02) * mm, "end": v(-8.47, 76.2) * mm});
            skArc(sketch, "E99", {"start": v(76.2, -8.47) * mm, "mid": v(84.02, -3.24) * mm, "end": v(82.19, 5.99) * mm});
            skSolve(sketch);
        }
        {
            var Q0;
            Q0=makeQuery(id+"F14.imprint","IMPRINT",FACE,{"disambiguationData":[TD([[makeQuery(id+"F14.imprint","IMPRINT",EDGE,{"derivedFrom":sQuery(id+"F14.wireOp",EDGE,"E84")}),-1.0]])]});
            var Q1;
            Q1=sQuery(id+"F2.wireOp",VERTEX,"E11.top.start");
            extrude(context, id + "F15", {"entities" : qUnion([Q0]), "endBound" : BoundingType.UP_TO_VERTEX, "oppositeDirection" : true, "endBoundEntityVertex" : qUnion([Q1]), "depth" : 25.4 * mm});
        }
        {
            var Q0;
            Q0=makeQuery(id+"F14.imprint","IMPRINT",FACE,{"disambiguationData":[TD([[makeQuery(id+"F14.imprint","IMPRINT",EDGE,{"derivedFrom":sQuery(id+"F14.wireOp",EDGE,"E84")}),-1.0]])]});
            var Q1;
            Q1=makeQuery(id+"F14.imprint","IMPRINT",FACE,{"disambiguationData":[TD([[makeQuery(id+"F14.imprint","IMPRINT",EDGE,{"derivedFrom":sQuery(id+"F14.wireOp",EDGE,"E86.1.2.1")}),-1.0]])]});
            var Q2;
            Q2=sQuery(id+"F2.wireOp",VERTEX,"E11.top.start");
            extrude(context, id + "F16", {"entities" : qUnion([Q0, Q1]), "endBound" : BoundingType.UP_TO_VERTEX, "oppositeDirection" : true, "endBoundEntityVertex" : qUnion([Q2]), "depth" : 25.4 * mm});
        }
    });
